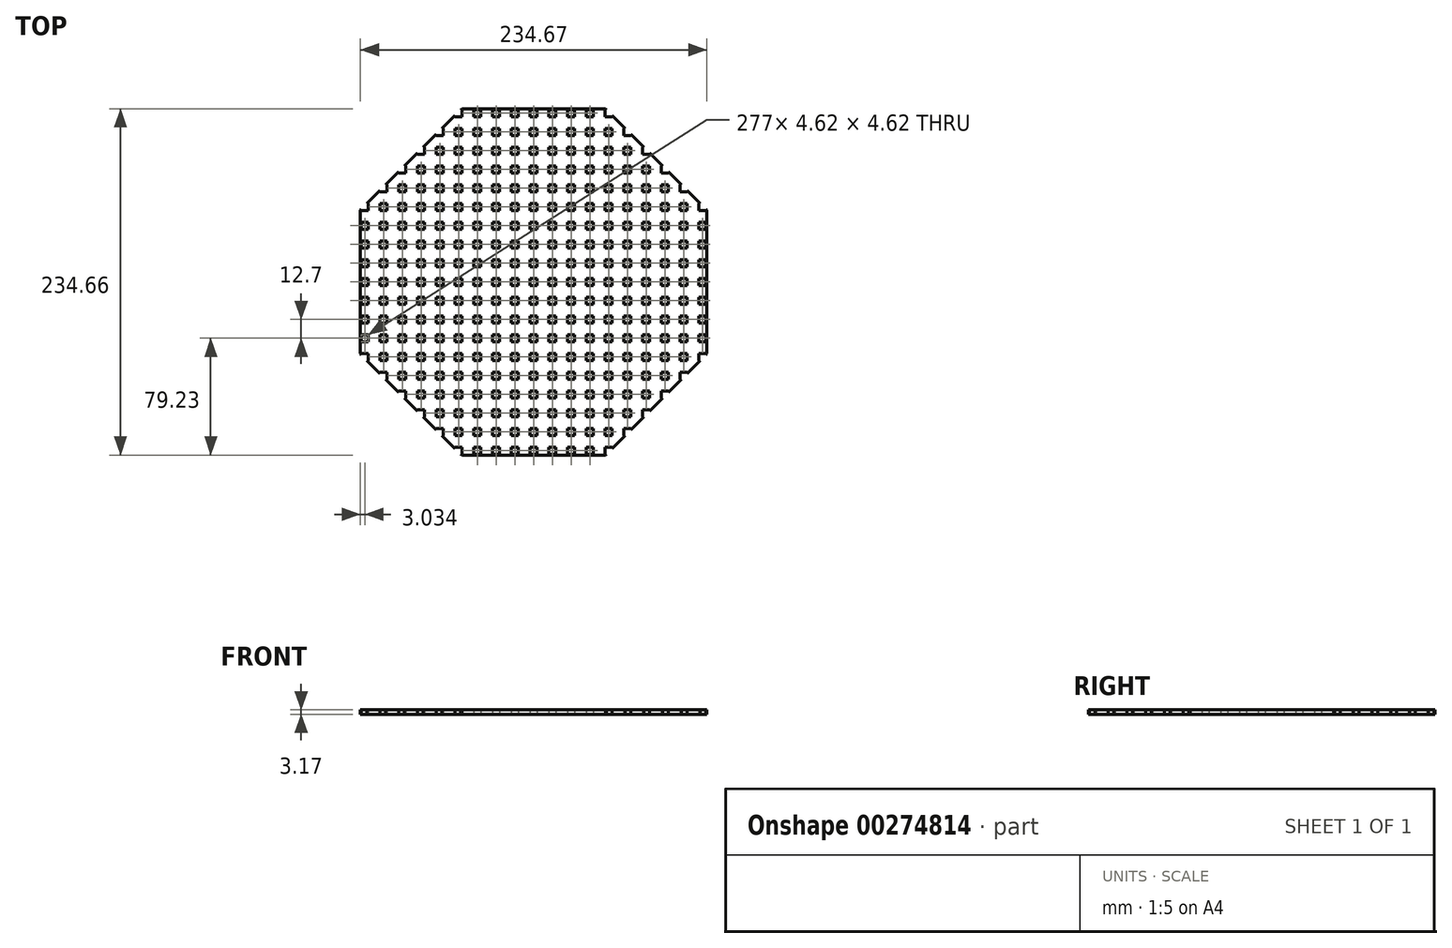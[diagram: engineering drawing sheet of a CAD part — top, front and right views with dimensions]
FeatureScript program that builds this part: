
annotation { "Feature Type Name" : "Feature", "Feature Type Description" : "" }
export const myFeature = defineFeature(function(context is Context, id is Id, definition is map)
    precondition{}
    {
        {
            var Q0;
            Q0=qCreatedBy(makeId("Top.planeOp"),FACE);
            var sketch = newSketch(context, id + "F0", { "sketchPlane" : qUnion([Q0])});
            skCircle(sketch, "E0.cCircle", {"center": v(2.93, 2.21) * mm, "radius": 127 * mm, "construction": true});
            skLineSegment(sketch, "E0.0", {"start": v(-114.4, 50.81) * mm, "end": v(-45.67, 119.54) * mm});
            skLineSegment(sketch, "E0.1", {"start": v(-45.67, 119.54) * mm, "end": v(51.53, 119.54) * mm});
            skLineSegment(sketch, "E0.2", {"start": v(51.53, 119.54) * mm, "end": v(120.27, 50.81) * mm});
            skLineSegment(sketch, "E0.3", {"start": v(120.27, 50.81) * mm, "end": v(120.27, -46.4) * mm});
            skLineSegment(sketch, "E0.4", {"start": v(120.27, -46.4) * mm, "end": v(51.53, -115.12) * mm});
            skLineSegment(sketch, "E0.5", {"start": v(51.53, -115.12) * mm, "end": v(-45.67, -115.12) * mm});
            skLineSegment(sketch, "E0.6", {"start": v(-45.67, -115.12) * mm, "end": v(-114.4, -46.4) * mm});
            skLineSegment(sketch, "E0.7", {"start": v(-114.4, -46.4) * mm, "end": v(-114.4, 50.81) * mm});
            skLineSegment(sketch, "E1.bottom", {"start": v(5.25, 4.52) * mm, "end": v(0.62, 4.52) * mm});
            skLineSegment(sketch, "E1.top", {"start": v(5.25, -0.1) * mm, "end": v(0.62, -0.1) * mm});
            skLineSegment(sketch, "E1.left", {"start": v(5.25, 4.52) * mm, "end": v(5.25, -0.1) * mm});
            skLineSegment(sketch, "E1.right", {"start": v(0.62, 4.52) * mm, "end": v(0.62, -0.1) * mm});
            skLineSegment(sketch, "E2", {"start": v(2.93, 2.21) * mm, "end": v(2.93, 119.54) * mm});
            skLineSegment(sketch, "E3", {"start": v(2.93, 2.21) * mm, "end": v(2.93, -115.12) * mm});
            skLineSegment(sketch, "E4", {"start": v(2.93, 2.21) * mm, "end": v(120.27, 2.21) * mm});
            skLineSegment(sketch, "E5", {"start": v(2.93, 2.21) * mm, "end": v(-114.4, 2.21) * mm});
            skLineSegment(sketch, "E6.0.1.0", {"start": v(5.25, 17.22) * mm, "end": v(0.62, 17.22) * mm});
            skLineSegment(sketch, "E6.0.1.1", {"start": v(0.62, 17.22) * mm, "end": v(0.62, 12.6) * mm});
            skLineSegment(sketch, "E6.0.1.2", {"start": v(5.25, 12.6) * mm, "end": v(0.62, 12.6) * mm});
            skLineSegment(sketch, "E6.0.1.3", {"start": v(5.25, 17.22) * mm, "end": v(5.25, 12.6) * mm});
            skLineSegment(sketch, "E6.0.2.0", {"start": v(5.25, 29.92) * mm, "end": v(0.62, 29.92) * mm});
            skLineSegment(sketch, "E6.0.2.1", {"start": v(0.62, 29.92) * mm, "end": v(0.62, 25.3) * mm});
            skLineSegment(sketch, "E6.0.2.2", {"start": v(5.25, 25.3) * mm, "end": v(0.62, 25.3) * mm});
            skLineSegment(sketch, "E6.0.2.3", {"start": v(5.25, 29.92) * mm, "end": v(5.25, 25.3) * mm});
            skLineSegment(sketch, "E6.0.3.0", {"start": v(5.25, 42.62) * mm, "end": v(0.62, 42.62) * mm});
            skLineSegment(sketch, "E6.0.3.1", {"start": v(0.62, 42.62) * mm, "end": v(0.62, 38) * mm});
            skLineSegment(sketch, "E6.0.3.2", {"start": v(5.25, 38) * mm, "end": v(0.62, 38) * mm});
            skLineSegment(sketch, "E6.0.3.3", {"start": v(5.25, 42.62) * mm, "end": v(5.25, 38) * mm});
            skLineSegment(sketch, "E6.0.4.0", {"start": v(5.25, 55.32) * mm, "end": v(0.62, 55.32) * mm});
            skLineSegment(sketch, "E6.0.4.1", {"start": v(0.62, 55.32) * mm, "end": v(0.62, 50.7) * mm});
            skLineSegment(sketch, "E6.0.4.2", {"start": v(5.25, 50.7) * mm, "end": v(0.62, 50.7) * mm});
            skLineSegment(sketch, "E6.0.4.3", {"start": v(5.25, 55.32) * mm, "end": v(5.25, 50.7) * mm});
            skLineSegment(sketch, "E6.0.5.0", {"start": v(5.25, 68.02) * mm, "end": v(0.62, 68.02) * mm});
            skLineSegment(sketch, "E6.0.5.1", {"start": v(0.62, 68.02) * mm, "end": v(0.62, 63.4) * mm});
            skLineSegment(sketch, "E6.0.5.2", {"start": v(5.25, 63.4) * mm, "end": v(0.62, 63.4) * mm});
            skLineSegment(sketch, "E6.0.5.3", {"start": v(5.25, 68.02) * mm, "end": v(5.25, 63.4) * mm});
            skLineSegment(sketch, "E6.0.6.0", {"start": v(5.25, 80.72) * mm, "end": v(0.62, 80.72) * mm});
            skLineSegment(sketch, "E6.0.6.1", {"start": v(0.62, 80.72) * mm, "end": v(0.62, 76.1) * mm});
            skLineSegment(sketch, "E6.0.6.2", {"start": v(5.25, 76.1) * mm, "end": v(0.62, 76.1) * mm});
            skLineSegment(sketch, "E6.0.6.3", {"start": v(5.25, 80.72) * mm, "end": v(5.25, 76.1) * mm});
            skLineSegment(sketch, "E6.0.7.0", {"start": v(5.25, 93.42) * mm, "end": v(0.62, 93.42) * mm});
            skLineSegment(sketch, "E6.0.7.1", {"start": v(0.62, 93.42) * mm, "end": v(0.62, 88.8) * mm});
            skLineSegment(sketch, "E6.0.7.2", {"start": v(5.25, 88.8) * mm, "end": v(0.62, 88.8) * mm});
            skLineSegment(sketch, "E6.0.7.3", {"start": v(5.25, 93.42) * mm, "end": v(5.25, 88.8) * mm});
            skLineSegment(sketch, "E6.0.8.0", {"start": v(5.25, 106.12) * mm, "end": v(0.62, 106.12) * mm});
            skLineSegment(sketch, "E6.0.8.1", {"start": v(0.62, 106.12) * mm, "end": v(0.62, 101.5) * mm});
            skLineSegment(sketch, "E6.0.8.2", {"start": v(5.25, 101.5) * mm, "end": v(0.62, 101.5) * mm});
            skLineSegment(sketch, "E6.0.8.3", {"start": v(5.25, 106.12) * mm, "end": v(5.25, 101.5) * mm});
            skLineSegment(sketch, "E6.0.9.0", {"start": v(5.25, 118.82) * mm, "end": v(0.62, 118.82) * mm});
            skLineSegment(sketch, "E6.0.9.1", {"start": v(0.62, 118.82) * mm, "end": v(0.62, 114.2) * mm});
            skLineSegment(sketch, "E6.0.9.2", {"start": v(5.25, 114.2) * mm, "end": v(0.62, 114.2) * mm});
            skLineSegment(sketch, "E6.0.9.3", {"start": v(5.25, 118.82) * mm, "end": v(5.25, 114.2) * mm});
            skLineSegment(sketch, "E6.1.0.0", {"start": v(17.95, 4.52) * mm, "end": v(13.32, 4.52) * mm});
            skLineSegment(sketch, "E6.1.0.1", {"start": v(13.32, 4.52) * mm, "end": v(13.32, -0.1) * mm});
            skLineSegment(sketch, "E6.1.0.2", {"start": v(17.95, -0.1) * mm, "end": v(13.32, -0.1) * mm});
            skLineSegment(sketch, "E6.1.0.3", {"start": v(17.95, 4.52) * mm, "end": v(17.95, -0.1) * mm});
            skLineSegment(sketch, "E6.1.1.0", {"start": v(17.95, 17.22) * mm, "end": v(13.32, 17.22) * mm});
            skLineSegment(sketch, "E6.1.1.1", {"start": v(13.32, 17.22) * mm, "end": v(13.32, 12.6) * mm});
            skLineSegment(sketch, "E6.1.1.2", {"start": v(17.95, 12.6) * mm, "end": v(13.32, 12.6) * mm});
            skLineSegment(sketch, "E6.1.1.3", {"start": v(17.95, 17.22) * mm, "end": v(17.95, 12.6) * mm});
            skLineSegment(sketch, "E6.1.2.0", {"start": v(17.95, 29.92) * mm, "end": v(13.32, 29.92) * mm});
            skLineSegment(sketch, "E6.1.2.1", {"start": v(13.32, 29.92) * mm, "end": v(13.32, 25.3) * mm});
            skLineSegment(sketch, "E6.1.2.2", {"start": v(17.95, 25.3) * mm, "end": v(13.32, 25.3) * mm});
            skLineSegment(sketch, "E6.1.2.3", {"start": v(17.95, 29.92) * mm, "end": v(17.95, 25.3) * mm});
            skLineSegment(sketch, "E6.1.3.0", {"start": v(17.95, 42.62) * mm, "end": v(13.32, 42.62) * mm});
            skLineSegment(sketch, "E6.1.3.1", {"start": v(13.32, 42.62) * mm, "end": v(13.32, 38) * mm});
            skLineSegment(sketch, "E6.1.3.2", {"start": v(17.95, 38) * mm, "end": v(13.32, 38) * mm});
            skLineSegment(sketch, "E6.1.3.3", {"start": v(17.95, 42.62) * mm, "end": v(17.95, 38) * mm});
            skLineSegment(sketch, "E6.1.4.0", {"start": v(17.95, 55.32) * mm, "end": v(13.32, 55.32) * mm});
            skLineSegment(sketch, "E6.1.4.1", {"start": v(13.32, 55.32) * mm, "end": v(13.32, 50.7) * mm});
            skLineSegment(sketch, "E6.1.4.2", {"start": v(17.95, 50.7) * mm, "end": v(13.32, 50.7) * mm});
            skLineSegment(sketch, "E6.1.4.3", {"start": v(17.95, 55.32) * mm, "end": v(17.95, 50.7) * mm});
            skLineSegment(sketch, "E6.1.5.0", {"start": v(17.95, 68.02) * mm, "end": v(13.32, 68.02) * mm});
            skLineSegment(sketch, "E6.1.5.1", {"start": v(13.32, 68.02) * mm, "end": v(13.32, 63.4) * mm});
            skLineSegment(sketch, "E6.1.5.2", {"start": v(17.95, 63.4) * mm, "end": v(13.32, 63.4) * mm});
            skLineSegment(sketch, "E6.1.5.3", {"start": v(17.95, 68.02) * mm, "end": v(17.95, 63.4) * mm});
            skLineSegment(sketch, "E6.1.6.0", {"start": v(17.95, 80.72) * mm, "end": v(13.32, 80.72) * mm});
            skLineSegment(sketch, "E6.1.6.1", {"start": v(13.32, 80.72) * mm, "end": v(13.32, 76.1) * mm});
            skLineSegment(sketch, "E6.1.6.2", {"start": v(17.95, 76.1) * mm, "end": v(13.32, 76.1) * mm});
            skLineSegment(sketch, "E6.1.6.3", {"start": v(17.95, 80.72) * mm, "end": v(17.95, 76.1) * mm});
            skLineSegment(sketch, "E6.1.7.0", {"start": v(17.95, 93.42) * mm, "end": v(13.32, 93.42) * mm});
            skLineSegment(sketch, "E6.1.7.1", {"start": v(13.32, 93.42) * mm, "end": v(13.32, 88.8) * mm});
            skLineSegment(sketch, "E6.1.7.2", {"start": v(17.95, 88.8) * mm, "end": v(13.32, 88.8) * mm});
            skLineSegment(sketch, "E6.1.7.3", {"start": v(17.95, 93.42) * mm, "end": v(17.95, 88.8) * mm});
            skLineSegment(sketch, "E6.1.8.0", {"start": v(17.95, 106.12) * mm, "end": v(13.32, 106.12) * mm});
            skLineSegment(sketch, "E6.1.8.1", {"start": v(13.32, 106.12) * mm, "end": v(13.32, 101.5) * mm});
            skLineSegment(sketch, "E6.1.8.2", {"start": v(17.95, 101.5) * mm, "end": v(13.32, 101.5) * mm});
            skLineSegment(sketch, "E6.1.8.3", {"start": v(17.95, 106.12) * mm, "end": v(17.95, 101.5) * mm});
            skLineSegment(sketch, "E6.1.9.0", {"start": v(17.95, 118.82) * mm, "end": v(13.32, 118.82) * mm});
            skLineSegment(sketch, "E6.1.9.1", {"start": v(13.32, 118.82) * mm, "end": v(13.32, 114.2) * mm});
            skLineSegment(sketch, "E6.1.9.2", {"start": v(17.95, 114.2) * mm, "end": v(13.32, 114.2) * mm});
            skLineSegment(sketch, "E6.1.9.3", {"start": v(17.95, 118.82) * mm, "end": v(17.95, 114.2) * mm});
            skLineSegment(sketch, "E6.2.0.0", {"start": v(30.65, 4.52) * mm, "end": v(26.02, 4.52) * mm});
            skLineSegment(sketch, "E6.2.0.1", {"start": v(26.02, 4.52) * mm, "end": v(26.02, -0.1) * mm});
            skLineSegment(sketch, "E6.2.0.2", {"start": v(30.65, -0.1) * mm, "end": v(26.02, -0.1) * mm});
            skLineSegment(sketch, "E6.2.0.3", {"start": v(30.65, 4.52) * mm, "end": v(30.65, -0.1) * mm});
            skLineSegment(sketch, "E6.2.1.0", {"start": v(30.65, 17.22) * mm, "end": v(26.02, 17.22) * mm});
            skLineSegment(sketch, "E6.2.1.1", {"start": v(26.02, 17.22) * mm, "end": v(26.02, 12.6) * mm});
            skLineSegment(sketch, "E6.2.1.2", {"start": v(30.65, 12.6) * mm, "end": v(26.02, 12.6) * mm});
            skLineSegment(sketch, "E6.2.1.3", {"start": v(30.65, 17.22) * mm, "end": v(30.65, 12.6) * mm});
            skLineSegment(sketch, "E6.2.2.0", {"start": v(30.65, 29.92) * mm, "end": v(26.02, 29.92) * mm});
            skLineSegment(sketch, "E6.2.2.1", {"start": v(26.02, 29.92) * mm, "end": v(26.02, 25.3) * mm});
            skLineSegment(sketch, "E6.2.2.2", {"start": v(30.65, 25.3) * mm, "end": v(26.02, 25.3) * mm});
            skLineSegment(sketch, "E6.2.2.3", {"start": v(30.65, 29.92) * mm, "end": v(30.65, 25.3) * mm});
            skLineSegment(sketch, "E6.2.3.0", {"start": v(30.65, 42.62) * mm, "end": v(26.02, 42.62) * mm});
            skLineSegment(sketch, "E6.2.3.1", {"start": v(26.02, 42.62) * mm, "end": v(26.02, 38) * mm});
            skLineSegment(sketch, "E6.2.3.2", {"start": v(30.65, 38) * mm, "end": v(26.02, 38) * mm});
            skLineSegment(sketch, "E6.2.3.3", {"start": v(30.65, 42.62) * mm, "end": v(30.65, 38) * mm});
            skLineSegment(sketch, "E6.2.4.0", {"start": v(30.65, 55.32) * mm, "end": v(26.02, 55.32) * mm});
            skLineSegment(sketch, "E6.2.4.1", {"start": v(26.02, 55.32) * mm, "end": v(26.02, 50.7) * mm});
            skLineSegment(sketch, "E6.2.4.2", {"start": v(30.65, 50.7) * mm, "end": v(26.02, 50.7) * mm});
            skLineSegment(sketch, "E6.2.4.3", {"start": v(30.65, 55.32) * mm, "end": v(30.65, 50.7) * mm});
            skLineSegment(sketch, "E6.2.5.0", {"start": v(30.65, 68.02) * mm, "end": v(26.02, 68.02) * mm});
            skLineSegment(sketch, "E6.2.5.1", {"start": v(26.02, 68.02) * mm, "end": v(26.02, 63.4) * mm});
            skLineSegment(sketch, "E6.2.5.2", {"start": v(30.65, 63.4) * mm, "end": v(26.02, 63.4) * mm});
            skLineSegment(sketch, "E6.2.5.3", {"start": v(30.65, 68.02) * mm, "end": v(30.65, 63.4) * mm});
            skLineSegment(sketch, "E6.2.6.0", {"start": v(30.65, 80.72) * mm, "end": v(26.02, 80.72) * mm});
            skLineSegment(sketch, "E6.2.6.1", {"start": v(26.02, 80.72) * mm, "end": v(26.02, 76.1) * mm});
            skLineSegment(sketch, "E6.2.6.2", {"start": v(30.65, 76.1) * mm, "end": v(26.02, 76.1) * mm});
            skLineSegment(sketch, "E6.2.6.3", {"start": v(30.65, 80.72) * mm, "end": v(30.65, 76.1) * mm});
            skLineSegment(sketch, "E6.2.7.0", {"start": v(30.65, 93.42) * mm, "end": v(26.02, 93.42) * mm});
            skLineSegment(sketch, "E6.2.7.1", {"start": v(26.02, 93.42) * mm, "end": v(26.02, 88.8) * mm});
            skLineSegment(sketch, "E6.2.7.2", {"start": v(30.65, 88.8) * mm, "end": v(26.02, 88.8) * mm});
            skLineSegment(sketch, "E6.2.7.3", {"start": v(30.65, 93.42) * mm, "end": v(30.65, 88.8) * mm});
            skLineSegment(sketch, "E6.2.8.0", {"start": v(30.65, 106.12) * mm, "end": v(26.02, 106.12) * mm});
            skLineSegment(sketch, "E6.2.8.1", {"start": v(26.02, 106.12) * mm, "end": v(26.02, 101.5) * mm});
            skLineSegment(sketch, "E6.2.8.2", {"start": v(30.65, 101.5) * mm, "end": v(26.02, 101.5) * mm});
            skLineSegment(sketch, "E6.2.8.3", {"start": v(30.65, 106.12) * mm, "end": v(30.65, 101.5) * mm});
            skLineSegment(sketch, "E6.2.9.0", {"start": v(30.65, 118.82) * mm, "end": v(26.02, 118.82) * mm});
            skLineSegment(sketch, "E6.2.9.1", {"start": v(26.02, 118.82) * mm, "end": v(26.02, 114.2) * mm});
            skLineSegment(sketch, "E6.2.9.2", {"start": v(30.65, 114.2) * mm, "end": v(26.02, 114.2) * mm});
            skLineSegment(sketch, "E6.2.9.3", {"start": v(30.65, 118.82) * mm, "end": v(30.65, 114.2) * mm});
            skLineSegment(sketch, "E6.3.0.0", {"start": v(43.35, 4.52) * mm, "end": v(38.72, 4.52) * mm});
            skLineSegment(sketch, "E6.3.0.1", {"start": v(38.72, 4.52) * mm, "end": v(38.72, -0.1) * mm});
            skLineSegment(sketch, "E6.3.0.2", {"start": v(43.35, -0.1) * mm, "end": v(38.72, -0.1) * mm});
            skLineSegment(sketch, "E6.3.0.3", {"start": v(43.35, 4.52) * mm, "end": v(43.35, -0.1) * mm});
            skLineSegment(sketch, "E6.3.1.0", {"start": v(43.35, 17.22) * mm, "end": v(38.72, 17.22) * mm});
            skLineSegment(sketch, "E6.3.1.1", {"start": v(38.72, 17.22) * mm, "end": v(38.72, 12.6) * mm});
            skLineSegment(sketch, "E6.3.1.2", {"start": v(43.35, 12.6) * mm, "end": v(38.72, 12.6) * mm});
            skLineSegment(sketch, "E6.3.1.3", {"start": v(43.35, 17.22) * mm, "end": v(43.35, 12.6) * mm});
            skLineSegment(sketch, "E6.3.2.0", {"start": v(43.35, 29.92) * mm, "end": v(38.72, 29.92) * mm});
            skLineSegment(sketch, "E6.3.2.1", {"start": v(38.72, 29.92) * mm, "end": v(38.72, 25.3) * mm});
            skLineSegment(sketch, "E6.3.2.2", {"start": v(43.35, 25.3) * mm, "end": v(38.72, 25.3) * mm});
            skLineSegment(sketch, "E6.3.2.3", {"start": v(43.35, 29.92) * mm, "end": v(43.35, 25.3) * mm});
            skLineSegment(sketch, "E6.3.3.0", {"start": v(43.35, 42.62) * mm, "end": v(38.72, 42.62) * mm});
            skLineSegment(sketch, "E6.3.3.1", {"start": v(38.72, 42.62) * mm, "end": v(38.72, 38) * mm});
            skLineSegment(sketch, "E6.3.3.2", {"start": v(43.35, 38) * mm, "end": v(38.72, 38) * mm});
            skLineSegment(sketch, "E6.3.3.3", {"start": v(43.35, 42.62) * mm, "end": v(43.35, 38) * mm});
            skLineSegment(sketch, "E6.3.4.0", {"start": v(43.35, 55.32) * mm, "end": v(38.72, 55.32) * mm});
            skLineSegment(sketch, "E6.3.4.1", {"start": v(38.72, 55.32) * mm, "end": v(38.72, 50.7) * mm});
            skLineSegment(sketch, "E6.3.4.2", {"start": v(43.35, 50.7) * mm, "end": v(38.72, 50.7) * mm});
            skLineSegment(sketch, "E6.3.4.3", {"start": v(43.35, 55.32) * mm, "end": v(43.35, 50.7) * mm});
            skLineSegment(sketch, "E6.3.5.0", {"start": v(43.35, 68.02) * mm, "end": v(38.72, 68.02) * mm});
            skLineSegment(sketch, "E6.3.5.1", {"start": v(38.72, 68.02) * mm, "end": v(38.72, 63.4) * mm});
            skLineSegment(sketch, "E6.3.5.2", {"start": v(43.35, 63.4) * mm, "end": v(38.72, 63.4) * mm});
            skLineSegment(sketch, "E6.3.5.3", {"start": v(43.35, 68.02) * mm, "end": v(43.35, 63.4) * mm});
            skLineSegment(sketch, "E6.3.6.0", {"start": v(43.35, 80.72) * mm, "end": v(38.72, 80.72) * mm});
            skLineSegment(sketch, "E6.3.6.1", {"start": v(38.72, 80.72) * mm, "end": v(38.72, 76.1) * mm});
            skLineSegment(sketch, "E6.3.6.2", {"start": v(43.35, 76.1) * mm, "end": v(38.72, 76.1) * mm});
            skLineSegment(sketch, "E6.3.6.3", {"start": v(43.35, 80.72) * mm, "end": v(43.35, 76.1) * mm});
            skLineSegment(sketch, "E6.3.7.0", {"start": v(43.35, 93.42) * mm, "end": v(38.72, 93.42) * mm});
            skLineSegment(sketch, "E6.3.7.1", {"start": v(38.72, 93.42) * mm, "end": v(38.72, 88.8) * mm});
            skLineSegment(sketch, "E6.3.7.2", {"start": v(43.35, 88.8) * mm, "end": v(38.72, 88.8) * mm});
            skLineSegment(sketch, "E6.3.7.3", {"start": v(43.35, 93.42) * mm, "end": v(43.35, 88.8) * mm});
            skLineSegment(sketch, "E6.3.8.0", {"start": v(43.35, 106.12) * mm, "end": v(38.72, 106.12) * mm});
            skLineSegment(sketch, "E6.3.8.1", {"start": v(38.72, 106.12) * mm, "end": v(38.72, 101.5) * mm});
            skLineSegment(sketch, "E6.3.8.2", {"start": v(43.35, 101.5) * mm, "end": v(38.72, 101.5) * mm});
            skLineSegment(sketch, "E6.3.8.3", {"start": v(43.35, 106.12) * mm, "end": v(43.35, 101.5) * mm});
            skLineSegment(sketch, "E6.3.9.0", {"start": v(43.35, 118.82) * mm, "end": v(38.72, 118.82) * mm});
            skLineSegment(sketch, "E6.3.9.1", {"start": v(38.72, 118.82) * mm, "end": v(38.72, 114.2) * mm});
            skLineSegment(sketch, "E6.3.9.2", {"start": v(43.35, 114.2) * mm, "end": v(38.72, 114.2) * mm});
            skLineSegment(sketch, "E6.3.9.3", {"start": v(43.35, 118.82) * mm, "end": v(43.35, 114.2) * mm});
            skLineSegment(sketch, "E6.4.0.0", {"start": v(56.05, 4.52) * mm, "end": v(51.42, 4.52) * mm});
            skLineSegment(sketch, "E6.4.0.1", {"start": v(51.42, 4.52) * mm, "end": v(51.42, -0.1) * mm});
            skLineSegment(sketch, "E6.4.0.2", {"start": v(56.05, -0.1) * mm, "end": v(51.42, -0.1) * mm});
            skLineSegment(sketch, "E6.4.0.3", {"start": v(56.05, 4.52) * mm, "end": v(56.05, -0.1) * mm});
            skLineSegment(sketch, "E6.4.1.0", {"start": v(56.05, 17.22) * mm, "end": v(51.42, 17.22) * mm});
            skLineSegment(sketch, "E6.4.1.1", {"start": v(51.42, 17.22) * mm, "end": v(51.42, 12.6) * mm});
            skLineSegment(sketch, "E6.4.1.2", {"start": v(56.05, 12.6) * mm, "end": v(51.42, 12.6) * mm});
            skLineSegment(sketch, "E6.4.1.3", {"start": v(56.05, 17.22) * mm, "end": v(56.05, 12.6) * mm});
            skLineSegment(sketch, "E6.4.2.0", {"start": v(56.05, 29.92) * mm, "end": v(51.42, 29.92) * mm});
            skLineSegment(sketch, "E6.4.2.1", {"start": v(51.42, 29.92) * mm, "end": v(51.42, 25.3) * mm});
            skLineSegment(sketch, "E6.4.2.2", {"start": v(56.05, 25.3) * mm, "end": v(51.42, 25.3) * mm});
            skLineSegment(sketch, "E6.4.2.3", {"start": v(56.05, 29.92) * mm, "end": v(56.05, 25.3) * mm});
            skLineSegment(sketch, "E6.4.3.0", {"start": v(56.05, 42.62) * mm, "end": v(51.42, 42.62) * mm});
            skLineSegment(sketch, "E6.4.3.1", {"start": v(51.42, 42.62) * mm, "end": v(51.42, 38) * mm});
            skLineSegment(sketch, "E6.4.3.2", {"start": v(56.05, 38) * mm, "end": v(51.42, 38) * mm});
            skLineSegment(sketch, "E6.4.3.3", {"start": v(56.05, 42.62) * mm, "end": v(56.05, 38) * mm});
            skLineSegment(sketch, "E6.4.4.0", {"start": v(56.05, 55.32) * mm, "end": v(51.42, 55.32) * mm});
            skLineSegment(sketch, "E6.4.4.1", {"start": v(51.42, 55.32) * mm, "end": v(51.42, 50.7) * mm});
            skLineSegment(sketch, "E6.4.4.2", {"start": v(56.05, 50.7) * mm, "end": v(51.42, 50.7) * mm});
            skLineSegment(sketch, "E6.4.4.3", {"start": v(56.05, 55.32) * mm, "end": v(56.05, 50.7) * mm});
            skLineSegment(sketch, "E6.4.5.0", {"start": v(56.05, 68.02) * mm, "end": v(51.42, 68.02) * mm});
            skLineSegment(sketch, "E6.4.5.1", {"start": v(51.42, 68.02) * mm, "end": v(51.42, 63.4) * mm});
            skLineSegment(sketch, "E6.4.5.2", {"start": v(56.05, 63.4) * mm, "end": v(51.42, 63.4) * mm});
            skLineSegment(sketch, "E6.4.5.3", {"start": v(56.05, 68.02) * mm, "end": v(56.05, 63.4) * mm});
            skLineSegment(sketch, "E6.4.6.0", {"start": v(56.05, 80.72) * mm, "end": v(51.42, 80.72) * mm});
            skLineSegment(sketch, "E6.4.6.1", {"start": v(51.42, 80.72) * mm, "end": v(51.42, 76.1) * mm});
            skLineSegment(sketch, "E6.4.6.2", {"start": v(56.05, 76.1) * mm, "end": v(51.42, 76.1) * mm});
            skLineSegment(sketch, "E6.4.6.3", {"start": v(56.05, 80.72) * mm, "end": v(56.05, 76.1) * mm});
            skLineSegment(sketch, "E6.4.7.0", {"start": v(56.05, 93.42) * mm, "end": v(51.42, 93.42) * mm});
            skLineSegment(sketch, "E6.4.7.1", {"start": v(51.42, 93.42) * mm, "end": v(51.42, 88.8) * mm});
            skLineSegment(sketch, "E6.4.7.2", {"start": v(56.05, 88.8) * mm, "end": v(51.42, 88.8) * mm});
            skLineSegment(sketch, "E6.4.7.3", {"start": v(56.05, 93.42) * mm, "end": v(56.05, 88.8) * mm});
            skLineSegment(sketch, "E6.4.8.0", {"start": v(56.05, 106.12) * mm, "end": v(51.42, 106.12) * mm});
            skLineSegment(sketch, "E6.4.8.1", {"start": v(51.42, 106.12) * mm, "end": v(51.42, 101.5) * mm});
            skLineSegment(sketch, "E6.4.8.2", {"start": v(56.05, 101.5) * mm, "end": v(51.42, 101.5) * mm});
            skLineSegment(sketch, "E6.4.8.3", {"start": v(56.05, 106.12) * mm, "end": v(56.05, 101.5) * mm});
            skLineSegment(sketch, "E6.4.9.0", {"start": v(56.05, 118.82) * mm, "end": v(51.42, 118.82) * mm});
            skLineSegment(sketch, "E6.4.9.1", {"start": v(51.42, 118.82) * mm, "end": v(51.42, 114.2) * mm});
            skLineSegment(sketch, "E6.4.9.2", {"start": v(56.05, 114.2) * mm, "end": v(51.42, 114.2) * mm});
            skLineSegment(sketch, "E6.4.9.3", {"start": v(56.05, 118.82) * mm, "end": v(56.05, 114.2) * mm});
            skLineSegment(sketch, "E6.5.0.0", {"start": v(68.75, 4.52) * mm, "end": v(64.12, 4.52) * mm});
            skLineSegment(sketch, "E6.5.0.1", {"start": v(64.12, 4.52) * mm, "end": v(64.12, -0.1) * mm});
            skLineSegment(sketch, "E6.5.0.2", {"start": v(68.75, -0.1) * mm, "end": v(64.12, -0.1) * mm});
            skLineSegment(sketch, "E6.5.0.3", {"start": v(68.75, 4.52) * mm, "end": v(68.75, -0.1) * mm});
            skLineSegment(sketch, "E6.5.1.0", {"start": v(68.75, 17.22) * mm, "end": v(64.12, 17.22) * mm});
            skLineSegment(sketch, "E6.5.1.1", {"start": v(64.12, 17.22) * mm, "end": v(64.12, 12.6) * mm});
            skLineSegment(sketch, "E6.5.1.2", {"start": v(68.75, 12.6) * mm, "end": v(64.12, 12.6) * mm});
            skLineSegment(sketch, "E6.5.1.3", {"start": v(68.75, 17.22) * mm, "end": v(68.75, 12.6) * mm});
            skLineSegment(sketch, "E6.5.2.0", {"start": v(68.75, 29.92) * mm, "end": v(64.12, 29.92) * mm});
            skLineSegment(sketch, "E6.5.2.1", {"start": v(64.12, 29.92) * mm, "end": v(64.12, 25.3) * mm});
            skLineSegment(sketch, "E6.5.2.2", {"start": v(68.75, 25.3) * mm, "end": v(64.12, 25.3) * mm});
            skLineSegment(sketch, "E6.5.2.3", {"start": v(68.75, 29.92) * mm, "end": v(68.75, 25.3) * mm});
            skLineSegment(sketch, "E6.5.3.0", {"start": v(68.75, 42.62) * mm, "end": v(64.12, 42.62) * mm});
            skLineSegment(sketch, "E6.5.3.1", {"start": v(64.12, 42.62) * mm, "end": v(64.12, 38) * mm});
            skLineSegment(sketch, "E6.5.3.2", {"start": v(68.75, 38) * mm, "end": v(64.12, 38) * mm});
            skLineSegment(sketch, "E6.5.3.3", {"start": v(68.75, 42.62) * mm, "end": v(68.75, 38) * mm});
            skLineSegment(sketch, "E6.5.4.0", {"start": v(68.75, 55.32) * mm, "end": v(64.12, 55.32) * mm});
            skLineSegment(sketch, "E6.5.4.1", {"start": v(64.12, 55.32) * mm, "end": v(64.12, 50.7) * mm});
            skLineSegment(sketch, "E6.5.4.2", {"start": v(68.75, 50.7) * mm, "end": v(64.12, 50.7) * mm});
            skLineSegment(sketch, "E6.5.4.3", {"start": v(68.75, 55.32) * mm, "end": v(68.75, 50.7) * mm});
            skLineSegment(sketch, "E6.5.5.0", {"start": v(68.75, 68.02) * mm, "end": v(64.12, 68.02) * mm});
            skLineSegment(sketch, "E6.5.5.1", {"start": v(64.12, 68.02) * mm, "end": v(64.12, 63.4) * mm});
            skLineSegment(sketch, "E6.5.5.2", {"start": v(68.75, 63.4) * mm, "end": v(64.12, 63.4) * mm});
            skLineSegment(sketch, "E6.5.5.3", {"start": v(68.75, 68.02) * mm, "end": v(68.75, 63.4) * mm});
            skLineSegment(sketch, "E6.5.6.0", {"start": v(68.75, 80.72) * mm, "end": v(64.12, 80.72) * mm});
            skLineSegment(sketch, "E6.5.6.1", {"start": v(64.12, 80.72) * mm, "end": v(64.12, 76.1) * mm});
            skLineSegment(sketch, "E6.5.6.2", {"start": v(68.75, 76.1) * mm, "end": v(64.12, 76.1) * mm});
            skLineSegment(sketch, "E6.5.6.3", {"start": v(68.75, 80.72) * mm, "end": v(68.75, 76.1) * mm});
            skLineSegment(sketch, "E6.5.7.0", {"start": v(68.75, 93.42) * mm, "end": v(64.12, 93.42) * mm});
            skLineSegment(sketch, "E6.5.7.1", {"start": v(64.12, 93.42) * mm, "end": v(64.12, 88.8) * mm});
            skLineSegment(sketch, "E6.5.7.2", {"start": v(68.75, 88.8) * mm, "end": v(64.12, 88.8) * mm});
            skLineSegment(sketch, "E6.5.7.3", {"start": v(68.75, 93.42) * mm, "end": v(68.75, 88.8) * mm});
            skLineSegment(sketch, "E6.5.8.0", {"start": v(68.75, 106.12) * mm, "end": v(64.12, 106.12) * mm});
            skLineSegment(sketch, "E6.5.8.1", {"start": v(64.12, 106.12) * mm, "end": v(64.12, 101.5) * mm});
            skLineSegment(sketch, "E6.5.8.2", {"start": v(68.75, 101.5) * mm, "end": v(64.12, 101.5) * mm});
            skLineSegment(sketch, "E6.5.8.3", {"start": v(68.75, 106.12) * mm, "end": v(68.75, 101.5) * mm});
            skLineSegment(sketch, "E6.5.9.0", {"start": v(68.75, 118.82) * mm, "end": v(64.12, 118.82) * mm});
            skLineSegment(sketch, "E6.5.9.1", {"start": v(64.12, 118.82) * mm, "end": v(64.12, 114.2) * mm});
            skLineSegment(sketch, "E6.5.9.2", {"start": v(68.75, 114.2) * mm, "end": v(64.12, 114.2) * mm});
            skLineSegment(sketch, "E6.5.9.3", {"start": v(68.75, 118.82) * mm, "end": v(68.75, 114.2) * mm});
            skLineSegment(sketch, "E6.6.0.0", {"start": v(81.45, 4.52) * mm, "end": v(76.82, 4.52) * mm});
            skLineSegment(sketch, "E6.6.0.1", {"start": v(76.82, 4.52) * mm, "end": v(76.82, -0.1) * mm});
            skLineSegment(sketch, "E6.6.0.2", {"start": v(81.45, -0.1) * mm, "end": v(76.82, -0.1) * mm});
            skLineSegment(sketch, "E6.6.0.3", {"start": v(81.45, 4.52) * mm, "end": v(81.45, -0.1) * mm});
            skLineSegment(sketch, "E6.6.1.0", {"start": v(81.45, 17.22) * mm, "end": v(76.82, 17.22) * mm});
            skLineSegment(sketch, "E6.6.1.1", {"start": v(76.82, 17.22) * mm, "end": v(76.82, 12.6) * mm});
            skLineSegment(sketch, "E6.6.1.2", {"start": v(81.45, 12.6) * mm, "end": v(76.82, 12.6) * mm});
            skLineSegment(sketch, "E6.6.1.3", {"start": v(81.45, 17.22) * mm, "end": v(81.45, 12.6) * mm});
            skLineSegment(sketch, "E6.6.2.0", {"start": v(81.45, 29.92) * mm, "end": v(76.82, 29.92) * mm});
            skLineSegment(sketch, "E6.6.2.1", {"start": v(76.82, 29.92) * mm, "end": v(76.82, 25.3) * mm});
            skLineSegment(sketch, "E6.6.2.2", {"start": v(81.45, 25.3) * mm, "end": v(76.82, 25.3) * mm});
            skLineSegment(sketch, "E6.6.2.3", {"start": v(81.45, 29.92) * mm, "end": v(81.45, 25.3) * mm});
            skLineSegment(sketch, "E6.6.3.0", {"start": v(81.45, 42.62) * mm, "end": v(76.82, 42.62) * mm});
            skLineSegment(sketch, "E6.6.3.1", {"start": v(76.82, 42.62) * mm, "end": v(76.82, 38) * mm});
            skLineSegment(sketch, "E6.6.3.2", {"start": v(81.45, 38) * mm, "end": v(76.82, 38) * mm});
            skLineSegment(sketch, "E6.6.3.3", {"start": v(81.45, 42.62) * mm, "end": v(81.45, 38) * mm});
            skLineSegment(sketch, "E6.6.4.0", {"start": v(81.45, 55.32) * mm, "end": v(76.82, 55.32) * mm});
            skLineSegment(sketch, "E6.6.4.1", {"start": v(76.82, 55.32) * mm, "end": v(76.82, 50.7) * mm});
            skLineSegment(sketch, "E6.6.4.2", {"start": v(81.45, 50.7) * mm, "end": v(76.82, 50.7) * mm});
            skLineSegment(sketch, "E6.6.4.3", {"start": v(81.45, 55.32) * mm, "end": v(81.45, 50.7) * mm});
            skLineSegment(sketch, "E6.6.5.0", {"start": v(81.45, 68.02) * mm, "end": v(76.82, 68.02) * mm});
            skLineSegment(sketch, "E6.6.5.1", {"start": v(76.82, 68.02) * mm, "end": v(76.82, 63.4) * mm});
            skLineSegment(sketch, "E6.6.5.2", {"start": v(81.45, 63.4) * mm, "end": v(76.82, 63.4) * mm});
            skLineSegment(sketch, "E6.6.5.3", {"start": v(81.45, 68.02) * mm, "end": v(81.45, 63.4) * mm});
            skLineSegment(sketch, "E6.6.6.0", {"start": v(81.45, 80.72) * mm, "end": v(76.82, 80.72) * mm});
            skLineSegment(sketch, "E6.6.6.1", {"start": v(76.82, 80.72) * mm, "end": v(76.82, 76.1) * mm});
            skLineSegment(sketch, "E6.6.6.2", {"start": v(81.45, 76.1) * mm, "end": v(76.82, 76.1) * mm});
            skLineSegment(sketch, "E6.6.6.3", {"start": v(81.45, 80.72) * mm, "end": v(81.45, 76.1) * mm});
            skLineSegment(sketch, "E6.6.7.0", {"start": v(81.45, 93.42) * mm, "end": v(76.82, 93.42) * mm});
            skLineSegment(sketch, "E6.6.7.1", {"start": v(76.82, 93.42) * mm, "end": v(76.82, 88.8) * mm});
            skLineSegment(sketch, "E6.6.7.2", {"start": v(81.45, 88.8) * mm, "end": v(76.82, 88.8) * mm});
            skLineSegment(sketch, "E6.6.7.3", {"start": v(81.45, 93.42) * mm, "end": v(81.45, 88.8) * mm});
            skLineSegment(sketch, "E6.6.8.0", {"start": v(81.45, 106.12) * mm, "end": v(76.82, 106.12) * mm});
            skLineSegment(sketch, "E6.6.8.1", {"start": v(76.82, 106.12) * mm, "end": v(76.82, 101.5) * mm});
            skLineSegment(sketch, "E6.6.8.2", {"start": v(81.45, 101.5) * mm, "end": v(76.82, 101.5) * mm});
            skLineSegment(sketch, "E6.6.8.3", {"start": v(81.45, 106.12) * mm, "end": v(81.45, 101.5) * mm});
            skLineSegment(sketch, "E6.6.9.0", {"start": v(81.45, 118.82) * mm, "end": v(76.82, 118.82) * mm});
            skLineSegment(sketch, "E6.6.9.1", {"start": v(76.82, 118.82) * mm, "end": v(76.82, 114.2) * mm});
            skLineSegment(sketch, "E6.6.9.2", {"start": v(81.45, 114.2) * mm, "end": v(76.82, 114.2) * mm});
            skLineSegment(sketch, "E6.6.9.3", {"start": v(81.45, 118.82) * mm, "end": v(81.45, 114.2) * mm});
            skLineSegment(sketch, "E6.7.0.0", {"start": v(94.15, 4.52) * mm, "end": v(89.52, 4.52) * mm});
            skLineSegment(sketch, "E6.7.0.1", {"start": v(89.52, 4.52) * mm, "end": v(89.52, -0.1) * mm});
            skLineSegment(sketch, "E6.7.0.2", {"start": v(94.15, -0.1) * mm, "end": v(89.52, -0.1) * mm});
            skLineSegment(sketch, "E6.7.0.3", {"start": v(94.15, 4.52) * mm, "end": v(94.15, -0.1) * mm});
            skLineSegment(sketch, "E6.7.1.0", {"start": v(94.15, 17.22) * mm, "end": v(89.52, 17.22) * mm});
            skLineSegment(sketch, "E6.7.1.1", {"start": v(89.52, 17.22) * mm, "end": v(89.52, 12.6) * mm});
            skLineSegment(sketch, "E6.7.1.2", {"start": v(94.15, 12.6) * mm, "end": v(89.52, 12.6) * mm});
            skLineSegment(sketch, "E6.7.1.3", {"start": v(94.15, 17.22) * mm, "end": v(94.15, 12.6) * mm});
            skLineSegment(sketch, "E6.7.2.0", {"start": v(94.15, 29.92) * mm, "end": v(89.52, 29.92) * mm});
            skLineSegment(sketch, "E6.7.2.1", {"start": v(89.52, 29.92) * mm, "end": v(89.52, 25.3) * mm});
            skLineSegment(sketch, "E6.7.2.2", {"start": v(94.15, 25.3) * mm, "end": v(89.52, 25.3) * mm});
            skLineSegment(sketch, "E6.7.2.3", {"start": v(94.15, 29.92) * mm, "end": v(94.15, 25.3) * mm});
            skLineSegment(sketch, "E6.7.3.0", {"start": v(94.15, 42.62) * mm, "end": v(89.52, 42.62) * mm});
            skLineSegment(sketch, "E6.7.3.1", {"start": v(89.52, 42.62) * mm, "end": v(89.52, 38) * mm});
            skLineSegment(sketch, "E6.7.3.2", {"start": v(94.15, 38) * mm, "end": v(89.52, 38) * mm});
            skLineSegment(sketch, "E6.7.3.3", {"start": v(94.15, 42.62) * mm, "end": v(94.15, 38) * mm});
            skLineSegment(sketch, "E6.7.4.0", {"start": v(94.15, 55.32) * mm, "end": v(89.52, 55.32) * mm});
            skLineSegment(sketch, "E6.7.4.1", {"start": v(89.52, 55.32) * mm, "end": v(89.52, 50.7) * mm});
            skLineSegment(sketch, "E6.7.4.2", {"start": v(94.15, 50.7) * mm, "end": v(89.52, 50.7) * mm});
            skLineSegment(sketch, "E6.7.4.3", {"start": v(94.15, 55.32) * mm, "end": v(94.15, 50.7) * mm});
            skLineSegment(sketch, "E6.7.5.0", {"start": v(94.15, 68.02) * mm, "end": v(89.52, 68.02) * mm});
            skLineSegment(sketch, "E6.7.5.1", {"start": v(89.52, 68.02) * mm, "end": v(89.52, 63.4) * mm});
            skLineSegment(sketch, "E6.7.5.2", {"start": v(94.15, 63.4) * mm, "end": v(89.52, 63.4) * mm});
            skLineSegment(sketch, "E6.7.5.3", {"start": v(94.15, 68.02) * mm, "end": v(94.15, 63.4) * mm});
            skLineSegment(sketch, "E6.7.6.0", {"start": v(94.15, 80.72) * mm, "end": v(89.52, 80.72) * mm});
            skLineSegment(sketch, "E6.7.6.1", {"start": v(89.52, 80.72) * mm, "end": v(89.52, 76.1) * mm});
            skLineSegment(sketch, "E6.7.6.2", {"start": v(94.15, 76.1) * mm, "end": v(89.52, 76.1) * mm});
            skLineSegment(sketch, "E6.7.6.3", {"start": v(94.15, 80.72) * mm, "end": v(94.15, 76.1) * mm});
            skLineSegment(sketch, "E6.7.7.0", {"start": v(94.15, 93.42) * mm, "end": v(89.52, 93.42) * mm});
            skLineSegment(sketch, "E6.7.7.1", {"start": v(89.52, 93.42) * mm, "end": v(89.52, 88.8) * mm});
            skLineSegment(sketch, "E6.7.7.2", {"start": v(94.15, 88.8) * mm, "end": v(89.52, 88.8) * mm});
            skLineSegment(sketch, "E6.7.7.3", {"start": v(94.15, 93.42) * mm, "end": v(94.15, 88.8) * mm});
            skLineSegment(sketch, "E6.7.8.0", {"start": v(94.15, 106.12) * mm, "end": v(89.52, 106.12) * mm});
            skLineSegment(sketch, "E6.7.8.1", {"start": v(89.52, 106.12) * mm, "end": v(89.52, 101.5) * mm});
            skLineSegment(sketch, "E6.7.8.2", {"start": v(94.15, 101.5) * mm, "end": v(89.52, 101.5) * mm});
            skLineSegment(sketch, "E6.7.8.3", {"start": v(94.15, 106.12) * mm, "end": v(94.15, 101.5) * mm});
            skLineSegment(sketch, "E6.7.9.0", {"start": v(94.15, 118.82) * mm, "end": v(89.52, 118.82) * mm});
            skLineSegment(sketch, "E6.7.9.1", {"start": v(89.52, 118.82) * mm, "end": v(89.52, 114.2) * mm});
            skLineSegment(sketch, "E6.7.9.2", {"start": v(94.15, 114.2) * mm, "end": v(89.52, 114.2) * mm});
            skLineSegment(sketch, "E6.7.9.3", {"start": v(94.15, 118.82) * mm, "end": v(94.15, 114.2) * mm});
            skLineSegment(sketch, "E6.8.0.0", {"start": v(106.85, 4.52) * mm, "end": v(102.22, 4.52) * mm});
            skLineSegment(sketch, "E6.8.0.1", {"start": v(102.22, 4.52) * mm, "end": v(102.22, -0.1) * mm});
            skLineSegment(sketch, "E6.8.0.2", {"start": v(106.85, -0.1) * mm, "end": v(102.22, -0.1) * mm});
            skLineSegment(sketch, "E6.8.0.3", {"start": v(106.85, 4.52) * mm, "end": v(106.85, -0.1) * mm});
            skLineSegment(sketch, "E6.8.1.0", {"start": v(106.85, 17.22) * mm, "end": v(102.22, 17.22) * mm});
            skLineSegment(sketch, "E6.8.1.1", {"start": v(102.22, 17.22) * mm, "end": v(102.22, 12.6) * mm});
            skLineSegment(sketch, "E6.8.1.2", {"start": v(106.85, 12.6) * mm, "end": v(102.22, 12.6) * mm});
            skLineSegment(sketch, "E6.8.1.3", {"start": v(106.85, 17.22) * mm, "end": v(106.85, 12.6) * mm});
            skLineSegment(sketch, "E6.8.2.0", {"start": v(106.85, 29.92) * mm, "end": v(102.22, 29.92) * mm});
            skLineSegment(sketch, "E6.8.2.1", {"start": v(102.22, 29.92) * mm, "end": v(102.22, 25.3) * mm});
            skLineSegment(sketch, "E6.8.2.2", {"start": v(106.85, 25.3) * mm, "end": v(102.22, 25.3) * mm});
            skLineSegment(sketch, "E6.8.2.3", {"start": v(106.85, 29.92) * mm, "end": v(106.85, 25.3) * mm});
            skLineSegment(sketch, "E6.8.3.0", {"start": v(106.85, 42.62) * mm, "end": v(102.22, 42.62) * mm});
            skLineSegment(sketch, "E6.8.3.1", {"start": v(102.22, 42.62) * mm, "end": v(102.22, 38) * mm});
            skLineSegment(sketch, "E6.8.3.2", {"start": v(106.85, 38) * mm, "end": v(102.22, 38) * mm});
            skLineSegment(sketch, "E6.8.3.3", {"start": v(106.85, 42.62) * mm, "end": v(106.85, 38) * mm});
            skLineSegment(sketch, "E6.8.4.0", {"start": v(106.85, 55.32) * mm, "end": v(102.22, 55.32) * mm});
            skLineSegment(sketch, "E6.8.4.1", {"start": v(102.22, 55.32) * mm, "end": v(102.22, 50.7) * mm});
            skLineSegment(sketch, "E6.8.4.2", {"start": v(106.85, 50.7) * mm, "end": v(102.22, 50.7) * mm});
            skLineSegment(sketch, "E6.8.4.3", {"start": v(106.85, 55.32) * mm, "end": v(106.85, 50.7) * mm});
            skLineSegment(sketch, "E6.8.5.0", {"start": v(106.85, 68.02) * mm, "end": v(102.22, 68.02) * mm});
            skLineSegment(sketch, "E6.8.5.1", {"start": v(102.22, 68.02) * mm, "end": v(102.22, 63.4) * mm});
            skLineSegment(sketch, "E6.8.5.2", {"start": v(106.85, 63.4) * mm, "end": v(102.22, 63.4) * mm});
            skLineSegment(sketch, "E6.8.5.3", {"start": v(106.85, 68.02) * mm, "end": v(106.85, 63.4) * mm});
            skLineSegment(sketch, "E6.8.6.0", {"start": v(106.85, 80.72) * mm, "end": v(102.22, 80.72) * mm});
            skLineSegment(sketch, "E6.8.6.1", {"start": v(102.22, 80.72) * mm, "end": v(102.22, 76.1) * mm});
            skLineSegment(sketch, "E6.8.6.2", {"start": v(106.85, 76.1) * mm, "end": v(102.22, 76.1) * mm});
            skLineSegment(sketch, "E6.8.6.3", {"start": v(106.85, 80.72) * mm, "end": v(106.85, 76.1) * mm});
            skLineSegment(sketch, "E6.8.7.0", {"start": v(106.85, 93.42) * mm, "end": v(102.22, 93.42) * mm});
            skLineSegment(sketch, "E6.8.7.1", {"start": v(102.22, 93.42) * mm, "end": v(102.22, 88.8) * mm});
            skLineSegment(sketch, "E6.8.7.2", {"start": v(106.85, 88.8) * mm, "end": v(102.22, 88.8) * mm});
            skLineSegment(sketch, "E6.8.7.3", {"start": v(106.85, 93.42) * mm, "end": v(106.85, 88.8) * mm});
            skLineSegment(sketch, "E6.9.0.0", {"start": v(119.55, 4.52) * mm, "end": v(114.92, 4.52) * mm});
            skLineSegment(sketch, "E6.9.0.1", {"start": v(114.92, 4.52) * mm, "end": v(114.92, -0.1) * mm});
            skLineSegment(sketch, "E6.9.0.2", {"start": v(119.55, -0.1) * mm, "end": v(114.92, -0.1) * mm});
            skLineSegment(sketch, "E6.9.0.3", {"start": v(119.55, 4.52) * mm, "end": v(119.55, -0.1) * mm});
            skLineSegment(sketch, "E6.9.1.0", {"start": v(119.55, 17.22) * mm, "end": v(114.92, 17.22) * mm});
            skLineSegment(sketch, "E6.9.1.1", {"start": v(114.92, 17.22) * mm, "end": v(114.92, 12.6) * mm});
            skLineSegment(sketch, "E6.9.1.2", {"start": v(119.55, 12.6) * mm, "end": v(114.92, 12.6) * mm});
            skLineSegment(sketch, "E6.9.1.3", {"start": v(119.55, 17.22) * mm, "end": v(119.55, 12.6) * mm});
            skLineSegment(sketch, "E6.9.2.0", {"start": v(119.55, 29.92) * mm, "end": v(114.92, 29.92) * mm});
            skLineSegment(sketch, "E6.9.2.1", {"start": v(114.92, 29.92) * mm, "end": v(114.92, 25.3) * mm});
            skLineSegment(sketch, "E6.9.2.2", {"start": v(119.55, 25.3) * mm, "end": v(114.92, 25.3) * mm});
            skLineSegment(sketch, "E6.9.2.3", {"start": v(119.55, 29.92) * mm, "end": v(119.55, 25.3) * mm});
            skLineSegment(sketch, "E6.9.3.0", {"start": v(119.55, 42.62) * mm, "end": v(114.92, 42.62) * mm});
            skLineSegment(sketch, "E6.9.3.1", {"start": v(114.92, 42.62) * mm, "end": v(114.92, 38) * mm});
            skLineSegment(sketch, "E6.9.3.2", {"start": v(119.55, 38) * mm, "end": v(114.92, 38) * mm});
            skLineSegment(sketch, "E6.9.3.3", {"start": v(119.55, 42.62) * mm, "end": v(119.55, 38) * mm});
            skLineSegment(sketch, "E6.9.4.0", {"start": v(119.55, 55.32) * mm, "end": v(114.92, 55.32) * mm});
            skLineSegment(sketch, "E6.9.4.1", {"start": v(114.92, 55.32) * mm, "end": v(114.92, 50.7) * mm});
            skLineSegment(sketch, "E6.9.4.2", {"start": v(119.55, 50.7) * mm, "end": v(114.92, 50.7) * mm});
            skLineSegment(sketch, "E6.9.4.3", {"start": v(119.55, 55.32) * mm, "end": v(119.55, 50.7) * mm});
            skLineSegment(sketch, "E6.9.5.0", {"start": v(119.55, 68.02) * mm, "end": v(114.92, 68.02) * mm});
            skLineSegment(sketch, "E6.9.5.1", {"start": v(114.92, 68.02) * mm, "end": v(114.92, 63.4) * mm});
            skLineSegment(sketch, "E6.9.5.2", {"start": v(119.55, 63.4) * mm, "end": v(114.92, 63.4) * mm});
            skLineSegment(sketch, "E6.9.5.3", {"start": v(119.55, 68.02) * mm, "end": v(119.55, 63.4) * mm});
            skLineSegment(sketch, "E6.9.6.0", {"start": v(119.55, 80.72) * mm, "end": v(114.92, 80.72) * mm});
            skLineSegment(sketch, "E6.9.6.1", {"start": v(114.92, 80.72) * mm, "end": v(114.92, 76.1) * mm});
            skLineSegment(sketch, "E6.9.6.2", {"start": v(119.55, 76.1) * mm, "end": v(114.92, 76.1) * mm});
            skLineSegment(sketch, "E6.9.6.3", {"start": v(119.55, 80.72) * mm, "end": v(119.55, 76.1) * mm});
            skLineSegment(sketch, "E6.9.7.0", {"start": v(119.55, 93.42) * mm, "end": v(114.92, 93.42) * mm});
            skLineSegment(sketch, "E6.9.7.1", {"start": v(114.92, 93.42) * mm, "end": v(114.92, 88.8) * mm});
            skLineSegment(sketch, "E6.9.7.2", {"start": v(119.55, 88.8) * mm, "end": v(114.92, 88.8) * mm});
            skLineSegment(sketch, "E6.9.7.3", {"start": v(119.55, 93.42) * mm, "end": v(119.55, 88.8) * mm});
            skLineSegment(sketch, "E7.1.0.0", {"start": v(-7.45, 4.52) * mm, "end": v(-12.08, 4.52) * mm});
            skLineSegment(sketch, "E7.1.0.1", {"start": v(-12.08, 4.52) * mm, "end": v(-12.08, -0.1) * mm});
            skLineSegment(sketch, "E7.1.0.2", {"start": v(-7.45, -0.1) * mm, "end": v(-12.08, -0.1) * mm});
            skLineSegment(sketch, "E7.1.0.3", {"start": v(-7.45, 4.52) * mm, "end": v(-7.45, -0.1) * mm});
            skLineSegment(sketch, "E7.1.1.0", {"start": v(-7.45, 17.22) * mm, "end": v(-12.08, 17.22) * mm});
            skLineSegment(sketch, "E7.1.1.1", {"start": v(-12.08, 17.22) * mm, "end": v(-12.08, 12.6) * mm});
            skLineSegment(sketch, "E7.1.1.2", {"start": v(-7.45, 12.6) * mm, "end": v(-12.08, 12.6) * mm});
            skLineSegment(sketch, "E7.1.1.3", {"start": v(-7.45, 17.22) * mm, "end": v(-7.45, 12.6) * mm});
            skLineSegment(sketch, "E7.1.2.0", {"start": v(-7.45, 29.92) * mm, "end": v(-12.08, 29.92) * mm});
            skLineSegment(sketch, "E7.1.2.1", {"start": v(-12.08, 29.92) * mm, "end": v(-12.08, 25.3) * mm});
            skLineSegment(sketch, "E7.1.2.2", {"start": v(-7.45, 25.3) * mm, "end": v(-12.08, 25.3) * mm});
            skLineSegment(sketch, "E7.1.2.3", {"start": v(-7.45, 29.92) * mm, "end": v(-7.45, 25.3) * mm});
            skLineSegment(sketch, "E7.1.3.0", {"start": v(-7.45, 42.62) * mm, "end": v(-12.08, 42.62) * mm});
            skLineSegment(sketch, "E7.1.3.1", {"start": v(-12.08, 42.62) * mm, "end": v(-12.08, 38) * mm});
            skLineSegment(sketch, "E7.1.3.2", {"start": v(-7.45, 38) * mm, "end": v(-12.08, 38) * mm});
            skLineSegment(sketch, "E7.1.3.3", {"start": v(-7.45, 42.62) * mm, "end": v(-7.45, 38) * mm});
            skLineSegment(sketch, "E7.1.4.0", {"start": v(-7.45, 55.32) * mm, "end": v(-12.08, 55.32) * mm});
            skLineSegment(sketch, "E7.1.4.1", {"start": v(-12.08, 55.32) * mm, "end": v(-12.08, 50.7) * mm});
            skLineSegment(sketch, "E7.1.4.2", {"start": v(-7.45, 50.7) * mm, "end": v(-12.08, 50.7) * mm});
            skLineSegment(sketch, "E7.1.4.3", {"start": v(-7.45, 55.32) * mm, "end": v(-7.45, 50.7) * mm});
            skLineSegment(sketch, "E7.1.5.0", {"start": v(-7.45, 68.02) * mm, "end": v(-12.08, 68.02) * mm});
            skLineSegment(sketch, "E7.1.5.1", {"start": v(-12.08, 68.02) * mm, "end": v(-12.08, 63.4) * mm});
            skLineSegment(sketch, "E7.1.5.2", {"start": v(-7.45, 63.4) * mm, "end": v(-12.08, 63.4) * mm});
            skLineSegment(sketch, "E7.1.5.3", {"start": v(-7.45, 68.02) * mm, "end": v(-7.45, 63.4) * mm});
            skLineSegment(sketch, "E7.1.6.0", {"start": v(-7.45, 80.72) * mm, "end": v(-12.08, 80.72) * mm});
            skLineSegment(sketch, "E7.1.6.1", {"start": v(-12.08, 80.72) * mm, "end": v(-12.08, 76.1) * mm});
            skLineSegment(sketch, "E7.1.6.2", {"start": v(-7.45, 76.1) * mm, "end": v(-12.08, 76.1) * mm});
            skLineSegment(sketch, "E7.1.6.3", {"start": v(-7.45, 80.72) * mm, "end": v(-7.45, 76.1) * mm});
            skLineSegment(sketch, "E7.1.7.0", {"start": v(-7.45, 93.42) * mm, "end": v(-12.08, 93.42) * mm});
            skLineSegment(sketch, "E7.1.7.1", {"start": v(-12.08, 93.42) * mm, "end": v(-12.08, 88.8) * mm});
            skLineSegment(sketch, "E7.1.7.2", {"start": v(-7.45, 88.8) * mm, "end": v(-12.08, 88.8) * mm});
            skLineSegment(sketch, "E7.1.7.3", {"start": v(-7.45, 93.42) * mm, "end": v(-7.45, 88.8) * mm});
            skLineSegment(sketch, "E7.1.8.0", {"start": v(-7.45, 106.12) * mm, "end": v(-12.08, 106.12) * mm});
            skLineSegment(sketch, "E7.1.8.1", {"start": v(-12.08, 106.12) * mm, "end": v(-12.08, 101.5) * mm});
            skLineSegment(sketch, "E7.1.8.2", {"start": v(-7.45, 101.5) * mm, "end": v(-12.08, 101.5) * mm});
            skLineSegment(sketch, "E7.1.8.3", {"start": v(-7.45, 106.12) * mm, "end": v(-7.45, 101.5) * mm});
            skLineSegment(sketch, "E7.1.9.0", {"start": v(-7.45, 118.82) * mm, "end": v(-12.08, 118.82) * mm});
            skLineSegment(sketch, "E7.1.9.1", {"start": v(-12.08, 118.82) * mm, "end": v(-12.08, 114.2) * mm});
            skLineSegment(sketch, "E7.1.9.2", {"start": v(-7.45, 114.2) * mm, "end": v(-12.08, 114.2) * mm});
            skLineSegment(sketch, "E7.1.9.3", {"start": v(-7.45, 118.82) * mm, "end": v(-7.45, 114.2) * mm});
            skLineSegment(sketch, "E7.2.0.0", {"start": v(-20.15, 4.52) * mm, "end": v(-24.78, 4.52) * mm});
            skLineSegment(sketch, "E7.2.0.1", {"start": v(-24.78, 4.52) * mm, "end": v(-24.78, -0.1) * mm});
            skLineSegment(sketch, "E7.2.0.2", {"start": v(-20.15, -0.1) * mm, "end": v(-24.78, -0.1) * mm});
            skLineSegment(sketch, "E7.2.0.3", {"start": v(-20.15, 4.52) * mm, "end": v(-20.15, -0.1) * mm});
            skLineSegment(sketch, "E7.2.1.0", {"start": v(-20.15, 17.22) * mm, "end": v(-24.78, 17.22) * mm});
            skLineSegment(sketch, "E7.2.1.1", {"start": v(-24.78, 17.22) * mm, "end": v(-24.78, 12.6) * mm});
            skLineSegment(sketch, "E7.2.1.2", {"start": v(-20.15, 12.6) * mm, "end": v(-24.78, 12.6) * mm});
            skLineSegment(sketch, "E7.2.1.3", {"start": v(-20.15, 17.22) * mm, "end": v(-20.15, 12.6) * mm});
            skLineSegment(sketch, "E7.2.2.0", {"start": v(-20.15, 29.92) * mm, "end": v(-24.78, 29.92) * mm});
            skLineSegment(sketch, "E7.2.2.1", {"start": v(-24.78, 29.92) * mm, "end": v(-24.78, 25.3) * mm});
            skLineSegment(sketch, "E7.2.2.2", {"start": v(-20.15, 25.3) * mm, "end": v(-24.78, 25.3) * mm});
            skLineSegment(sketch, "E7.2.2.3", {"start": v(-20.15, 29.92) * mm, "end": v(-20.15, 25.3) * mm});
            skLineSegment(sketch, "E7.2.3.0", {"start": v(-20.15, 42.62) * mm, "end": v(-24.78, 42.62) * mm});
            skLineSegment(sketch, "E7.2.3.1", {"start": v(-24.78, 42.62) * mm, "end": v(-24.78, 38) * mm});
            skLineSegment(sketch, "E7.2.3.2", {"start": v(-20.15, 38) * mm, "end": v(-24.78, 38) * mm});
            skLineSegment(sketch, "E7.2.3.3", {"start": v(-20.15, 42.62) * mm, "end": v(-20.15, 38) * mm});
            skLineSegment(sketch, "E7.2.4.0", {"start": v(-20.15, 55.32) * mm, "end": v(-24.78, 55.32) * mm});
            skLineSegment(sketch, "E7.2.4.1", {"start": v(-24.78, 55.32) * mm, "end": v(-24.78, 50.7) * mm});
            skLineSegment(sketch, "E7.2.4.2", {"start": v(-20.15, 50.7) * mm, "end": v(-24.78, 50.7) * mm});
            skLineSegment(sketch, "E7.2.4.3", {"start": v(-20.15, 55.32) * mm, "end": v(-20.15, 50.7) * mm});
            skLineSegment(sketch, "E7.2.5.0", {"start": v(-20.15, 68.02) * mm, "end": v(-24.78, 68.02) * mm});
            skLineSegment(sketch, "E7.2.5.1", {"start": v(-24.78, 68.02) * mm, "end": v(-24.78, 63.4) * mm});
            skLineSegment(sketch, "E7.2.5.2", {"start": v(-20.15, 63.4) * mm, "end": v(-24.78, 63.4) * mm});
            skLineSegment(sketch, "E7.2.5.3", {"start": v(-20.15, 68.02) * mm, "end": v(-20.15, 63.4) * mm});
            skLineSegment(sketch, "E7.2.6.0", {"start": v(-20.15, 80.72) * mm, "end": v(-24.78, 80.72) * mm});
            skLineSegment(sketch, "E7.2.6.1", {"start": v(-24.78, 80.72) * mm, "end": v(-24.78, 76.1) * mm});
            skLineSegment(sketch, "E7.2.6.2", {"start": v(-20.15, 76.1) * mm, "end": v(-24.78, 76.1) * mm});
            skLineSegment(sketch, "E7.2.6.3", {"start": v(-20.15, 80.72) * mm, "end": v(-20.15, 76.1) * mm});
            skLineSegment(sketch, "E7.2.7.0", {"start": v(-20.15, 93.42) * mm, "end": v(-24.78, 93.42) * mm});
            skLineSegment(sketch, "E7.2.7.1", {"start": v(-24.78, 93.42) * mm, "end": v(-24.78, 88.8) * mm});
            skLineSegment(sketch, "E7.2.7.2", {"start": v(-20.15, 88.8) * mm, "end": v(-24.78, 88.8) * mm});
            skLineSegment(sketch, "E7.2.7.3", {"start": v(-20.15, 93.42) * mm, "end": v(-20.15, 88.8) * mm});
            skLineSegment(sketch, "E7.2.8.0", {"start": v(-20.15, 106.12) * mm, "end": v(-24.78, 106.12) * mm});
            skLineSegment(sketch, "E7.2.8.1", {"start": v(-24.78, 106.12) * mm, "end": v(-24.78, 101.5) * mm});
            skLineSegment(sketch, "E7.2.8.2", {"start": v(-20.15, 101.5) * mm, "end": v(-24.78, 101.5) * mm});
            skLineSegment(sketch, "E7.2.8.3", {"start": v(-20.15, 106.12) * mm, "end": v(-20.15, 101.5) * mm});
            skLineSegment(sketch, "E7.2.9.0", {"start": v(-20.15, 118.82) * mm, "end": v(-24.78, 118.82) * mm});
            skLineSegment(sketch, "E7.2.9.1", {"start": v(-24.78, 118.82) * mm, "end": v(-24.78, 114.2) * mm});
            skLineSegment(sketch, "E7.2.9.2", {"start": v(-20.15, 114.2) * mm, "end": v(-24.78, 114.2) * mm});
            skLineSegment(sketch, "E7.2.9.3", {"start": v(-20.15, 118.82) * mm, "end": v(-20.15, 114.2) * mm});
            skLineSegment(sketch, "E7.3.0.0", {"start": v(-32.85, 4.52) * mm, "end": v(-37.48, 4.52) * mm});
            skLineSegment(sketch, "E7.3.0.1", {"start": v(-37.48, 4.52) * mm, "end": v(-37.48, -0.1) * mm});
            skLineSegment(sketch, "E7.3.0.2", {"start": v(-32.85, -0.1) * mm, "end": v(-37.48, -0.1) * mm});
            skLineSegment(sketch, "E7.3.0.3", {"start": v(-32.85, 4.52) * mm, "end": v(-32.85, -0.1) * mm});
            skLineSegment(sketch, "E7.3.1.0", {"start": v(-32.85, 17.22) * mm, "end": v(-37.48, 17.22) * mm});
            skLineSegment(sketch, "E7.3.1.1", {"start": v(-37.48, 17.22) * mm, "end": v(-37.48, 12.6) * mm});
            skLineSegment(sketch, "E7.3.1.2", {"start": v(-32.85, 12.6) * mm, "end": v(-37.48, 12.6) * mm});
            skLineSegment(sketch, "E7.3.1.3", {"start": v(-32.85, 17.22) * mm, "end": v(-32.85, 12.6) * mm});
            skLineSegment(sketch, "E7.3.2.0", {"start": v(-32.85, 29.92) * mm, "end": v(-37.48, 29.92) * mm});
            skLineSegment(sketch, "E7.3.2.1", {"start": v(-37.48, 29.92) * mm, "end": v(-37.48, 25.3) * mm});
            skLineSegment(sketch, "E7.3.2.2", {"start": v(-32.85, 25.3) * mm, "end": v(-37.48, 25.3) * mm});
            skLineSegment(sketch, "E7.3.2.3", {"start": v(-32.85, 29.92) * mm, "end": v(-32.85, 25.3) * mm});
            skLineSegment(sketch, "E7.3.3.0", {"start": v(-32.85, 42.62) * mm, "end": v(-37.48, 42.62) * mm});
            skLineSegment(sketch, "E7.3.3.1", {"start": v(-37.48, 42.62) * mm, "end": v(-37.48, 38) * mm});
            skLineSegment(sketch, "E7.3.3.2", {"start": v(-32.85, 38) * mm, "end": v(-37.48, 38) * mm});
            skLineSegment(sketch, "E7.3.3.3", {"start": v(-32.85, 42.62) * mm, "end": v(-32.85, 38) * mm});
            skLineSegment(sketch, "E7.3.4.0", {"start": v(-32.85, 55.32) * mm, "end": v(-37.48, 55.32) * mm});
            skLineSegment(sketch, "E7.3.4.1", {"start": v(-37.48, 55.32) * mm, "end": v(-37.48, 50.7) * mm});
            skLineSegment(sketch, "E7.3.4.2", {"start": v(-32.85, 50.7) * mm, "end": v(-37.48, 50.7) * mm});
            skLineSegment(sketch, "E7.3.4.3", {"start": v(-32.85, 55.32) * mm, "end": v(-32.85, 50.7) * mm});
            skLineSegment(sketch, "E7.3.5.0", {"start": v(-32.85, 68.02) * mm, "end": v(-37.48, 68.02) * mm});
            skLineSegment(sketch, "E7.3.5.1", {"start": v(-37.48, 68.02) * mm, "end": v(-37.48, 63.4) * mm});
            skLineSegment(sketch, "E7.3.5.2", {"start": v(-32.85, 63.4) * mm, "end": v(-37.48, 63.4) * mm});
            skLineSegment(sketch, "E7.3.5.3", {"start": v(-32.85, 68.02) * mm, "end": v(-32.85, 63.4) * mm});
            skLineSegment(sketch, "E7.3.6.0", {"start": v(-32.85, 80.72) * mm, "end": v(-37.48, 80.72) * mm});
            skLineSegment(sketch, "E7.3.6.1", {"start": v(-37.48, 80.72) * mm, "end": v(-37.48, 76.1) * mm});
            skLineSegment(sketch, "E7.3.6.2", {"start": v(-32.85, 76.1) * mm, "end": v(-37.48, 76.1) * mm});
            skLineSegment(sketch, "E7.3.6.3", {"start": v(-32.85, 80.72) * mm, "end": v(-32.85, 76.1) * mm});
            skLineSegment(sketch, "E7.3.7.0", {"start": v(-32.85, 93.42) * mm, "end": v(-37.48, 93.42) * mm});
            skLineSegment(sketch, "E7.3.7.1", {"start": v(-37.48, 93.42) * mm, "end": v(-37.48, 88.8) * mm});
            skLineSegment(sketch, "E7.3.7.2", {"start": v(-32.85, 88.8) * mm, "end": v(-37.48, 88.8) * mm});
            skLineSegment(sketch, "E7.3.7.3", {"start": v(-32.85, 93.42) * mm, "end": v(-32.85, 88.8) * mm});
            skLineSegment(sketch, "E7.3.8.0", {"start": v(-32.85, 106.12) * mm, "end": v(-37.48, 106.12) * mm});
            skLineSegment(sketch, "E7.3.8.1", {"start": v(-37.48, 106.12) * mm, "end": v(-37.48, 101.5) * mm});
            skLineSegment(sketch, "E7.3.8.2", {"start": v(-32.85, 101.5) * mm, "end": v(-37.48, 101.5) * mm});
            skLineSegment(sketch, "E7.3.8.3", {"start": v(-32.85, 106.12) * mm, "end": v(-32.85, 101.5) * mm});
            skLineSegment(sketch, "E7.3.9.0", {"start": v(-32.85, 118.82) * mm, "end": v(-37.48, 118.82) * mm});
            skLineSegment(sketch, "E7.3.9.1", {"start": v(-37.48, 118.82) * mm, "end": v(-37.48, 114.2) * mm});
            skLineSegment(sketch, "E7.3.9.2", {"start": v(-32.85, 114.2) * mm, "end": v(-37.48, 114.2) * mm});
            skLineSegment(sketch, "E7.3.9.3", {"start": v(-32.85, 118.82) * mm, "end": v(-32.85, 114.2) * mm});
            skLineSegment(sketch, "E7.4.0.0", {"start": v(-45.55, 4.52) * mm, "end": v(-50.18, 4.52) * mm});
            skLineSegment(sketch, "E7.4.0.1", {"start": v(-50.18, 4.52) * mm, "end": v(-50.18, -0.1) * mm});
            skLineSegment(sketch, "E7.4.0.2", {"start": v(-45.55, -0.1) * mm, "end": v(-50.18, -0.1) * mm});
            skLineSegment(sketch, "E7.4.0.3", {"start": v(-45.55, 4.52) * mm, "end": v(-45.55, -0.1) * mm});
            skLineSegment(sketch, "E7.4.1.0", {"start": v(-45.55, 17.22) * mm, "end": v(-50.18, 17.22) * mm});
            skLineSegment(sketch, "E7.4.1.1", {"start": v(-50.18, 17.22) * mm, "end": v(-50.18, 12.6) * mm});
            skLineSegment(sketch, "E7.4.1.2", {"start": v(-45.55, 12.6) * mm, "end": v(-50.18, 12.6) * mm});
            skLineSegment(sketch, "E7.4.1.3", {"start": v(-45.55, 17.22) * mm, "end": v(-45.55, 12.6) * mm});
            skLineSegment(sketch, "E7.4.2.0", {"start": v(-45.55, 29.92) * mm, "end": v(-50.18, 29.92) * mm});
            skLineSegment(sketch, "E7.4.2.1", {"start": v(-50.18, 29.92) * mm, "end": v(-50.18, 25.3) * mm});
            skLineSegment(sketch, "E7.4.2.2", {"start": v(-45.55, 25.3) * mm, "end": v(-50.18, 25.3) * mm});
            skLineSegment(sketch, "E7.4.2.3", {"start": v(-45.55, 29.92) * mm, "end": v(-45.55, 25.3) * mm});
            skLineSegment(sketch, "E7.4.3.0", {"start": v(-45.55, 42.62) * mm, "end": v(-50.18, 42.62) * mm});
            skLineSegment(sketch, "E7.4.3.1", {"start": v(-50.18, 42.62) * mm, "end": v(-50.18, 38) * mm});
            skLineSegment(sketch, "E7.4.3.2", {"start": v(-45.55, 38) * mm, "end": v(-50.18, 38) * mm});
            skLineSegment(sketch, "E7.4.3.3", {"start": v(-45.55, 42.62) * mm, "end": v(-45.55, 38) * mm});
            skLineSegment(sketch, "E7.4.4.0", {"start": v(-45.55, 55.32) * mm, "end": v(-50.18, 55.32) * mm});
            skLineSegment(sketch, "E7.4.4.1", {"start": v(-50.18, 55.32) * mm, "end": v(-50.18, 50.7) * mm});
            skLineSegment(sketch, "E7.4.4.2", {"start": v(-45.55, 50.7) * mm, "end": v(-50.18, 50.7) * mm});
            skLineSegment(sketch, "E7.4.4.3", {"start": v(-45.55, 55.32) * mm, "end": v(-45.55, 50.7) * mm});
            skLineSegment(sketch, "E7.4.5.0", {"start": v(-45.55, 68.02) * mm, "end": v(-50.18, 68.02) * mm});
            skLineSegment(sketch, "E7.4.5.1", {"start": v(-50.18, 68.02) * mm, "end": v(-50.18, 63.4) * mm});
            skLineSegment(sketch, "E7.4.5.2", {"start": v(-45.55, 63.4) * mm, "end": v(-50.18, 63.4) * mm});
            skLineSegment(sketch, "E7.4.5.3", {"start": v(-45.55, 68.02) * mm, "end": v(-45.55, 63.4) * mm});
            skLineSegment(sketch, "E7.4.6.0", {"start": v(-45.55, 80.72) * mm, "end": v(-50.18, 80.72) * mm});
            skLineSegment(sketch, "E7.4.6.1", {"start": v(-50.18, 80.72) * mm, "end": v(-50.18, 76.1) * mm});
            skLineSegment(sketch, "E7.4.6.2", {"start": v(-45.55, 76.1) * mm, "end": v(-50.18, 76.1) * mm});
            skLineSegment(sketch, "E7.4.6.3", {"start": v(-45.55, 80.72) * mm, "end": v(-45.55, 76.1) * mm});
            skLineSegment(sketch, "E7.4.7.0", {"start": v(-45.55, 93.42) * mm, "end": v(-50.18, 93.42) * mm});
            skLineSegment(sketch, "E7.4.7.1", {"start": v(-50.18, 93.42) * mm, "end": v(-50.18, 88.8) * mm});
            skLineSegment(sketch, "E7.4.7.2", {"start": v(-45.55, 88.8) * mm, "end": v(-50.18, 88.8) * mm});
            skLineSegment(sketch, "E7.4.7.3", {"start": v(-45.55, 93.42) * mm, "end": v(-45.55, 88.8) * mm});
            skLineSegment(sketch, "E7.4.8.0", {"start": v(-45.55, 106.12) * mm, "end": v(-50.18, 106.12) * mm});
            skLineSegment(sketch, "E7.4.8.1", {"start": v(-50.18, 106.12) * mm, "end": v(-50.18, 101.5) * mm});
            skLineSegment(sketch, "E7.4.8.2", {"start": v(-45.55, 101.5) * mm, "end": v(-50.18, 101.5) * mm});
            skLineSegment(sketch, "E7.4.8.3", {"start": v(-45.55, 106.12) * mm, "end": v(-45.55, 101.5) * mm});
            skLineSegment(sketch, "E7.4.9.0", {"start": v(-45.55, 118.82) * mm, "end": v(-50.18, 118.82) * mm});
            skLineSegment(sketch, "E7.4.9.1", {"start": v(-50.18, 118.82) * mm, "end": v(-50.18, 114.2) * mm});
            skLineSegment(sketch, "E7.4.9.2", {"start": v(-45.55, 114.2) * mm, "end": v(-50.18, 114.2) * mm});
            skLineSegment(sketch, "E7.4.9.3", {"start": v(-45.55, 118.82) * mm, "end": v(-45.55, 114.2) * mm});
            skLineSegment(sketch, "E7.5.0.0", {"start": v(-58.25, 4.52) * mm, "end": v(-62.88, 4.52) * mm});
            skLineSegment(sketch, "E7.5.0.1", {"start": v(-62.88, 4.52) * mm, "end": v(-62.88, -0.1) * mm});
            skLineSegment(sketch, "E7.5.0.2", {"start": v(-58.25, -0.1) * mm, "end": v(-62.88, -0.1) * mm});
            skLineSegment(sketch, "E7.5.0.3", {"start": v(-58.25, 4.52) * mm, "end": v(-58.25, -0.1) * mm});
            skLineSegment(sketch, "E7.5.1.0", {"start": v(-58.25, 17.22) * mm, "end": v(-62.88, 17.22) * mm});
            skLineSegment(sketch, "E7.5.1.1", {"start": v(-62.88, 17.22) * mm, "end": v(-62.88, 12.6) * mm});
            skLineSegment(sketch, "E7.5.1.2", {"start": v(-58.25, 12.6) * mm, "end": v(-62.88, 12.6) * mm});
            skLineSegment(sketch, "E7.5.1.3", {"start": v(-58.25, 17.22) * mm, "end": v(-58.25, 12.6) * mm});
            skLineSegment(sketch, "E7.5.2.0", {"start": v(-58.25, 29.92) * mm, "end": v(-62.88, 29.92) * mm});
            skLineSegment(sketch, "E7.5.2.1", {"start": v(-62.88, 29.92) * mm, "end": v(-62.88, 25.3) * mm});
            skLineSegment(sketch, "E7.5.2.2", {"start": v(-58.25, 25.3) * mm, "end": v(-62.88, 25.3) * mm});
            skLineSegment(sketch, "E7.5.2.3", {"start": v(-58.25, 29.92) * mm, "end": v(-58.25, 25.3) * mm});
            skLineSegment(sketch, "E7.5.3.0", {"start": v(-58.25, 42.62) * mm, "end": v(-62.88, 42.62) * mm});
            skLineSegment(sketch, "E7.5.3.1", {"start": v(-62.88, 42.62) * mm, "end": v(-62.88, 38) * mm});
            skLineSegment(sketch, "E7.5.3.2", {"start": v(-58.25, 38) * mm, "end": v(-62.88, 38) * mm});
            skLineSegment(sketch, "E7.5.3.3", {"start": v(-58.25, 42.62) * mm, "end": v(-58.25, 38) * mm});
            skLineSegment(sketch, "E7.5.4.0", {"start": v(-58.25, 55.32) * mm, "end": v(-62.88, 55.32) * mm});
            skLineSegment(sketch, "E7.5.4.1", {"start": v(-62.88, 55.32) * mm, "end": v(-62.88, 50.7) * mm});
            skLineSegment(sketch, "E7.5.4.2", {"start": v(-58.25, 50.7) * mm, "end": v(-62.88, 50.7) * mm});
            skLineSegment(sketch, "E7.5.4.3", {"start": v(-58.25, 55.32) * mm, "end": v(-58.25, 50.7) * mm});
            skLineSegment(sketch, "E7.5.5.0", {"start": v(-58.25, 68.02) * mm, "end": v(-62.88, 68.02) * mm});
            skLineSegment(sketch, "E7.5.5.1", {"start": v(-62.88, 68.02) * mm, "end": v(-62.88, 63.4) * mm});
            skLineSegment(sketch, "E7.5.5.2", {"start": v(-58.25, 63.4) * mm, "end": v(-62.88, 63.4) * mm});
            skLineSegment(sketch, "E7.5.5.3", {"start": v(-58.25, 68.02) * mm, "end": v(-58.25, 63.4) * mm});
            skLineSegment(sketch, "E7.5.6.0", {"start": v(-58.25, 80.72) * mm, "end": v(-62.88, 80.72) * mm});
            skLineSegment(sketch, "E7.5.6.1", {"start": v(-62.88, 80.72) * mm, "end": v(-62.88, 76.1) * mm});
            skLineSegment(sketch, "E7.5.6.2", {"start": v(-58.25, 76.1) * mm, "end": v(-62.88, 76.1) * mm});
            skLineSegment(sketch, "E7.5.6.3", {"start": v(-58.25, 80.72) * mm, "end": v(-58.25, 76.1) * mm});
            skLineSegment(sketch, "E7.5.7.0", {"start": v(-58.25, 93.42) * mm, "end": v(-62.88, 93.42) * mm});
            skLineSegment(sketch, "E7.5.7.1", {"start": v(-62.88, 93.42) * mm, "end": v(-62.88, 88.8) * mm});
            skLineSegment(sketch, "E7.5.7.2", {"start": v(-58.25, 88.8) * mm, "end": v(-62.88, 88.8) * mm});
            skLineSegment(sketch, "E7.5.7.3", {"start": v(-58.25, 93.42) * mm, "end": v(-58.25, 88.8) * mm});
            skLineSegment(sketch, "E7.5.8.0", {"start": v(-58.25, 106.12) * mm, "end": v(-62.88, 106.12) * mm});
            skLineSegment(sketch, "E7.5.8.1", {"start": v(-62.88, 106.12) * mm, "end": v(-62.88, 101.5) * mm});
            skLineSegment(sketch, "E7.5.8.2", {"start": v(-58.25, 101.5) * mm, "end": v(-62.88, 101.5) * mm});
            skLineSegment(sketch, "E7.5.8.3", {"start": v(-58.25, 106.12) * mm, "end": v(-58.25, 101.5) * mm});
            skLineSegment(sketch, "E7.5.9.0", {"start": v(-58.25, 118.82) * mm, "end": v(-62.88, 118.82) * mm});
            skLineSegment(sketch, "E7.5.9.1", {"start": v(-62.88, 118.82) * mm, "end": v(-62.88, 114.2) * mm});
            skLineSegment(sketch, "E7.5.9.2", {"start": v(-58.25, 114.2) * mm, "end": v(-62.88, 114.2) * mm});
            skLineSegment(sketch, "E7.5.9.3", {"start": v(-58.25, 118.82) * mm, "end": v(-58.25, 114.2) * mm});
            skLineSegment(sketch, "E7.6.0.0", {"start": v(-70.95, 4.52) * mm, "end": v(-75.58, 4.52) * mm});
            skLineSegment(sketch, "E7.6.0.1", {"start": v(-75.58, 4.52) * mm, "end": v(-75.58, -0.1) * mm});
            skLineSegment(sketch, "E7.6.0.2", {"start": v(-70.95, -0.1) * mm, "end": v(-75.58, -0.1) * mm});
            skLineSegment(sketch, "E7.6.0.3", {"start": v(-70.95, 4.52) * mm, "end": v(-70.95, -0.1) * mm});
            skLineSegment(sketch, "E7.6.1.0", {"start": v(-70.95, 17.22) * mm, "end": v(-75.58, 17.22) * mm});
            skLineSegment(sketch, "E7.6.1.1", {"start": v(-75.58, 17.22) * mm, "end": v(-75.58, 12.6) * mm});
            skLineSegment(sketch, "E7.6.1.2", {"start": v(-70.95, 12.6) * mm, "end": v(-75.58, 12.6) * mm});
            skLineSegment(sketch, "E7.6.1.3", {"start": v(-70.95, 17.22) * mm, "end": v(-70.95, 12.6) * mm});
            skLineSegment(sketch, "E7.6.2.0", {"start": v(-70.95, 29.92) * mm, "end": v(-75.58, 29.92) * mm});
            skLineSegment(sketch, "E7.6.2.1", {"start": v(-75.58, 29.92) * mm, "end": v(-75.58, 25.3) * mm});
            skLineSegment(sketch, "E7.6.2.2", {"start": v(-70.95, 25.3) * mm, "end": v(-75.58, 25.3) * mm});
            skLineSegment(sketch, "E7.6.2.3", {"start": v(-70.95, 29.92) * mm, "end": v(-70.95, 25.3) * mm});
            skLineSegment(sketch, "E7.6.3.0", {"start": v(-70.95, 42.62) * mm, "end": v(-75.58, 42.62) * mm});
            skLineSegment(sketch, "E7.6.3.1", {"start": v(-75.58, 42.62) * mm, "end": v(-75.58, 38) * mm});
            skLineSegment(sketch, "E7.6.3.2", {"start": v(-70.95, 38) * mm, "end": v(-75.58, 38) * mm});
            skLineSegment(sketch, "E7.6.3.3", {"start": v(-70.95, 42.62) * mm, "end": v(-70.95, 38) * mm});
            skLineSegment(sketch, "E7.6.4.0", {"start": v(-70.95, 55.32) * mm, "end": v(-75.58, 55.32) * mm});
            skLineSegment(sketch, "E7.6.4.1", {"start": v(-75.58, 55.32) * mm, "end": v(-75.58, 50.7) * mm});
            skLineSegment(sketch, "E7.6.4.2", {"start": v(-70.95, 50.7) * mm, "end": v(-75.58, 50.7) * mm});
            skLineSegment(sketch, "E7.6.4.3", {"start": v(-70.95, 55.32) * mm, "end": v(-70.95, 50.7) * mm});
            skLineSegment(sketch, "E7.6.5.0", {"start": v(-70.95, 68.02) * mm, "end": v(-75.58, 68.02) * mm});
            skLineSegment(sketch, "E7.6.5.1", {"start": v(-75.58, 68.02) * mm, "end": v(-75.58, 63.4) * mm});
            skLineSegment(sketch, "E7.6.5.2", {"start": v(-70.95, 63.4) * mm, "end": v(-75.58, 63.4) * mm});
            skLineSegment(sketch, "E7.6.5.3", {"start": v(-70.95, 68.02) * mm, "end": v(-70.95, 63.4) * mm});
            skLineSegment(sketch, "E7.6.6.0", {"start": v(-70.95, 80.72) * mm, "end": v(-75.58, 80.72) * mm});
            skLineSegment(sketch, "E7.6.6.1", {"start": v(-75.58, 80.72) * mm, "end": v(-75.58, 76.1) * mm});
            skLineSegment(sketch, "E7.6.6.2", {"start": v(-70.95, 76.1) * mm, "end": v(-75.58, 76.1) * mm});
            skLineSegment(sketch, "E7.6.6.3", {"start": v(-70.95, 80.72) * mm, "end": v(-70.95, 76.1) * mm});
            skLineSegment(sketch, "E7.6.7.0", {"start": v(-70.95, 93.42) * mm, "end": v(-75.58, 93.42) * mm});
            skLineSegment(sketch, "E7.6.7.1", {"start": v(-75.58, 93.42) * mm, "end": v(-75.58, 88.8) * mm});
            skLineSegment(sketch, "E7.6.7.2", {"start": v(-70.95, 88.8) * mm, "end": v(-75.58, 88.8) * mm});
            skLineSegment(sketch, "E7.6.7.3", {"start": v(-70.95, 93.42) * mm, "end": v(-70.95, 88.8) * mm});
            skLineSegment(sketch, "E7.6.8.0", {"start": v(-70.95, 106.12) * mm, "end": v(-75.58, 106.12) * mm});
            skLineSegment(sketch, "E7.6.8.1", {"start": v(-75.58, 106.12) * mm, "end": v(-75.58, 101.5) * mm});
            skLineSegment(sketch, "E7.6.8.2", {"start": v(-70.95, 101.5) * mm, "end": v(-75.58, 101.5) * mm});
            skLineSegment(sketch, "E7.6.8.3", {"start": v(-70.95, 106.12) * mm, "end": v(-70.95, 101.5) * mm});
            skLineSegment(sketch, "E7.6.9.0", {"start": v(-70.95, 118.82) * mm, "end": v(-75.58, 118.82) * mm});
            skLineSegment(sketch, "E7.6.9.1", {"start": v(-75.58, 118.82) * mm, "end": v(-75.58, 114.2) * mm});
            skLineSegment(sketch, "E7.6.9.2", {"start": v(-70.95, 114.2) * mm, "end": v(-75.58, 114.2) * mm});
            skLineSegment(sketch, "E7.6.9.3", {"start": v(-70.95, 118.82) * mm, "end": v(-70.95, 114.2) * mm});
            skLineSegment(sketch, "E7.7.0.0", {"start": v(-83.65, 4.52) * mm, "end": v(-88.28, 4.52) * mm});
            skLineSegment(sketch, "E7.7.0.1", {"start": v(-88.28, 4.52) * mm, "end": v(-88.28, -0.1) * mm});
            skLineSegment(sketch, "E7.7.0.2", {"start": v(-83.65, -0.1) * mm, "end": v(-88.28, -0.1) * mm});
            skLineSegment(sketch, "E7.7.0.3", {"start": v(-83.65, 4.52) * mm, "end": v(-83.65, -0.1) * mm});
            skLineSegment(sketch, "E7.7.1.0", {"start": v(-83.65, 17.22) * mm, "end": v(-88.28, 17.22) * mm});
            skLineSegment(sketch, "E7.7.1.1", {"start": v(-88.28, 17.22) * mm, "end": v(-88.28, 12.6) * mm});
            skLineSegment(sketch, "E7.7.1.2", {"start": v(-83.65, 12.6) * mm, "end": v(-88.28, 12.6) * mm});
            skLineSegment(sketch, "E7.7.1.3", {"start": v(-83.65, 17.22) * mm, "end": v(-83.65, 12.6) * mm});
            skLineSegment(sketch, "E7.7.2.0", {"start": v(-83.65, 29.92) * mm, "end": v(-88.28, 29.92) * mm});
            skLineSegment(sketch, "E7.7.2.1", {"start": v(-88.28, 29.92) * mm, "end": v(-88.28, 25.3) * mm});
            skLineSegment(sketch, "E7.7.2.2", {"start": v(-83.65, 25.3) * mm, "end": v(-88.28, 25.3) * mm});
            skLineSegment(sketch, "E7.7.2.3", {"start": v(-83.65, 29.92) * mm, "end": v(-83.65, 25.3) * mm});
            skLineSegment(sketch, "E7.7.3.0", {"start": v(-83.65, 42.62) * mm, "end": v(-88.28, 42.62) * mm});
            skLineSegment(sketch, "E7.7.3.1", {"start": v(-88.28, 42.62) * mm, "end": v(-88.28, 38) * mm});
            skLineSegment(sketch, "E7.7.3.2", {"start": v(-83.65, 38) * mm, "end": v(-88.28, 38) * mm});
            skLineSegment(sketch, "E7.7.3.3", {"start": v(-83.65, 42.62) * mm, "end": v(-83.65, 38) * mm});
            skLineSegment(sketch, "E7.7.4.0", {"start": v(-83.65, 55.32) * mm, "end": v(-88.28, 55.32) * mm});
            skLineSegment(sketch, "E7.7.4.1", {"start": v(-88.28, 55.32) * mm, "end": v(-88.28, 50.7) * mm});
            skLineSegment(sketch, "E7.7.4.2", {"start": v(-83.65, 50.7) * mm, "end": v(-88.28, 50.7) * mm});
            skLineSegment(sketch, "E7.7.4.3", {"start": v(-83.65, 55.32) * mm, "end": v(-83.65, 50.7) * mm});
            skLineSegment(sketch, "E7.7.5.0", {"start": v(-83.65, 68.02) * mm, "end": v(-88.28, 68.02) * mm});
            skLineSegment(sketch, "E7.7.5.1", {"start": v(-88.28, 68.02) * mm, "end": v(-88.28, 63.4) * mm});
            skLineSegment(sketch, "E7.7.5.2", {"start": v(-83.65, 63.4) * mm, "end": v(-88.28, 63.4) * mm});
            skLineSegment(sketch, "E7.7.5.3", {"start": v(-83.65, 68.02) * mm, "end": v(-83.65, 63.4) * mm});
            skLineSegment(sketch, "E7.7.6.0", {"start": v(-83.65, 80.72) * mm, "end": v(-88.28, 80.72) * mm});
            skLineSegment(sketch, "E7.7.6.1", {"start": v(-88.28, 80.72) * mm, "end": v(-88.28, 76.1) * mm});
            skLineSegment(sketch, "E7.7.6.2", {"start": v(-83.65, 76.1) * mm, "end": v(-88.28, 76.1) * mm});
            skLineSegment(sketch, "E7.7.6.3", {"start": v(-83.65, 80.72) * mm, "end": v(-83.65, 76.1) * mm});
            skLineSegment(sketch, "E7.7.7.0", {"start": v(-83.65, 93.42) * mm, "end": v(-88.28, 93.42) * mm});
            skLineSegment(sketch, "E7.7.7.1", {"start": v(-88.28, 93.42) * mm, "end": v(-88.28, 88.8) * mm});
            skLineSegment(sketch, "E7.7.7.2", {"start": v(-83.65, 88.8) * mm, "end": v(-88.28, 88.8) * mm});
            skLineSegment(sketch, "E7.7.7.3", {"start": v(-83.65, 93.42) * mm, "end": v(-83.65, 88.8) * mm});
            skLineSegment(sketch, "E7.7.8.0", {"start": v(-83.65, 106.12) * mm, "end": v(-88.28, 106.12) * mm});
            skLineSegment(sketch, "E7.7.8.1", {"start": v(-88.28, 106.12) * mm, "end": v(-88.28, 101.5) * mm});
            skLineSegment(sketch, "E7.7.8.2", {"start": v(-83.65, 101.5) * mm, "end": v(-88.28, 101.5) * mm});
            skLineSegment(sketch, "E7.7.8.3", {"start": v(-83.65, 106.12) * mm, "end": v(-83.65, 101.5) * mm});
            skLineSegment(sketch, "E7.7.9.0", {"start": v(-83.65, 118.82) * mm, "end": v(-88.28, 118.82) * mm});
            skLineSegment(sketch, "E7.7.9.1", {"start": v(-88.28, 118.82) * mm, "end": v(-88.28, 114.2) * mm});
            skLineSegment(sketch, "E7.7.9.2", {"start": v(-83.65, 114.2) * mm, "end": v(-88.28, 114.2) * mm});
            skLineSegment(sketch, "E7.7.9.3", {"start": v(-83.65, 118.82) * mm, "end": v(-83.65, 114.2) * mm});
            skLineSegment(sketch, "E7.8.0.0", {"start": v(-96.35, 4.52) * mm, "end": v(-100.98, 4.52) * mm});
            skLineSegment(sketch, "E7.8.0.1", {"start": v(-100.98, 4.52) * mm, "end": v(-100.98, -0.1) * mm});
            skLineSegment(sketch, "E7.8.0.2", {"start": v(-96.35, -0.1) * mm, "end": v(-100.98, -0.1) * mm});
            skLineSegment(sketch, "E7.8.0.3", {"start": v(-96.35, 4.52) * mm, "end": v(-96.35, -0.1) * mm});
            skLineSegment(sketch, "E7.8.1.0", {"start": v(-96.35, 17.22) * mm, "end": v(-100.98, 17.22) * mm});
            skLineSegment(sketch, "E7.8.1.1", {"start": v(-100.98, 17.22) * mm, "end": v(-100.98, 12.6) * mm});
            skLineSegment(sketch, "E7.8.1.2", {"start": v(-96.35, 12.6) * mm, "end": v(-100.98, 12.6) * mm});
            skLineSegment(sketch, "E7.8.1.3", {"start": v(-96.35, 17.22) * mm, "end": v(-96.35, 12.6) * mm});
            skLineSegment(sketch, "E7.8.2.0", {"start": v(-96.35, 29.92) * mm, "end": v(-100.98, 29.92) * mm});
            skLineSegment(sketch, "E7.8.2.1", {"start": v(-100.98, 29.92) * mm, "end": v(-100.98, 25.3) * mm});
            skLineSegment(sketch, "E7.8.2.2", {"start": v(-96.35, 25.3) * mm, "end": v(-100.98, 25.3) * mm});
            skLineSegment(sketch, "E7.8.2.3", {"start": v(-96.35, 29.92) * mm, "end": v(-96.35, 25.3) * mm});
            skLineSegment(sketch, "E7.8.3.0", {"start": v(-96.35, 42.62) * mm, "end": v(-100.98, 42.62) * mm});
            skLineSegment(sketch, "E7.8.3.1", {"start": v(-100.98, 42.62) * mm, "end": v(-100.98, 38) * mm});
            skLineSegment(sketch, "E7.8.3.2", {"start": v(-96.35, 38) * mm, "end": v(-100.98, 38) * mm});
            skLineSegment(sketch, "E7.8.3.3", {"start": v(-96.35, 42.62) * mm, "end": v(-96.35, 38) * mm});
            skLineSegment(sketch, "E7.8.4.0", {"start": v(-96.35, 55.32) * mm, "end": v(-100.98, 55.32) * mm});
            skLineSegment(sketch, "E7.8.4.1", {"start": v(-100.98, 55.32) * mm, "end": v(-100.98, 50.7) * mm});
            skLineSegment(sketch, "E7.8.4.2", {"start": v(-96.35, 50.7) * mm, "end": v(-100.98, 50.7) * mm});
            skLineSegment(sketch, "E7.8.4.3", {"start": v(-96.35, 55.32) * mm, "end": v(-96.35, 50.7) * mm});
            skLineSegment(sketch, "E7.8.5.0", {"start": v(-96.35, 68.02) * mm, "end": v(-100.98, 68.02) * mm});
            skLineSegment(sketch, "E7.8.5.1", {"start": v(-100.98, 68.02) * mm, "end": v(-100.98, 63.4) * mm});
            skLineSegment(sketch, "E7.8.5.2", {"start": v(-96.35, 63.4) * mm, "end": v(-100.98, 63.4) * mm});
            skLineSegment(sketch, "E7.8.5.3", {"start": v(-96.35, 68.02) * mm, "end": v(-96.35, 63.4) * mm});
            skLineSegment(sketch, "E7.8.6.0", {"start": v(-96.35, 80.72) * mm, "end": v(-100.98, 80.72) * mm});
            skLineSegment(sketch, "E7.8.6.1", {"start": v(-100.98, 80.72) * mm, "end": v(-100.98, 76.1) * mm});
            skLineSegment(sketch, "E7.8.6.2", {"start": v(-96.35, 76.1) * mm, "end": v(-100.98, 76.1) * mm});
            skLineSegment(sketch, "E7.8.6.3", {"start": v(-96.35, 80.72) * mm, "end": v(-96.35, 76.1) * mm});
            skLineSegment(sketch, "E7.8.7.0", {"start": v(-96.35, 93.42) * mm, "end": v(-100.98, 93.42) * mm});
            skLineSegment(sketch, "E7.8.7.1", {"start": v(-100.98, 93.42) * mm, "end": v(-100.98, 88.8) * mm});
            skLineSegment(sketch, "E7.8.7.2", {"start": v(-96.35, 88.8) * mm, "end": v(-100.98, 88.8) * mm});
            skLineSegment(sketch, "E7.8.7.3", {"start": v(-96.35, 93.42) * mm, "end": v(-96.35, 88.8) * mm});
            skLineSegment(sketch, "E7.8.8.0", {"start": v(-96.35, 106.12) * mm, "end": v(-100.98, 106.12) * mm});
            skLineSegment(sketch, "E7.8.8.1", {"start": v(-100.98, 106.12) * mm, "end": v(-100.98, 101.5) * mm});
            skLineSegment(sketch, "E7.8.8.2", {"start": v(-96.35, 101.5) * mm, "end": v(-100.98, 101.5) * mm});
            skLineSegment(sketch, "E7.8.8.3", {"start": v(-96.35, 106.12) * mm, "end": v(-96.35, 101.5) * mm});
            skLineSegment(sketch, "E7.8.9.0", {"start": v(-96.35, 118.82) * mm, "end": v(-100.98, 118.82) * mm});
            skLineSegment(sketch, "E7.8.9.1", {"start": v(-100.98, 118.82) * mm, "end": v(-100.98, 114.2) * mm});
            skLineSegment(sketch, "E7.8.9.2", {"start": v(-96.35, 114.2) * mm, "end": v(-100.98, 114.2) * mm});
            skLineSegment(sketch, "E7.8.9.3", {"start": v(-96.35, 118.82) * mm, "end": v(-96.35, 114.2) * mm});
            skLineSegment(sketch, "E7.9.0.0", {"start": v(-109.05, 4.52) * mm, "end": v(-113.68, 4.52) * mm});
            skLineSegment(sketch, "E7.9.0.1", {"start": v(-113.68, 4.52) * mm, "end": v(-113.68, -0.1) * mm});
            skLineSegment(sketch, "E7.9.0.2", {"start": v(-109.05, -0.1) * mm, "end": v(-113.68, -0.1) * mm});
            skLineSegment(sketch, "E7.9.0.3", {"start": v(-109.05, 4.52) * mm, "end": v(-109.05, -0.1) * mm});
            skLineSegment(sketch, "E7.9.1.0", {"start": v(-109.05, 17.22) * mm, "end": v(-113.68, 17.22) * mm});
            skLineSegment(sketch, "E7.9.1.1", {"start": v(-113.68, 17.22) * mm, "end": v(-113.68, 12.6) * mm});
            skLineSegment(sketch, "E7.9.1.2", {"start": v(-109.05, 12.6) * mm, "end": v(-113.68, 12.6) * mm});
            skLineSegment(sketch, "E7.9.1.3", {"start": v(-109.05, 17.22) * mm, "end": v(-109.05, 12.6) * mm});
            skLineSegment(sketch, "E7.9.2.0", {"start": v(-109.05, 29.92) * mm, "end": v(-113.68, 29.92) * mm});
            skLineSegment(sketch, "E7.9.2.1", {"start": v(-113.68, 29.92) * mm, "end": v(-113.68, 25.3) * mm});
            skLineSegment(sketch, "E7.9.2.2", {"start": v(-109.05, 25.3) * mm, "end": v(-113.68, 25.3) * mm});
            skLineSegment(sketch, "E7.9.2.3", {"start": v(-109.05, 29.92) * mm, "end": v(-109.05, 25.3) * mm});
            skLineSegment(sketch, "E7.9.3.0", {"start": v(-109.05, 42.62) * mm, "end": v(-113.68, 42.62) * mm});
            skLineSegment(sketch, "E7.9.3.1", {"start": v(-113.68, 42.62) * mm, "end": v(-113.68, 38) * mm});
            skLineSegment(sketch, "E7.9.3.2", {"start": v(-109.05, 38) * mm, "end": v(-113.68, 38) * mm});
            skLineSegment(sketch, "E7.9.3.3", {"start": v(-109.05, 42.62) * mm, "end": v(-109.05, 38) * mm});
            skLineSegment(sketch, "E7.9.4.0", {"start": v(-109.05, 55.32) * mm, "end": v(-113.68, 55.32) * mm});
            skLineSegment(sketch, "E7.9.4.1", {"start": v(-113.68, 55.32) * mm, "end": v(-113.68, 50.7) * mm});
            skLineSegment(sketch, "E7.9.4.2", {"start": v(-109.05, 50.7) * mm, "end": v(-113.68, 50.7) * mm});
            skLineSegment(sketch, "E7.9.4.3", {"start": v(-109.05, 55.32) * mm, "end": v(-109.05, 50.7) * mm});
            skLineSegment(sketch, "E7.9.5.0", {"start": v(-109.05, 68.02) * mm, "end": v(-113.68, 68.02) * mm});
            skLineSegment(sketch, "E7.9.5.1", {"start": v(-113.68, 68.02) * mm, "end": v(-113.68, 63.4) * mm});
            skLineSegment(sketch, "E7.9.5.2", {"start": v(-109.05, 63.4) * mm, "end": v(-113.68, 63.4) * mm});
            skLineSegment(sketch, "E7.9.5.3", {"start": v(-109.05, 68.02) * mm, "end": v(-109.05, 63.4) * mm});
            skLineSegment(sketch, "E7.9.6.0", {"start": v(-109.05, 80.72) * mm, "end": v(-113.68, 80.72) * mm});
            skLineSegment(sketch, "E7.9.6.1", {"start": v(-113.68, 80.72) * mm, "end": v(-113.68, 76.1) * mm});
            skLineSegment(sketch, "E7.9.6.2", {"start": v(-109.05, 76.1) * mm, "end": v(-113.68, 76.1) * mm});
            skLineSegment(sketch, "E7.9.6.3", {"start": v(-109.05, 80.72) * mm, "end": v(-109.05, 76.1) * mm});
            skLineSegment(sketch, "E7.9.7.0", {"start": v(-109.05, 93.42) * mm, "end": v(-113.68, 93.42) * mm});
            skLineSegment(sketch, "E7.9.7.1", {"start": v(-113.68, 93.42) * mm, "end": v(-113.68, 88.8) * mm});
            skLineSegment(sketch, "E7.9.7.2", {"start": v(-109.05, 88.8) * mm, "end": v(-113.68, 88.8) * mm});
            skLineSegment(sketch, "E7.9.7.3", {"start": v(-109.05, 93.42) * mm, "end": v(-109.05, 88.8) * mm});
            skLineSegment(sketch, "E7.9.8.0", {"start": v(-109.05, 106.12) * mm, "end": v(-113.68, 106.12) * mm});
            skLineSegment(sketch, "E7.9.8.1", {"start": v(-113.68, 106.12) * mm, "end": v(-113.68, 101.5) * mm});
            skLineSegment(sketch, "E7.9.8.2", {"start": v(-109.05, 101.5) * mm, "end": v(-113.68, 101.5) * mm});
            skLineSegment(sketch, "E7.9.8.3", {"start": v(-109.05, 106.12) * mm, "end": v(-109.05, 101.5) * mm});
            skLineSegment(sketch, "E7.9.9.0", {"start": v(-109.05, 118.82) * mm, "end": v(-113.68, 118.82) * mm});
            skLineSegment(sketch, "E7.9.9.1", {"start": v(-113.68, 118.82) * mm, "end": v(-113.68, 114.2) * mm});
            skLineSegment(sketch, "E7.9.9.2", {"start": v(-109.05, 114.2) * mm, "end": v(-113.68, 114.2) * mm});
            skLineSegment(sketch, "E7.9.9.3", {"start": v(-109.05, 118.82) * mm, "end": v(-109.05, 114.2) * mm});
            skLineSegment(sketch, "E7.direction1", {"start": v(0.62, -0.1) * mm, "end": v(-12.08, -0.1) * mm, "construction": true});
            skLineSegment(sketch, "E7.direction2", {"start": v(0.62, -0.1) * mm, "end": v(0.62, 12.6) * mm, "construction": true});
            skLineSegment(sketch, "E8.MirrorCS", {"start": v(0.62, -0.1) * mm, "end": v(0.62, 4.52) * mm});
            skLineSegment(sketch, "E9.MirrorCS", {"start": v(5.25, -0.1) * mm, "end": v(5.25, 4.52) * mm});
            skLineSegment(sketch, "E10.MirrorCS", {"start": v(5.25, -38.2) * mm, "end": v(5.25, -33.58) * mm});
            skLineSegment(sketch, "E11.MirrorCS", {"start": v(5.25, -89) * mm, "end": v(5.25, -84.38) * mm});
            skLineSegment(sketch, "E12.MirrorCS", {"start": v(5.25, -33.58) * mm, "end": v(0.62, -33.58) * mm});
            skLineSegment(sketch, "E13.MirrorCS", {"start": v(5.25, -84.38) * mm, "end": v(0.62, -84.38) * mm});
            skLineSegment(sketch, "E14.MirrorCS", {"start": v(5.25, -12.8) * mm, "end": v(0.62, -12.8) * mm});
            skLineSegment(sketch, "E15.MirrorCS", {"start": v(5.25, -63.6) * mm, "end": v(0.62, -63.6) * mm});
            skLineSegment(sketch, "E16.MirrorCS", {"start": v(5.25, -114.4) * mm, "end": v(0.62, -114.4) * mm});
            skLineSegment(sketch, "E17.MirrorCS", {"start": v(5.25, -101.7) * mm, "end": v(0.62, -101.7) * mm});
            skLineSegment(sketch, "E18.MirrorCS", {"start": v(5.25, -50.9) * mm, "end": v(0.62, -50.9) * mm});
            skLineSegment(sketch, "E19.MirrorCS", {"start": v(0.62, -12.8) * mm, "end": v(0.62, -8.18) * mm});
            skLineSegment(sketch, "E20.MirrorCS", {"start": v(0.62, -63.6) * mm, "end": v(0.62, -58.98) * mm});
            skLineSegment(sketch, "E21.MirrorCS", {"start": v(0.62, -114.4) * mm, "end": v(0.62, -109.78) * mm});
            skLineSegment(sketch, "E22.MirrorCS", {"start": v(0.62, -50.9) * mm, "end": v(0.62, -46.28) * mm});
            skLineSegment(sketch, "E23.MirrorCS", {"start": v(5.25, -58.98) * mm, "end": v(0.62, -58.98) * mm});
            skLineSegment(sketch, "E24.MirrorCS", {"start": v(5.25, -109.78) * mm, "end": v(0.62, -109.78) * mm});
            skLineSegment(sketch, "E25.MirrorCS", {"start": v(5.25, -46.28) * mm, "end": v(0.62, -46.28) * mm});
            skLineSegment(sketch, "E26.MirrorCS", {"start": v(5.25, -8.18) * mm, "end": v(0.62, -8.18) * mm});
            skLineSegment(sketch, "E27.MirrorCS", {"start": v(5.25, -63.6) * mm, "end": v(5.25, -58.98) * mm});
            skLineSegment(sketch, "E28.MirrorCS", {"start": v(5.25, -12.8) * mm, "end": v(5.25, -8.18) * mm});
            skLineSegment(sketch, "E29.MirrorCS", {"start": v(5.25, -114.4) * mm, "end": v(5.25, -109.78) * mm});
            skLineSegment(sketch, "E30.MirrorCS", {"start": v(5.25, -50.9) * mm, "end": v(5.25, -46.28) * mm});
            skLineSegment(sketch, "E31.MirrorCS", {"start": v(5.25, -76.3) * mm, "end": v(0.62, -76.3) * mm});
            skLineSegment(sketch, "E32.MirrorCS", {"start": v(5.25, -25.5) * mm, "end": v(0.62, -25.5) * mm});
            skLineSegment(sketch, "E33.MirrorCS", {"start": v(5.25, -89) * mm, "end": v(0.62, -89) * mm});
            skLineSegment(sketch, "E34.MirrorCS", {"start": v(5.25, -38.2) * mm, "end": v(0.62, -38.2) * mm});
            skLineSegment(sketch, "E35.MirrorCS", {"start": v(0.62, -89) * mm, "end": v(0.62, -84.38) * mm});
            skLineSegment(sketch, "E36.MirrorCS", {"start": v(0.62, -38.2) * mm, "end": v(0.62, -33.58) * mm});
            skLineSegment(sketch, "E37.MirrorCS", {"start": v(0.62, 4.52) * mm, "end": v(0.62, -8.18) * mm, "construction": true});
            skLineSegment(sketch, "E38.MirrorCS", {"start": v(0.62, -101.7) * mm, "end": v(0.62, -97.08) * mm});
            skLineSegment(sketch, "E39.MirrorCS", {"start": v(5.25, -97.08) * mm, "end": v(0.62, -97.08) * mm});
            skLineSegment(sketch, "E40.MirrorCS", {"start": v(5.25, -101.7) * mm, "end": v(5.25, -97.08) * mm});
            skLineSegment(sketch, "E41.MirrorCS", {"start": v(0.62, -76.3) * mm, "end": v(0.62, -71.68) * mm});
            skLineSegment(sketch, "E42.MirrorCS", {"start": v(0.62, -25.5) * mm, "end": v(0.62, -20.88) * mm});
            skLineSegment(sketch, "E43.MirrorCS", {"start": v(5.25, -20.88) * mm, "end": v(0.62, -20.88) * mm});
            skLineSegment(sketch, "E44.MirrorCS", {"start": v(5.25, -71.68) * mm, "end": v(0.62, -71.68) * mm});
            skLineSegment(sketch, "E45.MirrorCS", {"start": v(5.25, -76.3) * mm, "end": v(5.25, -71.68) * mm});
            skLineSegment(sketch, "E46.MirrorCS", {"start": v(5.25, -25.5) * mm, "end": v(5.25, -20.88) * mm});
            skLineSegment(sketch, "E47.MirrorCS", {"start": v(-109.05, -25.5) * mm, "end": v(-109.05, -20.88) * mm});
            skLineSegment(sketch, "E48.MirrorCS", {"start": v(-109.05, -76.3) * mm, "end": v(-109.05, -71.68) * mm});
            skLineSegment(sketch, "E49.MirrorCS", {"start": v(-45.55, -0.1) * mm, "end": v(-45.55, 4.52) * mm});
            skLineSegment(sketch, "E50.MirrorCS", {"start": v(-45.55, -50.9) * mm, "end": v(-45.55, -46.28) * mm});
            skLineSegment(sketch, "E51.MirrorCS", {"start": v(-45.55, -101.7) * mm, "end": v(-45.55, -97.08) * mm});
            skLineSegment(sketch, "E52.MirrorCS", {"start": v(-109.05, -20.88) * mm, "end": v(-113.68, -20.88) * mm});
            skLineSegment(sketch, "E53.MirrorCS", {"start": v(-109.05, -71.68) * mm, "end": v(-113.68, -71.68) * mm});
            skLineSegment(sketch, "E54.MirrorCS", {"start": v(-45.55, -46.28) * mm, "end": v(-50.18, -46.28) * mm});
            skLineSegment(sketch, "E55.MirrorCS", {"start": v(-45.55, -97.08) * mm, "end": v(-50.18, -97.08) * mm});
            skLineSegment(sketch, "E56.MirrorCS", {"start": v(-50.18, -0.1) * mm, "end": v(-50.18, 4.52) * mm});
            skLineSegment(sketch, "E57.MirrorCS", {"start": v(-50.18, -50.9) * mm, "end": v(-50.18, -46.28) * mm});
            skLineSegment(sketch, "E58.MirrorCS", {"start": v(-50.18, -101.7) * mm, "end": v(-50.18, -97.08) * mm});
            skLineSegment(sketch, "E59.MirrorCS", {"start": v(-113.68, -25.5) * mm, "end": v(-113.68, -20.88) * mm});
            skLineSegment(sketch, "E60.MirrorCS", {"start": v(-113.68, -76.3) * mm, "end": v(-113.68, -71.68) * mm});
            skLineSegment(sketch, "E61.MirrorCS", {"start": v(-45.55, -50.9) * mm, "end": v(-50.18, -50.9) * mm});
            skLineSegment(sketch, "E62.MirrorCS", {"start": v(-109.05, -25.5) * mm, "end": v(-113.68, -25.5) * mm});
            skLineSegment(sketch, "E63.MirrorCS", {"start": v(-109.05, -76.3) * mm, "end": v(-113.68, -76.3) * mm});
            skLineSegment(sketch, "E64.MirrorCS", {"start": v(119.55, -50.9) * mm, "end": v(119.55, -46.28) * mm});
            skLineSegment(sketch, "E65.MirrorCS", {"start": v(106.85, -25.5) * mm, "end": v(106.85, -20.88) * mm});
            skLineSegment(sketch, "E66.MirrorCS", {"start": v(106.85, -76.3) * mm, "end": v(106.85, -71.68) * mm});
            skLineSegment(sketch, "E67.MirrorCS", {"start": v(-109.05, -114.4) * mm, "end": v(-109.05, -109.78) * mm});
            skLineSegment(sketch, "E68.MirrorCS", {"start": v(-70.95, -89) * mm, "end": v(-70.95, -84.38) * mm});
            skLineSegment(sketch, "E69.MirrorCS", {"start": v(-70.95, -38.2) * mm, "end": v(-70.95, -33.58) * mm});
            skLineSegment(sketch, "E70.MirrorCS", {"start": v(30.65, -25.5) * mm, "end": v(30.65, -20.88) * mm});
            skLineSegment(sketch, "E71.MirrorCS", {"start": v(30.65, -76.3) * mm, "end": v(30.65, -71.68) * mm});
            skLineSegment(sketch, "E72.MirrorCS", {"start": v(119.55, -46.28) * mm, "end": v(114.92, -46.28) * mm});
            skLineSegment(sketch, "E73.MirrorCS", {"start": v(-109.05, -109.78) * mm, "end": v(-113.68, -109.78) * mm});
            skLineSegment(sketch, "E74.MirrorCS", {"start": v(-83.65, -109.78) * mm, "end": v(-88.28, -109.78) * mm});
            skLineSegment(sketch, "E75.MirrorCS", {"start": v(106.85, -101.7) * mm, "end": v(102.22, -101.7) * mm});
            skLineSegment(sketch, "E76.MirrorCS", {"start": v(106.85, -50.9) * mm, "end": v(102.22, -50.9) * mm});
            skLineSegment(sketch, "E77.MirrorCS", {"start": v(-70.95, -114.4) * mm, "end": v(-75.58, -114.4) * mm});
            skLineSegment(sketch, "E78.MirrorCS", {"start": v(-70.95, -63.6) * mm, "end": v(-75.58, -63.6) * mm});
            skLineSegment(sketch, "E79.MirrorCS", {"start": v(-70.95, -12.8) * mm, "end": v(-75.58, -12.8) * mm});
            skLineSegment(sketch, "E80.MirrorCS", {"start": v(30.65, -101.7) * mm, "end": v(26.02, -101.7) * mm});
            skLineSegment(sketch, "E81.MirrorCS", {"start": v(30.65, -50.9) * mm, "end": v(26.02, -50.9) * mm});
            skLineSegment(sketch, "E82.MirrorCS", {"start": v(-96.35, -114.4) * mm, "end": v(-100.98, -114.4) * mm});
            skLineSegment(sketch, "E83.MirrorCS", {"start": v(-75.58, -114.4) * mm, "end": v(-75.58, -109.78) * mm});
            skLineSegment(sketch, "E84.MirrorCS", {"start": v(-75.58, -63.6) * mm, "end": v(-75.58, -58.98) * mm});
            skLineSegment(sketch, "E85.MirrorCS", {"start": v(-75.58, -12.8) * mm, "end": v(-75.58, -8.18) * mm});
            skLineSegment(sketch, "E86.MirrorCS", {"start": v(-100.98, -114.4) * mm, "end": v(-100.98, -109.78) * mm});
            skLineSegment(sketch, "E87.MirrorCS", {"start": v(26.02, -101.7) * mm, "end": v(26.02, -97.08) * mm});
            skLineSegment(sketch, "E88.MirrorCS", {"start": v(26.02, -50.9) * mm, "end": v(26.02, -46.28) * mm});
            skLineSegment(sketch, "E89.MirrorCS", {"start": v(26.02, -0.1) * mm, "end": v(26.02, 4.52) * mm});
            skLineSegment(sketch, "E90.MirrorCS", {"start": v(102.22, -0.1) * mm, "end": v(102.22, 4.52) * mm});
            skLineSegment(sketch, "E91.MirrorCS", {"start": v(102.22, -101.7) * mm, "end": v(102.22, -97.08) * mm});
            skLineSegment(sketch, "E92.MirrorCS", {"start": v(102.22, -50.9) * mm, "end": v(102.22, -46.28) * mm});
            skLineSegment(sketch, "E93.MirrorCS", {"start": v(-70.95, -109.78) * mm, "end": v(-75.58, -109.78) * mm});
            skLineSegment(sketch, "E94.MirrorCS", {"start": v(-70.95, -58.98) * mm, "end": v(-75.58, -58.98) * mm});
            skLineSegment(sketch, "E95.MirrorCS", {"start": v(-70.95, -8.18) * mm, "end": v(-75.58, -8.18) * mm});
            skLineSegment(sketch, "E96.MirrorCS", {"start": v(-96.35, -109.78) * mm, "end": v(-100.98, -109.78) * mm});
            skLineSegment(sketch, "E97.MirrorCS", {"start": v(30.65, -46.28) * mm, "end": v(26.02, -46.28) * mm});
            skLineSegment(sketch, "E98.MirrorCS", {"start": v(106.85, -46.28) * mm, "end": v(102.22, -46.28) * mm});
            skLineSegment(sketch, "E99.MirrorCS", {"start": v(30.65, -50.9) * mm, "end": v(30.65, -46.28) * mm});
            skLineSegment(sketch, "E100.MirrorCS", {"start": v(30.65, -101.7) * mm, "end": v(30.65, -97.08) * mm});
            skLineSegment(sketch, "E101.MirrorCS", {"start": v(30.65, -0.1) * mm, "end": v(30.65, 4.52) * mm});
            skLineSegment(sketch, "E102.MirrorCS", {"start": v(106.85, -0.1) * mm, "end": v(106.85, 4.52) * mm});
            skLineSegment(sketch, "E103.MirrorCS", {"start": v(106.85, -101.7) * mm, "end": v(106.85, -97.08) * mm});
            skLineSegment(sketch, "E104.MirrorCS", {"start": v(106.85, -50.9) * mm, "end": v(106.85, -46.28) * mm});
            skLineSegment(sketch, "E105.MirrorCS", {"start": v(-70.95, -114.4) * mm, "end": v(-70.95, -109.78) * mm});
            skLineSegment(sketch, "E106.MirrorCS", {"start": v(-70.95, -63.6) * mm, "end": v(-70.95, -58.98) * mm});
            skLineSegment(sketch, "E107.MirrorCS", {"start": v(-70.95, -12.8) * mm, "end": v(-70.95, -8.18) * mm});
            skLineSegment(sketch, "E108.MirrorCS", {"start": v(56.05, -114.4) * mm, "end": v(51.42, -114.4) * mm});
            skLineSegment(sketch, "E109.MirrorCS", {"start": v(81.45, -63.6) * mm, "end": v(76.82, -63.6) * mm});
            skLineSegment(sketch, "E110.MirrorCS", {"start": v(81.45, -12.8) * mm, "end": v(76.82, -12.8) * mm});
            skLineSegment(sketch, "E111.MirrorCS", {"start": v(106.85, -12.8) * mm, "end": v(102.22, -12.8) * mm});
            skLineSegment(sketch, "E112.MirrorCS", {"start": v(106.85, -63.6) * mm, "end": v(102.22, -63.6) * mm});
            skLineSegment(sketch, "E113.MirrorCS", {"start": v(30.65, -63.6) * mm, "end": v(26.02, -63.6) * mm});
            skLineSegment(sketch, "E114.MirrorCS", {"start": v(30.65, -12.8) * mm, "end": v(26.02, -12.8) * mm});
            skLineSegment(sketch, "E115.MirrorCS", {"start": v(-109.05, -101.7) * mm, "end": v(-113.68, -101.7) * mm});
            skLineSegment(sketch, "E116.MirrorCS", {"start": v(-109.05, -50.9) * mm, "end": v(-113.68, -50.9) * mm});
            skLineSegment(sketch, "E117.MirrorCS", {"start": v(76.82, -63.6) * mm, "end": v(76.82, -58.98) * mm});
            skLineSegment(sketch, "E118.MirrorCS", {"start": v(76.82, -12.8) * mm, "end": v(76.82, -8.18) * mm});
            skLineSegment(sketch, "E119.MirrorCS", {"start": v(102.22, -12.8) * mm, "end": v(102.22, -8.18) * mm});
            skLineSegment(sketch, "E120.MirrorCS", {"start": v(102.22, -63.6) * mm, "end": v(102.22, -58.98) * mm});
            skLineSegment(sketch, "E121.MirrorCS", {"start": v(-50.18, -76.3) * mm, "end": v(-50.18, -71.68) * mm});
            skLineSegment(sketch, "E122.MirrorCS", {"start": v(-50.18, -25.5) * mm, "end": v(-50.18, -20.88) * mm});
            skLineSegment(sketch, "E123.MirrorCS", {"start": v(26.02, -63.6) * mm, "end": v(26.02, -58.98) * mm});
            skLineSegment(sketch, "E124.MirrorCS", {"start": v(26.02, -12.8) * mm, "end": v(26.02, -8.18) * mm});
            skLineSegment(sketch, "E125.MirrorCS", {"start": v(51.42, -114.4) * mm, "end": v(51.42, -109.78) * mm});
            skLineSegment(sketch, "E126.MirrorCS", {"start": v(-113.68, -101.7) * mm, "end": v(-113.68, -97.08) * mm});
            skLineSegment(sketch, "E127.MirrorCS", {"start": v(-113.68, -0.1) * mm, "end": v(-113.68, 4.52) * mm});
            skLineSegment(sketch, "E128.MirrorCS", {"start": v(-113.68, -50.9) * mm, "end": v(-113.68, -46.28) * mm});
            skLineSegment(sketch, "E129.MirrorCS", {"start": v(106.85, -8.18) * mm, "end": v(102.22, -8.18) * mm});
            skLineSegment(sketch, "E130.MirrorCS", {"start": v(106.85, -58.98) * mm, "end": v(102.22, -58.98) * mm});
            skLineSegment(sketch, "E131.MirrorCS", {"start": v(-45.55, -71.68) * mm, "end": v(-50.18, -71.68) * mm});
            skLineSegment(sketch, "E132.MirrorCS", {"start": v(-45.55, -20.88) * mm, "end": v(-50.18, -20.88) * mm});
            skLineSegment(sketch, "E133.MirrorCS", {"start": v(30.65, -58.98) * mm, "end": v(26.02, -58.98) * mm});
            skLineSegment(sketch, "E134.MirrorCS", {"start": v(30.65, -8.18) * mm, "end": v(26.02, -8.18) * mm});
            skLineSegment(sketch, "E135.MirrorCS", {"start": v(56.05, -109.78) * mm, "end": v(51.42, -109.78) * mm});
            skLineSegment(sketch, "E136.MirrorCS", {"start": v(81.45, -58.98) * mm, "end": v(76.82, -58.98) * mm});
            skLineSegment(sketch, "E137.MirrorCS", {"start": v(81.45, -8.18) * mm, "end": v(76.82, -8.18) * mm});
            skLineSegment(sketch, "E138.MirrorCS", {"start": v(-109.05, -97.08) * mm, "end": v(-113.68, -97.08) * mm});
            skLineSegment(sketch, "E139.MirrorCS", {"start": v(-109.05, -46.28) * mm, "end": v(-113.68, -46.28) * mm});
            skLineSegment(sketch, "E140.MirrorCS", {"start": v(106.85, -63.6) * mm, "end": v(106.85, -58.98) * mm});
            skLineSegment(sketch, "E141.MirrorCS", {"start": v(-45.55, -76.3) * mm, "end": v(-45.55, -71.68) * mm});
            skLineSegment(sketch, "E142.MirrorCS", {"start": v(-45.55, -25.5) * mm, "end": v(-45.55, -20.88) * mm});
            skLineSegment(sketch, "E143.MirrorCS", {"start": v(30.65, -63.6) * mm, "end": v(30.65, -58.98) * mm});
            skLineSegment(sketch, "E144.MirrorCS", {"start": v(30.65, -12.8) * mm, "end": v(30.65, -8.18) * mm});
            skLineSegment(sketch, "E145.MirrorCS", {"start": v(81.45, -63.6) * mm, "end": v(81.45, -58.98) * mm});
            skLineSegment(sketch, "E146.MirrorCS", {"start": v(81.45, -12.8) * mm, "end": v(81.45, -8.18) * mm});
            skLineSegment(sketch, "E147.MirrorCS", {"start": v(106.85, -12.8) * mm, "end": v(106.85, -8.18) * mm});
            skLineSegment(sketch, "E148.MirrorCS", {"start": v(-109.05, -101.7) * mm, "end": v(-109.05, -97.08) * mm});
            skLineSegment(sketch, "E149.MirrorCS", {"start": v(-109.05, -50.9) * mm, "end": v(-109.05, -46.28) * mm});
            skLineSegment(sketch, "E150.MirrorCS", {"start": v(-109.05, -0.1) * mm, "end": v(-109.05, 4.52) * mm});
            skLineSegment(sketch, "E151.MirrorCS", {"start": v(-70.95, -89) * mm, "end": v(-75.58, -89) * mm});
            skLineSegment(sketch, "E152.MirrorCS", {"start": v(-70.95, -38.2) * mm, "end": v(-75.58, -38.2) * mm});
            skLineSegment(sketch, "E153.MirrorCS", {"start": v(-83.65, -114.4) * mm, "end": v(-88.28, -114.4) * mm});
            skLineSegment(sketch, "E154.MirrorCS", {"start": v(-109.05, -114.4) * mm, "end": v(-113.68, -114.4) * mm});
            skLineSegment(sketch, "E155.MirrorCS", {"start": v(30.65, -76.3) * mm, "end": v(26.02, -76.3) * mm});
            skLineSegment(sketch, "E156.MirrorCS", {"start": v(30.65, -25.5) * mm, "end": v(26.02, -25.5) * mm});
            skLineSegment(sketch, "E157.MirrorCS", {"start": v(106.85, -25.5) * mm, "end": v(102.22, -25.5) * mm});
            skLineSegment(sketch, "E158.MirrorCS", {"start": v(119.55, -50.9) * mm, "end": v(114.92, -50.9) * mm});
            skLineSegment(sketch, "E159.MirrorCS", {"start": v(106.85, -76.3) * mm, "end": v(102.22, -76.3) * mm});
            skLineSegment(sketch, "E160.MirrorCS", {"start": v(-75.58, -89) * mm, "end": v(-75.58, -84.38) * mm});
            skLineSegment(sketch, "E161.MirrorCS", {"start": v(-75.58, -38.2) * mm, "end": v(-75.58, -33.58) * mm});
            skLineSegment(sketch, "E162.MirrorCS", {"start": v(-88.28, -114.4) * mm, "end": v(-88.28, -109.78) * mm});
            skLineSegment(sketch, "E163.MirrorCS", {"start": v(-113.68, -114.4) * mm, "end": v(-113.68, -109.78) * mm});
            skLineSegment(sketch, "E164.MirrorCS", {"start": v(26.02, -76.3) * mm, "end": v(26.02, -71.68) * mm});
            skLineSegment(sketch, "E165.MirrorCS", {"start": v(26.02, -25.5) * mm, "end": v(26.02, -20.88) * mm});
            skLineSegment(sketch, "E166.MirrorCS", {"start": v(102.22, -25.5) * mm, "end": v(102.22, -20.88) * mm});
            skLineSegment(sketch, "E167.MirrorCS", {"start": v(102.22, -76.3) * mm, "end": v(102.22, -71.68) * mm});
            skLineSegment(sketch, "E168.MirrorCS", {"start": v(-70.95, -50.9) * mm, "end": v(-70.95, -46.28) * mm});
            skLineSegment(sketch, "E169.MirrorCS", {"start": v(-20.15, -0.1) * mm, "end": v(-20.15, 4.52) * mm});
            skLineSegment(sketch, "E170.MirrorCS", {"start": v(119.55, -63.6) * mm, "end": v(119.55, -58.98) * mm});
            skLineSegment(sketch, "E171.MirrorCS", {"start": v(106.85, -38.2) * mm, "end": v(106.85, -33.58) * mm});
            skLineSegment(sketch, "E172.MirrorCS", {"start": v(106.85, -89) * mm, "end": v(106.85, -84.38) * mm});
            skLineSegment(sketch, "E173.MirrorCS", {"start": v(119.55, -12.8) * mm, "end": v(119.55, -8.18) * mm});
            skLineSegment(sketch, "E174.MirrorCS", {"start": v(81.45, -38.2) * mm, "end": v(81.45, -33.58) * mm});
            skLineSegment(sketch, "E175.MirrorCS", {"start": v(81.45, -89) * mm, "end": v(81.45, -84.38) * mm});
            skLineSegment(sketch, "E176.MirrorCS", {"start": v(94.15, -12.8) * mm, "end": v(94.15, -8.18) * mm});
            skLineSegment(sketch, "E177.MirrorCS", {"start": v(94.15, -63.6) * mm, "end": v(94.15, -58.98) * mm});
            skLineSegment(sketch, "E178.MirrorCS", {"start": v(68.75, -12.8) * mm, "end": v(68.75, -8.18) * mm});
            skLineSegment(sketch, "E179.MirrorCS", {"start": v(68.75, -63.6) * mm, "end": v(68.75, -58.98) * mm});
            skLineSegment(sketch, "E180.MirrorCS", {"start": v(43.35, -12.8) * mm, "end": v(43.35, -8.18) * mm});
            skLineSegment(sketch, "E181.MirrorCS", {"start": v(43.35, -63.6) * mm, "end": v(43.35, -58.98) * mm});
            skLineSegment(sketch, "E182.MirrorCS", {"start": v(17.95, -63.6) * mm, "end": v(17.95, -58.98) * mm});
            skLineSegment(sketch, "E183.MirrorCS", {"start": v(30.65, -38.2) * mm, "end": v(30.65, -33.58) * mm});
            skLineSegment(sketch, "E184.MirrorCS", {"start": v(30.65, -89) * mm, "end": v(30.65, -84.38) * mm});
            skLineSegment(sketch, "E185.MirrorCS", {"start": v(17.95, -12.8) * mm, "end": v(17.95, -8.18) * mm});
            skLineSegment(sketch, "E186.MirrorCS", {"start": v(-70.95, -46.28) * mm, "end": v(-75.58, -46.28) * mm});
            skLineSegment(sketch, "E187.MirrorCS", {"start": v(-7.45, -20.88) * mm, "end": v(-12.08, -20.88) * mm});
            skLineSegment(sketch, "E188.MirrorCS", {"start": v(119.55, -58.98) * mm, "end": v(114.92, -58.98) * mm});
            skLineSegment(sketch, "E189.MirrorCS", {"start": v(119.55, -8.18) * mm, "end": v(114.92, -8.18) * mm});
            skLineSegment(sketch, "E190.MirrorCS", {"start": v(81.45, -33.58) * mm, "end": v(76.82, -33.58) * mm});
            skLineSegment(sketch, "E191.MirrorCS", {"start": v(81.45, -84.38) * mm, "end": v(76.82, -84.38) * mm});
            skLineSegment(sketch, "E192.MirrorCS", {"start": v(94.15, -8.18) * mm, "end": v(89.52, -8.18) * mm});
            skLineSegment(sketch, "E193.MirrorCS", {"start": v(94.15, -58.98) * mm, "end": v(89.52, -58.98) * mm});
            skLineSegment(sketch, "E194.MirrorCS", {"start": v(68.75, -8.18) * mm, "end": v(64.12, -8.18) * mm});
            skLineSegment(sketch, "E195.MirrorCS", {"start": v(68.75, -58.98) * mm, "end": v(64.12, -58.98) * mm});
            skLineSegment(sketch, "E196.MirrorCS", {"start": v(43.35, -8.18) * mm, "end": v(38.72, -8.18) * mm});
            skLineSegment(sketch, "E197.MirrorCS", {"start": v(43.35, -58.98) * mm, "end": v(38.72, -58.98) * mm});
            skLineSegment(sketch, "E198.MirrorCS", {"start": v(17.95, -58.98) * mm, "end": v(13.32, -58.98) * mm});
            skLineSegment(sketch, "E199.MirrorCS", {"start": v(17.95, -8.18) * mm, "end": v(13.32, -8.18) * mm});
            skLineSegment(sketch, "E200.MirrorCS", {"start": v(-75.58, -50.9) * mm, "end": v(-75.58, -46.28) * mm});
            skLineSegment(sketch, "E201.MirrorCS", {"start": v(-24.78, -0.1) * mm, "end": v(-24.78, 4.52) * mm});
            skLineSegment(sketch, "E202.MirrorCS", {"start": v(-12.08, -25.5) * mm, "end": v(-12.08, -20.88) * mm});
            skLineSegment(sketch, "E203.MirrorCS", {"start": v(114.92, -63.6) * mm, "end": v(114.92, -58.98) * mm});
            skLineSegment(sketch, "E204.MirrorCS", {"start": v(102.22, -38.2) * mm, "end": v(102.22, -33.58) * mm});
            skLineSegment(sketch, "E205.MirrorCS", {"start": v(102.22, -89) * mm, "end": v(102.22, -84.38) * mm});
            skLineSegment(sketch, "E206.MirrorCS", {"start": v(114.92, -12.8) * mm, "end": v(114.92, -8.18) * mm});
            skLineSegment(sketch, "E207.MirrorCS", {"start": v(76.82, -38.2) * mm, "end": v(76.82, -33.58) * mm});
            skLineSegment(sketch, "E208.MirrorCS", {"start": v(76.82, -89) * mm, "end": v(76.82, -84.38) * mm});
            skLineSegment(sketch, "E209.MirrorCS", {"start": v(89.52, -12.8) * mm, "end": v(89.52, -8.18) * mm});
            skLineSegment(sketch, "E210.MirrorCS", {"start": v(89.52, -63.6) * mm, "end": v(89.52, -58.98) * mm});
            skLineSegment(sketch, "E211.MirrorCS", {"start": v(64.12, -12.8) * mm, "end": v(64.12, -8.18) * mm});
            skLineSegment(sketch, "E212.MirrorCS", {"start": v(64.12, -63.6) * mm, "end": v(64.12, -58.98) * mm});
            skLineSegment(sketch, "E213.MirrorCS", {"start": v(38.72, -12.8) * mm, "end": v(38.72, -8.18) * mm});
            skLineSegment(sketch, "E214.MirrorCS", {"start": v(38.72, -63.6) * mm, "end": v(38.72, -58.98) * mm});
            skLineSegment(sketch, "E215.MirrorCS", {"start": v(13.32, -63.6) * mm, "end": v(13.32, -58.98) * mm});
            skLineSegment(sketch, "E216.MirrorCS", {"start": v(26.02, -38.2) * mm, "end": v(26.02, -33.58) * mm});
            skLineSegment(sketch, "E217.MirrorCS", {"start": v(26.02, -89) * mm, "end": v(26.02, -84.38) * mm});
            skLineSegment(sketch, "E218.MirrorCS", {"start": v(13.32, -12.8) * mm, "end": v(13.32, -8.18) * mm});
            skLineSegment(sketch, "E219.MirrorCS", {"start": v(-70.95, -50.9) * mm, "end": v(-75.58, -50.9) * mm});
            skLineSegment(sketch, "E220.MirrorCS", {"start": v(-45.55, -101.7) * mm, "end": v(-50.18, -101.7) * mm});
            skLineSegment(sketch, "E221.MirrorCS", {"start": v(-7.45, -25.5) * mm, "end": v(-12.08, -25.5) * mm});
            skLineSegment(sketch, "E222.MirrorCS", {"start": v(119.55, -63.6) * mm, "end": v(114.92, -63.6) * mm});
            skLineSegment(sketch, "E223.MirrorCS", {"start": v(106.85, -38.2) * mm, "end": v(102.22, -38.2) * mm});
            skLineSegment(sketch, "E224.MirrorCS", {"start": v(106.85, -89) * mm, "end": v(102.22, -89) * mm});
            skLineSegment(sketch, "E225.MirrorCS", {"start": v(119.55, -12.8) * mm, "end": v(114.92, -12.8) * mm});
            skLineSegment(sketch, "E226.MirrorCS", {"start": v(81.45, -38.2) * mm, "end": v(76.82, -38.2) * mm});
            skLineSegment(sketch, "E227.MirrorCS", {"start": v(81.45, -89) * mm, "end": v(76.82, -89) * mm});
            skLineSegment(sketch, "E228.MirrorCS", {"start": v(94.15, -12.8) * mm, "end": v(89.52, -12.8) * mm});
            skLineSegment(sketch, "E229.MirrorCS", {"start": v(94.15, -63.6) * mm, "end": v(89.52, -63.6) * mm});
            skLineSegment(sketch, "E230.MirrorCS", {"start": v(68.75, -12.8) * mm, "end": v(64.12, -12.8) * mm});
            skLineSegment(sketch, "E231.MirrorCS", {"start": v(68.75, -63.6) * mm, "end": v(64.12, -63.6) * mm});
            skLineSegment(sketch, "E232.MirrorCS", {"start": v(43.35, -12.8) * mm, "end": v(38.72, -12.8) * mm});
            skLineSegment(sketch, "E233.MirrorCS", {"start": v(43.35, -63.6) * mm, "end": v(38.72, -63.6) * mm});
            skLineSegment(sketch, "E234.MirrorCS", {"start": v(17.95, -63.6) * mm, "end": v(13.32, -63.6) * mm});
            skLineSegment(sketch, "E235.MirrorCS", {"start": v(17.95, -114.4) * mm, "end": v(13.32, -114.4) * mm});
            skLineSegment(sketch, "E236.MirrorCS", {"start": v(30.65, -38.2) * mm, "end": v(26.02, -38.2) * mm});
            skLineSegment(sketch, "E237.MirrorCS", {"start": v(30.65, -89) * mm, "end": v(26.02, -89) * mm});
            skLineSegment(sketch, "E238.MirrorCS", {"start": v(17.95, -12.8) * mm, "end": v(13.32, -12.8) * mm});
            skLineSegment(sketch, "E239.MirrorCS", {"start": v(-32.85, -114.4) * mm, "end": v(-32.85, -109.78) * mm});
            skLineSegment(sketch, "E240.MirrorCS", {"start": v(-7.45, -12.8) * mm, "end": v(-7.45, -8.18) * mm});
            skLineSegment(sketch, "E241.MirrorCS", {"start": v(-7.45, -63.6) * mm, "end": v(-7.45, -58.98) * mm});
            skLineSegment(sketch, "E242.MirrorCS", {"start": v(119.55, -0.1) * mm, "end": v(119.55, 4.52) * mm});
            skLineSegment(sketch, "E243.MirrorCS", {"start": v(81.45, -25.5) * mm, "end": v(81.45, -20.88) * mm});
            skLineSegment(sketch, "E244.MirrorCS", {"start": v(81.45, -76.3) * mm, "end": v(81.45, -71.68) * mm});
            skLineSegment(sketch, "E245.MirrorCS", {"start": v(94.15, -50.9) * mm, "end": v(94.15, -46.28) * mm});
            skLineSegment(sketch, "E246.MirrorCS", {"start": v(-58.25, -114.4) * mm, "end": v(-58.25, -109.78) * mm});
            skLineSegment(sketch, "E247.MirrorCS", {"start": v(17.95, -50.9) * mm, "end": v(17.95, -46.28) * mm});
            skLineSegment(sketch, "E248.MirrorCS", {"start": v(-7.45, -109.78) * mm, "end": v(-12.08, -109.78) * mm});
            skLineSegment(sketch, "E249.MirrorCS", {"start": v(-7.45, -8.18) * mm, "end": v(-12.08, -8.18) * mm});
            skLineSegment(sketch, "E250.MirrorCS", {"start": v(-7.45, -58.98) * mm, "end": v(-12.08, -58.98) * mm});
            skLineSegment(sketch, "E251.MirrorCS", {"start": v(81.45, -20.88) * mm, "end": v(76.82, -20.88) * mm});
            skLineSegment(sketch, "E252.MirrorCS", {"start": v(81.45, -71.68) * mm, "end": v(76.82, -71.68) * mm});
            skLineSegment(sketch, "E253.MirrorCS", {"start": v(94.15, -46.28) * mm, "end": v(89.52, -46.28) * mm});
            skLineSegment(sketch, "E254.MirrorCS", {"start": v(68.75, -46.28) * mm, "end": v(64.12, -46.28) * mm});
            skLineSegment(sketch, "E255.MirrorCS", {"start": v(43.35, -46.28) * mm, "end": v(38.72, -46.28) * mm});
            skLineSegment(sketch, "E256.MirrorCS", {"start": v(-70.95, -84.38) * mm, "end": v(-75.58, -84.38) * mm});
            skLineSegment(sketch, "E257.MirrorCS", {"start": v(-58.25, -109.78) * mm, "end": v(-62.88, -109.78) * mm});
            skLineSegment(sketch, "E258.MirrorCS", {"start": v(-70.95, -33.58) * mm, "end": v(-75.58, -33.58) * mm});
            skLineSegment(sketch, "E259.MirrorCS", {"start": v(-32.85, -109.78) * mm, "end": v(-37.48, -109.78) * mm});
            skLineSegment(sketch, "E260.MirrorCS", {"start": v(-20.15, -12.8) * mm, "end": v(-24.78, -12.8) * mm});
            skLineSegment(sketch, "E261.MirrorCS", {"start": v(-20.15, -63.6) * mm, "end": v(-24.78, -63.6) * mm});
            skLineSegment(sketch, "E262.MirrorCS", {"start": v(-20.15, -114.4) * mm, "end": v(-24.78, -114.4) * mm});
            skLineSegment(sketch, "E263.MirrorCS", {"start": v(-45.55, -114.4) * mm, "end": v(-50.18, -114.4) * mm});
            skLineSegment(sketch, "E264.MirrorCS", {"start": v(-96.35, -63.6) * mm, "end": v(-100.98, -63.6) * mm});
            skLineSegment(sketch, "E265.MirrorCS", {"start": v(56.05, -50.9) * mm, "end": v(51.42, -50.9) * mm});
            skLineSegment(sketch, "E266.MirrorCS", {"start": v(81.45, -50.9) * mm, "end": v(76.82, -50.9) * mm});
            skLineSegment(sketch, "E267.MirrorCS", {"start": v(-109.05, -89) * mm, "end": v(-113.68, -89) * mm});
            skLineSegment(sketch, "E268.MirrorCS", {"start": v(-24.78, -114.4) * mm, "end": v(-24.78, -109.78) * mm});
            skLineSegment(sketch, "E269.MirrorCS", {"start": v(-24.78, -63.6) * mm, "end": v(-24.78, -58.98) * mm});
            skLineSegment(sketch, "E270.MirrorCS", {"start": v(-50.18, -114.4) * mm, "end": v(-50.18, -109.78) * mm});
            skLineSegment(sketch, "E271.MirrorCS", {"start": v(-113.68, -89) * mm, "end": v(-113.68, -84.38) * mm});
            skLineSegment(sketch, "E272.MirrorCS", {"start": v(51.42, -50.9) * mm, "end": v(51.42, -46.28) * mm});
            skLineSegment(sketch, "E273.MirrorCS", {"start": v(76.82, -50.9) * mm, "end": v(76.82, -46.28) * mm});
            skLineSegment(sketch, "E274.MirrorCS", {"start": v(76.82, -0.1) * mm, "end": v(76.82, 4.52) * mm});
            skLineSegment(sketch, "E275.MirrorCS", {"start": v(76.82, -101.7) * mm, "end": v(76.82, -97.08) * mm});
            skLineSegment(sketch, "E276.MirrorCS", {"start": v(-20.15, -8.18) * mm, "end": v(-24.78, -8.18) * mm});
            skLineSegment(sketch, "E277.MirrorCS", {"start": v(-20.15, -109.78) * mm, "end": v(-24.78, -109.78) * mm});
            skLineSegment(sketch, "E278.MirrorCS", {"start": v(-20.15, -58.98) * mm, "end": v(-24.78, -58.98) * mm});
            skLineSegment(sketch, "E279.MirrorCS", {"start": v(-45.55, -109.78) * mm, "end": v(-50.18, -109.78) * mm});
            skLineSegment(sketch, "E280.MirrorCS", {"start": v(56.05, -46.28) * mm, "end": v(51.42, -46.28) * mm});
            skLineSegment(sketch, "E281.MirrorCS", {"start": v(81.45, -46.28) * mm, "end": v(76.82, -46.28) * mm});
            skLineSegment(sketch, "E282.MirrorCS", {"start": v(81.45, -97.08) * mm, "end": v(76.82, -97.08) * mm});
            skLineSegment(sketch, "E283.MirrorCS", {"start": v(81.45, -50.9) * mm, "end": v(81.45, -46.28) * mm});
            skLineSegment(sketch, "E284.MirrorCS", {"start": v(81.45, -0.1) * mm, "end": v(81.45, 4.52) * mm});
            skLineSegment(sketch, "E285.MirrorCS", {"start": v(81.45, -101.7) * mm, "end": v(81.45, -97.08) * mm});
            skLineSegment(sketch, "E286.MirrorCS", {"start": v(-20.15, -12.8) * mm, "end": v(-20.15, -8.18) * mm});
            skLineSegment(sketch, "E287.MirrorCS", {"start": v(-20.15, -114.4) * mm, "end": v(-20.15, -109.78) * mm});
            skLineSegment(sketch, "E288.MirrorCS", {"start": v(-20.15, -63.6) * mm, "end": v(-20.15, -58.98) * mm});
            skLineSegment(sketch, "E289.MirrorCS", {"start": v(-45.55, -114.4) * mm, "end": v(-45.55, -109.78) * mm});
            skLineSegment(sketch, "E290.MirrorCS", {"start": v(-109.05, -89) * mm, "end": v(-109.05, -84.38) * mm});
            skLineSegment(sketch, "E291.MirrorCS", {"start": v(56.05, -63.6) * mm, "end": v(51.42, -63.6) * mm});
            skLineSegment(sketch, "E292.MirrorCS", {"start": v(56.05, -12.8) * mm, "end": v(51.42, -12.8) * mm});
            skLineSegment(sketch, "E293.MirrorCS", {"start": v(81.45, -114.4) * mm, "end": v(76.82, -114.4) * mm});
            skLineSegment(sketch, "E294.MirrorCS", {"start": v(106.85, -114.4) * mm, "end": v(102.22, -114.4) * mm});
            skLineSegment(sketch, "E295.MirrorCS", {"start": v(-20.15, -25.5) * mm, "end": v(-24.78, -25.5) * mm});
            skLineSegment(sketch, "E296.MirrorCS", {"start": v(-32.85, -50.9) * mm, "end": v(-37.48, -50.9) * mm});
            skLineSegment(sketch, "E297.MirrorCS", {"start": v(30.65, -114.4) * mm, "end": v(26.02, -114.4) * mm});
            skLineSegment(sketch, "E298.MirrorCS", {"start": v(-58.25, -50.9) * mm, "end": v(-62.88, -50.9) * mm});
            skLineSegment(sketch, "E299.MirrorCS", {"start": v(-45.55, -76.3) * mm, "end": v(-50.18, -76.3) * mm});
            skLineSegment(sketch, "E300.MirrorCS", {"start": v(-45.55, -25.5) * mm, "end": v(-50.18, -25.5) * mm});
            skLineSegment(sketch, "E301.MirrorCS", {"start": v(-83.65, -50.9) * mm, "end": v(-88.28, -50.9) * mm});
            skLineSegment(sketch, "E302.MirrorCS", {"start": v(76.82, -114.4) * mm, "end": v(76.82, -109.78) * mm});
            skLineSegment(sketch, "E303.MirrorCS", {"start": v(102.22, -114.4) * mm, "end": v(102.22, -109.78) * mm});
            skLineSegment(sketch, "E304.MirrorCS", {"start": v(-24.78, -25.5) * mm, "end": v(-24.78, -20.88) * mm});
            skLineSegment(sketch, "E305.MirrorCS", {"start": v(-12.08, -0.1) * mm, "end": v(-12.08, 4.52) * mm});
            skLineSegment(sketch, "E306.MirrorCS", {"start": v(-62.88, -50.9) * mm, "end": v(-62.88, -46.28) * mm});
            skLineSegment(sketch, "E307.MirrorCS", {"start": v(26.02, -114.4) * mm, "end": v(26.02, -109.78) * mm});
            skLineSegment(sketch, "E308.MirrorCS", {"start": v(51.42, -63.6) * mm, "end": v(51.42, -58.98) * mm});
            skLineSegment(sketch, "E309.MirrorCS", {"start": v(51.42, -12.8) * mm, "end": v(51.42, -8.18) * mm});
            skLineSegment(sketch, "E310.MirrorCS", {"start": v(81.45, -109.78) * mm, "end": v(76.82, -109.78) * mm});
            skLineSegment(sketch, "E311.MirrorCS", {"start": v(106.85, -109.78) * mm, "end": v(102.22, -109.78) * mm});
            skLineSegment(sketch, "E312.MirrorCS", {"start": v(-32.85, -46.28) * mm, "end": v(-37.48, -46.28) * mm});
            skLineSegment(sketch, "E313.MirrorCS", {"start": v(-58.25, -46.28) * mm, "end": v(-62.88, -46.28) * mm});
            skLineSegment(sketch, "E314.MirrorCS", {"start": v(30.65, -109.78) * mm, "end": v(26.02, -109.78) * mm});
            skLineSegment(sketch, "E315.MirrorCS", {"start": v(56.05, -58.98) * mm, "end": v(51.42, -58.98) * mm});
            skLineSegment(sketch, "E316.MirrorCS", {"start": v(56.05, -8.18) * mm, "end": v(51.42, -8.18) * mm});
            skLineSegment(sketch, "E317.MirrorCS", {"start": v(-83.65, -46.28) * mm, "end": v(-88.28, -46.28) * mm});
            skLineSegment(sketch, "E318.MirrorCS", {"start": v(106.85, -114.4) * mm, "end": v(106.85, -109.78) * mm});
            skLineSegment(sketch, "E319.MirrorCS", {"start": v(-20.15, -25.5) * mm, "end": v(-20.15, -20.88) * mm});
            skLineSegment(sketch, "E320.MirrorCS", {"start": v(-32.85, -50.9) * mm, "end": v(-32.85, -46.28) * mm});
            skLineSegment(sketch, "E321.MirrorCS", {"start": v(-58.25, -50.9) * mm, "end": v(-58.25, -46.28) * mm});
            skLineSegment(sketch, "E322.MirrorCS", {"start": v(-83.65, -50.9) * mm, "end": v(-83.65, -46.28) * mm});
            skLineSegment(sketch, "E323.MirrorCS", {"start": v(30.65, -114.4) * mm, "end": v(30.65, -109.78) * mm});
            skLineSegment(sketch, "E324.MirrorCS", {"start": v(56.05, -63.6) * mm, "end": v(56.05, -58.98) * mm});
            skLineSegment(sketch, "E325.MirrorCS", {"start": v(56.05, -12.8) * mm, "end": v(56.05, -8.18) * mm});
            skLineSegment(sketch, "E326.MirrorCS", {"start": v(81.45, -114.4) * mm, "end": v(81.45, -109.78) * mm});
            skLineSegment(sketch, "E327.MirrorCS", {"start": v(-7.45, -114.4) * mm, "end": v(-12.08, -114.4) * mm});
            skLineSegment(sketch, "E328.MirrorCS", {"start": v(-7.45, -63.6) * mm, "end": v(-12.08, -63.6) * mm});
            skLineSegment(sketch, "E329.MirrorCS", {"start": v(-32.85, -114.4) * mm, "end": v(-37.48, -114.4) * mm});
            skLineSegment(sketch, "E330.MirrorCS", {"start": v(-7.45, -12.8) * mm, "end": v(-12.08, -12.8) * mm});
            skLineSegment(sketch, "E331.MirrorCS", {"start": v(-58.25, -114.4) * mm, "end": v(-62.88, -114.4) * mm});
            skLineSegment(sketch, "E332.MirrorCS", {"start": v(17.95, -50.9) * mm, "end": v(13.32, -50.9) * mm});
            skLineSegment(sketch, "E333.MirrorCS", {"start": v(43.35, -50.9) * mm, "end": v(38.72, -50.9) * mm});
            skLineSegment(sketch, "E334.MirrorCS", {"start": v(68.75, -50.9) * mm, "end": v(64.12, -50.9) * mm});
            skLineSegment(sketch, "E335.MirrorCS", {"start": v(94.15, -50.9) * mm, "end": v(89.52, -50.9) * mm});
            skLineSegment(sketch, "E336.MirrorCS", {"start": v(-12.08, -114.4) * mm, "end": v(-12.08, -109.78) * mm});
            skLineSegment(sketch, "E337.MirrorCS", {"start": v(-37.48, -114.4) * mm, "end": v(-37.48, -109.78) * mm});
            skLineSegment(sketch, "E338.MirrorCS", {"start": v(-62.88, -114.4) * mm, "end": v(-62.88, -109.78) * mm});
            skLineSegment(sketch, "E339.MirrorCS", {"start": v(13.32, -50.9) * mm, "end": v(13.32, -46.28) * mm});
            skLineSegment(sketch, "E340.MirrorCS", {"start": v(38.72, -50.9) * mm, "end": v(38.72, -46.28) * mm});
            skLineSegment(sketch, "E341.MirrorCS", {"start": v(76.82, -76.3) * mm, "end": v(76.82, -71.68) * mm});
            skLineSegment(sketch, "E342.MirrorCS", {"start": v(76.82, -25.5) * mm, "end": v(76.82, -20.88) * mm});
            skLineSegment(sketch, "E343.MirrorCS", {"start": v(64.12, -50.9) * mm, "end": v(64.12, -46.28) * mm});
            skLineSegment(sketch, "E344.MirrorCS", {"start": v(89.52, -50.9) * mm, "end": v(89.52, -46.28) * mm});
            skLineSegment(sketch, "E345.MirrorCS", {"start": v(114.92, -50.9) * mm, "end": v(114.92, -46.28) * mm});
            skLineSegment(sketch, "E346.MirrorCS", {"start": v(114.92, -0.1) * mm, "end": v(114.92, 4.52) * mm});
            skLineSegment(sketch, "E347.MirrorCS", {"start": v(17.95, -46.28) * mm, "end": v(13.32, -46.28) * mm});
            skLineSegment(sketch, "E348.MirrorCS", {"start": v(51.53, -115.12) * mm, "end": v(120.27, -46.4) * mm});
            skLineSegment(sketch, "E349.MirrorCS", {"start": v(-45.67, -115.12) * mm, "end": v(51.53, -115.12) * mm});
            skLineSegment(sketch, "E350.MirrorCS", {"start": v(-114.4, -46.4) * mm, "end": v(-45.67, -115.12) * mm});
            skLineSegment(sketch, "E351.MirrorCS", {"start": v(-96.35, -50.9) * mm, "end": v(-96.35, -46.28) * mm});
            skLineSegment(sketch, "E352.MirrorCS", {"start": v(-96.35, -101.7) * mm, "end": v(-96.35, -97.08) * mm});
            skLineSegment(sketch, "E353.MirrorCS", {"start": v(-70.95, -101.7) * mm, "end": v(-70.95, -97.08) * mm});
            skLineSegment(sketch, "E354.MirrorCS", {"start": v(-83.65, -25.5) * mm, "end": v(-83.65, -20.88) * mm});
            skLineSegment(sketch, "E355.MirrorCS", {"start": v(-83.65, -76.3) * mm, "end": v(-83.65, -71.68) * mm});
            skLineSegment(sketch, "E356.MirrorCS", {"start": v(-96.35, -0.1) * mm, "end": v(-96.35, 4.52) * mm});
            skLineSegment(sketch, "E357.MirrorCS", {"start": v(-58.25, -25.5) * mm, "end": v(-58.25, -20.88) * mm});
            skLineSegment(sketch, "E358.MirrorCS", {"start": v(-58.25, -76.3) * mm, "end": v(-58.25, -71.68) * mm});
            skLineSegment(sketch, "E359.MirrorCS", {"start": v(-70.95, -0.1) * mm, "end": v(-70.95, 4.52) * mm});
            skLineSegment(sketch, "E360.MirrorCS", {"start": v(-32.85, -76.3) * mm, "end": v(-32.85, -71.68) * mm});
            skLineSegment(sketch, "E361.MirrorCS", {"start": v(-20.15, -50.9) * mm, "end": v(-20.15, -46.28) * mm});
            skLineSegment(sketch, "E362.MirrorCS", {"start": v(-20.15, -101.7) * mm, "end": v(-20.15, -97.08) * mm});
            skLineSegment(sketch, "E363.MirrorCS", {"start": v(-32.85, -25.5) * mm, "end": v(-32.85, -20.88) * mm});
            skLineSegment(sketch, "E364.MirrorCS", {"start": v(-7.45, -25.5) * mm, "end": v(-7.45, -20.88) * mm});
            skLineSegment(sketch, "E365.MirrorCS", {"start": v(-7.45, -76.3) * mm, "end": v(-7.45, -71.68) * mm});
            skLineSegment(sketch, "E366.MirrorCS", {"start": v(119.55, -114.4) * mm, "end": v(119.55, -109.78) * mm});
            skLineSegment(sketch, "E367.MirrorCS", {"start": v(94.15, -114.4) * mm, "end": v(94.15, -109.78) * mm});
            skLineSegment(sketch, "E368.MirrorCS", {"start": v(56.05, -89) * mm, "end": v(56.05, -84.38) * mm});
            skLineSegment(sketch, "E369.MirrorCS", {"start": v(68.75, -114.4) * mm, "end": v(68.75, -109.78) * mm});
            skLineSegment(sketch, "E370.MirrorCS", {"start": v(43.35, -114.4) * mm, "end": v(43.35, -109.78) * mm});
            skLineSegment(sketch, "E371.MirrorCS", {"start": v(56.05, -38.2) * mm, "end": v(56.05, -33.58) * mm});
            skLineSegment(sketch, "E372.MirrorCS", {"start": v(17.95, -114.4) * mm, "end": v(17.95, -109.78) * mm});
            skLineSegment(sketch, "E373.MirrorCS", {"start": v(-96.35, -46.28) * mm, "end": v(-100.98, -46.28) * mm});
            skLineSegment(sketch, "E374.MirrorCS", {"start": v(-96.35, -97.08) * mm, "end": v(-100.98, -97.08) * mm});
            skLineSegment(sketch, "E375.MirrorCS", {"start": v(-70.95, -97.08) * mm, "end": v(-75.58, -97.08) * mm});
            skLineSegment(sketch, "E376.MirrorCS", {"start": v(-83.65, -20.88) * mm, "end": v(-88.28, -20.88) * mm});
            skLineSegment(sketch, "E377.MirrorCS", {"start": v(-83.65, -71.68) * mm, "end": v(-88.28, -71.68) * mm});
            skLineSegment(sketch, "E378.MirrorCS", {"start": v(-58.25, -20.88) * mm, "end": v(-62.88, -20.88) * mm});
            skLineSegment(sketch, "E379.MirrorCS", {"start": v(-58.25, -71.68) * mm, "end": v(-62.88, -71.68) * mm});
            skLineSegment(sketch, "E380.MirrorCS", {"start": v(-32.85, -71.68) * mm, "end": v(-37.48, -71.68) * mm});
            skLineSegment(sketch, "E381.MirrorCS", {"start": v(-20.15, -46.28) * mm, "end": v(-24.78, -46.28) * mm});
            skLineSegment(sketch, "E382.MirrorCS", {"start": v(-20.15, -97.08) * mm, "end": v(-24.78, -97.08) * mm});
            skLineSegment(sketch, "E383.MirrorCS", {"start": v(-32.85, -20.88) * mm, "end": v(-37.48, -20.88) * mm});
            skLineSegment(sketch, "E384.MirrorCS", {"start": v(-7.45, -71.68) * mm, "end": v(-12.08, -71.68) * mm});
            skLineSegment(sketch, "E385.MirrorCS", {"start": v(119.55, -109.78) * mm, "end": v(114.92, -109.78) * mm});
            skLineSegment(sketch, "E386.MirrorCS", {"start": v(94.15, -109.78) * mm, "end": v(89.52, -109.78) * mm});
            skLineSegment(sketch, "E387.MirrorCS", {"start": v(106.85, -33.58) * mm, "end": v(102.22, -33.58) * mm});
            skLineSegment(sketch, "E388.MirrorCS", {"start": v(106.85, -84.38) * mm, "end": v(102.22, -84.38) * mm});
            skLineSegment(sketch, "E389.MirrorCS", {"start": v(56.05, -84.38) * mm, "end": v(51.42, -84.38) * mm});
            skLineSegment(sketch, "E390.MirrorCS", {"start": v(68.75, -109.78) * mm, "end": v(64.12, -109.78) * mm});
            skLineSegment(sketch, "E391.MirrorCS", {"start": v(43.35, -109.78) * mm, "end": v(38.72, -109.78) * mm});
            skLineSegment(sketch, "E392.MirrorCS", {"start": v(56.05, -33.58) * mm, "end": v(51.42, -33.58) * mm});
            skLineSegment(sketch, "E393.MirrorCS", {"start": v(17.95, -109.78) * mm, "end": v(13.32, -109.78) * mm});
            skLineSegment(sketch, "E394.MirrorCS", {"start": v(30.65, -33.58) * mm, "end": v(26.02, -33.58) * mm});
            skLineSegment(sketch, "E395.MirrorCS", {"start": v(30.65, -84.38) * mm, "end": v(26.02, -84.38) * mm});
            skLineSegment(sketch, "E396.MirrorCS", {"start": v(-75.58, -101.7) * mm, "end": v(-75.58, -97.08) * mm});
            skLineSegment(sketch, "E397.MirrorCS", {"start": v(-88.28, -25.5) * mm, "end": v(-88.28, -20.88) * mm});
            skLineSegment(sketch, "E398.MirrorCS", {"start": v(-88.28, -76.3) * mm, "end": v(-88.28, -71.68) * mm});
            skLineSegment(sketch, "E399.MirrorCS", {"start": v(-100.98, -0.1) * mm, "end": v(-100.98, 4.52) * mm});
            skLineSegment(sketch, "E400.MirrorCS", {"start": v(-62.88, -25.5) * mm, "end": v(-62.88, -20.88) * mm});
            skLineSegment(sketch, "E401.MirrorCS", {"start": v(-62.88, -76.3) * mm, "end": v(-62.88, -71.68) * mm});
            skLineSegment(sketch, "E402.MirrorCS", {"start": v(-75.58, -0.1) * mm, "end": v(-75.58, 4.52) * mm});
            skLineSegment(sketch, "E403.MirrorCS", {"start": v(-37.48, -76.3) * mm, "end": v(-37.48, -71.68) * mm});
            skLineSegment(sketch, "E404.MirrorCS", {"start": v(-24.78, -50.9) * mm, "end": v(-24.78, -46.28) * mm});
            skLineSegment(sketch, "E405.MirrorCS", {"start": v(-24.78, -101.7) * mm, "end": v(-24.78, -97.08) * mm});
            skLineSegment(sketch, "E406.MirrorCS", {"start": v(-37.48, -25.5) * mm, "end": v(-37.48, -20.88) * mm});
            skLineSegment(sketch, "E407.MirrorCS", {"start": v(-12.08, -76.3) * mm, "end": v(-12.08, -71.68) * mm});
            skLineSegment(sketch, "E408.MirrorCS", {"start": v(114.92, -114.4) * mm, "end": v(114.92, -109.78) * mm});
            skLineSegment(sketch, "E409.MirrorCS", {"start": v(89.52, -114.4) * mm, "end": v(89.52, -109.78) * mm});
            skLineSegment(sketch, "E410.MirrorCS", {"start": v(-100.98, -50.9) * mm, "end": v(-100.98, -46.28) * mm});
            skLineSegment(sketch, "E411.MirrorCS", {"start": v(-100.98, -101.7) * mm, "end": v(-100.98, -97.08) * mm});
            skLineSegment(sketch, "E412.MirrorCS", {"start": v(51.42, -89) * mm, "end": v(51.42, -84.38) * mm});
            skLineSegment(sketch, "E413.MirrorCS", {"start": v(64.12, -114.4) * mm, "end": v(64.12, -109.78) * mm});
            skLineSegment(sketch, "E414.MirrorCS", {"start": v(38.72, -114.4) * mm, "end": v(38.72, -109.78) * mm});
            skLineSegment(sketch, "E415.MirrorCS", {"start": v(51.42, -38.2) * mm, "end": v(51.42, -33.58) * mm});
            skLineSegment(sketch, "E416.MirrorCS", {"start": v(13.32, -114.4) * mm, "end": v(13.32, -109.78) * mm});
            skLineSegment(sketch, "E417.MirrorCS", {"start": v(-58.25, -25.5) * mm, "end": v(-62.88, -25.5) * mm});
            skLineSegment(sketch, "E418.MirrorCS", {"start": v(-58.25, -76.3) * mm, "end": v(-62.88, -76.3) * mm});
            skLineSegment(sketch, "E419.MirrorCS", {"start": v(-32.85, -76.3) * mm, "end": v(-37.48, -76.3) * mm});
            skLineSegment(sketch, "E420.MirrorCS", {"start": v(-20.15, -50.9) * mm, "end": v(-24.78, -50.9) * mm});
            skLineSegment(sketch, "E421.MirrorCS", {"start": v(-20.15, -101.7) * mm, "end": v(-24.78, -101.7) * mm});
            skLineSegment(sketch, "E422.MirrorCS", {"start": v(-32.85, -25.5) * mm, "end": v(-37.48, -25.5) * mm});
            skLineSegment(sketch, "E423.MirrorCS", {"start": v(-7.45, -76.3) * mm, "end": v(-12.08, -76.3) * mm});
            skLineSegment(sketch, "E424.MirrorCS", {"start": v(119.55, -114.4) * mm, "end": v(114.92, -114.4) * mm});
            skLineSegment(sketch, "E425.MirrorCS", {"start": v(94.15, -114.4) * mm, "end": v(89.52, -114.4) * mm});
            skLineSegment(sketch, "E426.MirrorCS", {"start": v(0.62, 4.52) * mm, "end": v(-12.08, 4.52) * mm, "construction": true});
            skLineSegment(sketch, "E427.MirrorCS", {"start": v(-96.35, -50.9) * mm, "end": v(-100.98, -50.9) * mm});
            skLineSegment(sketch, "E428.MirrorCS", {"start": v(-96.35, -101.7) * mm, "end": v(-100.98, -101.7) * mm});
            skLineSegment(sketch, "E429.MirrorCS", {"start": v(-70.95, -101.7) * mm, "end": v(-75.58, -101.7) * mm});
            skLineSegment(sketch, "E430.MirrorCS", {"start": v(-83.65, -25.5) * mm, "end": v(-88.28, -25.5) * mm});
            skLineSegment(sketch, "E431.MirrorCS", {"start": v(-83.65, -76.3) * mm, "end": v(-88.28, -76.3) * mm});
            skLineSegment(sketch, "E432.MirrorCS", {"start": v(56.05, -89) * mm, "end": v(51.42, -89) * mm});
            skLineSegment(sketch, "E433.MirrorCS", {"start": v(68.75, -114.4) * mm, "end": v(64.12, -114.4) * mm});
            skLineSegment(sketch, "E434.MirrorCS", {"start": v(43.35, -114.4) * mm, "end": v(38.72, -114.4) * mm});
            skLineSegment(sketch, "E435.MirrorCS", {"start": v(56.05, -38.2) * mm, "end": v(51.42, -38.2) * mm});
            skLineSegment(sketch, "E436.MirrorCS", {"start": v(-32.85, -63.6) * mm, "end": v(-32.85, -58.98) * mm});
            skLineSegment(sketch, "E437.MirrorCS", {"start": v(-45.55, -38.2) * mm, "end": v(-45.55, -33.58) * mm});
            skLineSegment(sketch, "E438.MirrorCS", {"start": v(-45.55, -89) * mm, "end": v(-45.55, -84.38) * mm});
            skLineSegment(sketch, "E439.MirrorCS", {"start": v(-7.45, -114.4) * mm, "end": v(-7.45, -109.78) * mm});
            skLineSegment(sketch, "E440.MirrorCS", {"start": v(-20.15, -38.2) * mm, "end": v(-20.15, -33.58) * mm});
            skLineSegment(sketch, "E441.MirrorCS", {"start": v(-20.15, -89) * mm, "end": v(-20.15, -84.38) * mm});
            skLineSegment(sketch, "E442.MirrorCS", {"start": v(-32.85, -12.8) * mm, "end": v(-32.85, -8.18) * mm});
            skLineSegment(sketch, "E443.MirrorCS", {"start": v(119.55, -101.7) * mm, "end": v(119.55, -97.08) * mm});
            skLineSegment(sketch, "E444.MirrorCS", {"start": v(94.15, -101.7) * mm, "end": v(94.15, -97.08) * mm});
            skLineSegment(sketch, "E445.MirrorCS", {"start": v(94.15, -0.1) * mm, "end": v(94.15, 4.52) * mm});
            skLineSegment(sketch, "E446.MirrorCS", {"start": v(56.05, -76.3) * mm, "end": v(56.05, -71.68) * mm});
            skLineSegment(sketch, "E447.MirrorCS", {"start": v(68.75, -0.1) * mm, "end": v(68.75, 4.52) * mm});
            skLineSegment(sketch, "E448.MirrorCS", {"start": v(68.75, -50.9) * mm, "end": v(68.75, -46.28) * mm});
            skLineSegment(sketch, "E449.MirrorCS", {"start": v(68.75, -101.7) * mm, "end": v(68.75, -97.08) * mm});
            skLineSegment(sketch, "E450.MirrorCS", {"start": v(-96.35, -38.2) * mm, "end": v(-96.35, -33.58) * mm});
            skLineSegment(sketch, "E451.MirrorCS", {"start": v(-96.35, -89) * mm, "end": v(-96.35, -84.38) * mm});
            skLineSegment(sketch, "E452.MirrorCS", {"start": v(-109.05, -12.8) * mm, "end": v(-109.05, -8.18) * mm});
            skLineSegment(sketch, "E453.MirrorCS", {"start": v(-109.05, -63.6) * mm, "end": v(-109.05, -58.98) * mm});
            skLineSegment(sketch, "E454.MirrorCS", {"start": v(-83.65, -12.8) * mm, "end": v(-83.65, -8.18) * mm});
            skLineSegment(sketch, "E455.MirrorCS", {"start": v(-83.65, -63.6) * mm, "end": v(-83.65, -58.98) * mm});
            skLineSegment(sketch, "E456.MirrorCS", {"start": v(-83.65, -114.4) * mm, "end": v(-83.65, -109.78) * mm});
            skLineSegment(sketch, "E457.MirrorCS", {"start": v(-58.25, -12.8) * mm, "end": v(-58.25, -8.18) * mm});
            skLineSegment(sketch, "E458.MirrorCS", {"start": v(-58.25, -63.6) * mm, "end": v(-58.25, -58.98) * mm});
            skLineSegment(sketch, "E459.MirrorCS", {"start": v(43.35, -0.1) * mm, "end": v(43.35, 4.52) * mm});
            skLineSegment(sketch, "E460.MirrorCS", {"start": v(43.35, -50.9) * mm, "end": v(43.35, -46.28) * mm});
            skLineSegment(sketch, "E461.MirrorCS", {"start": v(43.35, -101.7) * mm, "end": v(43.35, -97.08) * mm});
            skLineSegment(sketch, "E462.MirrorCS", {"start": v(56.05, -25.5) * mm, "end": v(56.05, -20.88) * mm});
            skLineSegment(sketch, "E463.MirrorCS", {"start": v(17.95, -101.7) * mm, "end": v(17.95, -97.08) * mm});
            skLineSegment(sketch, "E464.MirrorCS", {"start": v(17.95, -0.1) * mm, "end": v(17.95, 4.52) * mm});
            skLineSegment(sketch, "E465.MirrorCS", {"start": v(-20.15, -33.58) * mm, "end": v(-24.78, -33.58) * mm});
            skLineSegment(sketch, "E466.MirrorCS", {"start": v(-20.15, -84.38) * mm, "end": v(-24.78, -84.38) * mm});
            skLineSegment(sketch, "E467.MirrorCS", {"start": v(-32.85, -8.18) * mm, "end": v(-37.48, -8.18) * mm});
            skLineSegment(sketch, "E468.MirrorCS", {"start": v(119.55, -97.08) * mm, "end": v(114.92, -97.08) * mm});
            skLineSegment(sketch, "E469.MirrorCS", {"start": v(94.15, -97.08) * mm, "end": v(89.52, -97.08) * mm});
            skLineSegment(sketch, "E470.MirrorCS", {"start": v(106.85, -20.88) * mm, "end": v(102.22, -20.88) * mm});
            skLineSegment(sketch, "E471.MirrorCS", {"start": v(106.85, -71.68) * mm, "end": v(102.22, -71.68) * mm});
            skLineSegment(sketch, "E472.MirrorCS", {"start": v(56.05, -71.68) * mm, "end": v(51.42, -71.68) * mm});
            skLineSegment(sketch, "E473.MirrorCS", {"start": v(68.75, -97.08) * mm, "end": v(64.12, -97.08) * mm});
            skLineSegment(sketch, "E474.MirrorCS", {"start": v(43.35, -97.08) * mm, "end": v(38.72, -97.08) * mm});
            skLineSegment(sketch, "E475.MirrorCS", {"start": v(56.05, -20.88) * mm, "end": v(51.42, -20.88) * mm});
            skLineSegment(sketch, "E476.MirrorCS", {"start": v(-96.35, -33.58) * mm, "end": v(-100.98, -33.58) * mm});
            skLineSegment(sketch, "E477.MirrorCS", {"start": v(-96.35, -84.38) * mm, "end": v(-100.98, -84.38) * mm});
            skLineSegment(sketch, "E478.MirrorCS", {"start": v(-109.05, -8.18) * mm, "end": v(-113.68, -8.18) * mm});
            skLineSegment(sketch, "E479.MirrorCS", {"start": v(-109.05, -58.98) * mm, "end": v(-113.68, -58.98) * mm});
            skLineSegment(sketch, "E480.MirrorCS", {"start": v(-83.65, -8.18) * mm, "end": v(-88.28, -8.18) * mm});
            skLineSegment(sketch, "E481.MirrorCS", {"start": v(-83.65, -58.98) * mm, "end": v(-88.28, -58.98) * mm});
            skLineSegment(sketch, "E482.MirrorCS", {"start": v(-58.25, -8.18) * mm, "end": v(-62.88, -8.18) * mm});
            skLineSegment(sketch, "E483.MirrorCS", {"start": v(-58.25, -58.98) * mm, "end": v(-62.88, -58.98) * mm});
            skLineSegment(sketch, "E484.MirrorCS", {"start": v(-32.85, -58.98) * mm, "end": v(-37.48, -58.98) * mm});
            skLineSegment(sketch, "E485.MirrorCS", {"start": v(-45.55, -33.58) * mm, "end": v(-50.18, -33.58) * mm});
            skLineSegment(sketch, "E486.MirrorCS", {"start": v(-45.55, -84.38) * mm, "end": v(-50.18, -84.38) * mm});
            skLineSegment(sketch, "E487.MirrorCS", {"start": v(119.55, -76.3) * mm, "end": v(114.92, -76.3) * mm});
            skLineSegment(sketch, "E488.MirrorCS", {"start": v(119.55, -25.5) * mm, "end": v(114.92, -25.5) * mm});
            skLineSegment(sketch, "E489.MirrorCS", {"start": v(-7.45, -89) * mm, "end": v(-12.08, -89) * mm});
            skLineSegment(sketch, "E490.MirrorCS", {"start": v(-7.45, -38.2) * mm, "end": v(-12.08, -38.2) * mm});
            skLineSegment(sketch, "E491.MirrorCS", {"start": v(-32.85, -89) * mm, "end": v(-37.48, -89) * mm});
            skLineSegment(sketch, "E492.MirrorCS", {"start": v(-32.85, -38.2) * mm, "end": v(-37.48, -38.2) * mm});
            skLineSegment(sketch, "E493.MirrorCS", {"start": v(-58.25, -38.2) * mm, "end": v(-62.88, -38.2) * mm});
            skLineSegment(sketch, "E494.MirrorCS", {"start": v(-45.55, -63.6) * mm, "end": v(-50.18, -63.6) * mm});
            skLineSegment(sketch, "E495.MirrorCS", {"start": v(-45.55, -12.8) * mm, "end": v(-50.18, -12.8) * mm});
            skLineSegment(sketch, "E496.MirrorCS", {"start": v(-58.25, -89) * mm, "end": v(-62.88, -89) * mm});
            skLineSegment(sketch, "E497.MirrorCS", {"start": v(-96.35, -12.8) * mm, "end": v(-100.98, -12.8) * mm});
            skLineSegment(sketch, "E498.MirrorCS", {"start": v(-83.65, -89) * mm, "end": v(-88.28, -89) * mm});
            skLineSegment(sketch, "E499.MirrorCS", {"start": v(-83.65, -38.2) * mm, "end": v(-88.28, -38.2) * mm});
            skLineSegment(sketch, "E500.MirrorCS", {"start": v(17.95, -76.3) * mm, "end": v(13.32, -76.3) * mm});
            skLineSegment(sketch, "E501.MirrorCS", {"start": v(17.95, -25.5) * mm, "end": v(13.32, -25.5) * mm});
            skLineSegment(sketch, "E502.MirrorCS", {"start": v(43.35, -25.5) * mm, "end": v(38.72, -25.5) * mm});
            skLineSegment(sketch, "E503.MirrorCS", {"start": v(56.05, -101.7) * mm, "end": v(51.42, -101.7) * mm});
            skLineSegment(sketch, "E504.MirrorCS", {"start": v(43.35, -76.3) * mm, "end": v(38.72, -76.3) * mm});
            skLineSegment(sketch, "E505.MirrorCS", {"start": v(68.75, -76.3) * mm, "end": v(64.12, -76.3) * mm});
            skLineSegment(sketch, "E506.MirrorCS", {"start": v(68.75, -25.5) * mm, "end": v(64.12, -25.5) * mm});
            skLineSegment(sketch, "E507.MirrorCS", {"start": v(94.15, -76.3) * mm, "end": v(89.52, -76.3) * mm});
            skLineSegment(sketch, "E508.MirrorCS", {"start": v(94.15, -25.5) * mm, "end": v(89.52, -25.5) * mm});
            skLineSegment(sketch, "E509.MirrorCS", {"start": v(81.45, -101.7) * mm, "end": v(76.82, -101.7) * mm});
            skLineSegment(sketch, "E510.MirrorCS", {"start": v(-109.05, -38.2) * mm, "end": v(-113.68, -38.2) * mm});
            skLineSegment(sketch, "E511.MirrorCS", {"start": v(-24.78, -12.8) * mm, "end": v(-24.78, -8.18) * mm});
            skLineSegment(sketch, "E512.MirrorCS", {"start": v(-12.08, -89) * mm, "end": v(-12.08, -84.38) * mm});
            skLineSegment(sketch, "E513.MirrorCS", {"start": v(-12.08, -38.2) * mm, "end": v(-12.08, -33.58) * mm});
            skLineSegment(sketch, "E514.MirrorCS", {"start": v(-37.48, -89) * mm, "end": v(-37.48, -84.38) * mm});
            skLineSegment(sketch, "E515.MirrorCS", {"start": v(-37.48, -38.2) * mm, "end": v(-37.48, -33.58) * mm});
            skLineSegment(sketch, "E516.MirrorCS", {"start": v(-62.88, -38.2) * mm, "end": v(-62.88, -33.58) * mm});
            skLineSegment(sketch, "E517.MirrorCS", {"start": v(-50.18, -63.6) * mm, "end": v(-50.18, -58.98) * mm});
            skLineSegment(sketch, "E518.MirrorCS", {"start": v(-50.18, -12.8) * mm, "end": v(-50.18, -8.18) * mm});
            skLineSegment(sketch, "E519.MirrorCS", {"start": v(-62.88, -89) * mm, "end": v(-62.88, -84.38) * mm});
            skLineSegment(sketch, "E520.MirrorCS", {"start": v(-100.98, -63.6) * mm, "end": v(-100.98, -58.98) * mm});
            skLineSegment(sketch, "E521.MirrorCS", {"start": v(-100.98, -12.8) * mm, "end": v(-100.98, -8.18) * mm});
            skLineSegment(sketch, "E522.MirrorCS", {"start": v(-88.28, -89) * mm, "end": v(-88.28, -84.38) * mm});
            skLineSegment(sketch, "E523.MirrorCS", {"start": v(-88.28, -38.2) * mm, "end": v(-88.28, -33.58) * mm});
            skLineSegment(sketch, "E524.MirrorCS", {"start": v(-113.68, -38.2) * mm, "end": v(-113.68, -33.58) * mm});
            skLineSegment(sketch, "E525.MirrorCS", {"start": v(13.32, -76.3) * mm, "end": v(13.32, -71.68) * mm});
            skLineSegment(sketch, "E526.MirrorCS", {"start": v(13.32, -25.5) * mm, "end": v(13.32, -20.88) * mm});
            skLineSegment(sketch, "E527.MirrorCS", {"start": v(38.72, -25.5) * mm, "end": v(38.72, -20.88) * mm});
            skLineSegment(sketch, "E528.MirrorCS", {"start": v(51.42, -101.7) * mm, "end": v(51.42, -97.08) * mm});
            skLineSegment(sketch, "E529.MirrorCS", {"start": v(51.42, -0.1) * mm, "end": v(51.42, 4.52) * mm});
            skLineSegment(sketch, "E530.MirrorCS", {"start": v(38.72, -76.3) * mm, "end": v(38.72, -71.68) * mm});
            skLineSegment(sketch, "E531.MirrorCS", {"start": v(64.12, -76.3) * mm, "end": v(64.12, -71.68) * mm});
            skLineSegment(sketch, "E532.MirrorCS", {"start": v(64.12, -25.5) * mm, "end": v(64.12, -20.88) * mm});
            skLineSegment(sketch, "E533.MirrorCS", {"start": v(89.52, -76.3) * mm, "end": v(89.52, -71.68) * mm});
            skLineSegment(sketch, "E534.MirrorCS", {"start": v(89.52, -25.5) * mm, "end": v(89.52, -20.88) * mm});
            skLineSegment(sketch, "E535.MirrorCS", {"start": v(114.92, -76.3) * mm, "end": v(114.92, -71.68) * mm});
            skLineSegment(sketch, "E536.MirrorCS", {"start": v(114.92, -25.5) * mm, "end": v(114.92, -20.88) * mm});
            skLineSegment(sketch, "E537.MirrorCS", {"start": v(-7.45, -84.38) * mm, "end": v(-12.08, -84.38) * mm});
            skLineSegment(sketch, "E538.MirrorCS", {"start": v(-7.45, -33.58) * mm, "end": v(-12.08, -33.58) * mm});
            skLineSegment(sketch, "E539.MirrorCS", {"start": v(-32.85, -84.38) * mm, "end": v(-37.48, -84.38) * mm});
            skLineSegment(sketch, "E540.MirrorCS", {"start": v(-32.85, -33.58) * mm, "end": v(-37.48, -33.58) * mm});
            skLineSegment(sketch, "E541.MirrorCS", {"start": v(-58.25, -33.58) * mm, "end": v(-62.88, -33.58) * mm});
            skLineSegment(sketch, "E542.MirrorCS", {"start": v(-45.55, -58.98) * mm, "end": v(-50.18, -58.98) * mm});
            skLineSegment(sketch, "E543.MirrorCS", {"start": v(-45.55, -8.18) * mm, "end": v(-50.18, -8.18) * mm});
            skLineSegment(sketch, "E544.MirrorCS", {"start": v(-58.25, -84.38) * mm, "end": v(-62.88, -84.38) * mm});
            skLineSegment(sketch, "E545.MirrorCS", {"start": v(-96.35, -58.98) * mm, "end": v(-100.98, -58.98) * mm});
            skLineSegment(sketch, "E546.MirrorCS", {"start": v(-96.35, -8.18) * mm, "end": v(-100.98, -8.18) * mm});
            skLineSegment(sketch, "E547.MirrorCS", {"start": v(-83.65, -84.38) * mm, "end": v(-88.28, -84.38) * mm});
            skLineSegment(sketch, "E548.MirrorCS", {"start": v(-83.65, -33.58) * mm, "end": v(-88.28, -33.58) * mm});
            skLineSegment(sketch, "E549.MirrorCS", {"start": v(-109.05, -84.38) * mm, "end": v(-113.68, -84.38) * mm});
            skLineSegment(sketch, "E550.MirrorCS", {"start": v(-109.05, -33.58) * mm, "end": v(-113.68, -33.58) * mm});
            skLineSegment(sketch, "E551.MirrorCS", {"start": v(17.95, -71.68) * mm, "end": v(13.32, -71.68) * mm});
            skLineSegment(sketch, "E552.MirrorCS", {"start": v(17.95, -20.88) * mm, "end": v(13.32, -20.88) * mm});
            skLineSegment(sketch, "E553.MirrorCS", {"start": v(43.35, -20.88) * mm, "end": v(38.72, -20.88) * mm});
            skLineSegment(sketch, "E554.MirrorCS", {"start": v(30.65, -97.08) * mm, "end": v(26.02, -97.08) * mm});
            skLineSegment(sketch, "E555.MirrorCS", {"start": v(56.05, -97.08) * mm, "end": v(51.42, -97.08) * mm});
            skLineSegment(sketch, "E556.MirrorCS", {"start": v(43.35, -71.68) * mm, "end": v(38.72, -71.68) * mm});
            skLineSegment(sketch, "E557.MirrorCS", {"start": v(68.75, -71.68) * mm, "end": v(64.12, -71.68) * mm});
            skLineSegment(sketch, "E558.MirrorCS", {"start": v(68.75, -20.88) * mm, "end": v(64.12, -20.88) * mm});
            skLineSegment(sketch, "E559.MirrorCS", {"start": v(94.15, -71.68) * mm, "end": v(89.52, -71.68) * mm});
            skLineSegment(sketch, "E560.MirrorCS", {"start": v(94.15, -20.88) * mm, "end": v(89.52, -20.88) * mm});
            skLineSegment(sketch, "E561.MirrorCS", {"start": v(119.55, -71.68) * mm, "end": v(114.92, -71.68) * mm});
            skLineSegment(sketch, "E562.MirrorCS", {"start": v(119.55, -20.88) * mm, "end": v(114.92, -20.88) * mm});
            skLineSegment(sketch, "E563.MirrorCS", {"start": v(106.85, -97.08) * mm, "end": v(102.22, -97.08) * mm});
            skLineSegment(sketch, "E564.MirrorCS", {"start": v(43.35, -25.5) * mm, "end": v(43.35, -20.88) * mm});
            skLineSegment(sketch, "E565.MirrorCS", {"start": v(56.05, -101.7) * mm, "end": v(56.05, -97.08) * mm});
            skLineSegment(sketch, "E566.MirrorCS", {"start": v(56.05, -0.1) * mm, "end": v(56.05, 4.52) * mm});
            skLineSegment(sketch, "E567.MirrorCS", {"start": v(56.05, -50.9) * mm, "end": v(56.05, -46.28) * mm});
            skLineSegment(sketch, "E568.MirrorCS", {"start": v(43.35, -76.3) * mm, "end": v(43.35, -71.68) * mm});
            skLineSegment(sketch, "E569.MirrorCS", {"start": v(68.75, -76.3) * mm, "end": v(68.75, -71.68) * mm});
            skLineSegment(sketch, "E570.MirrorCS", {"start": v(68.75, -25.5) * mm, "end": v(68.75, -20.88) * mm});
            skLineSegment(sketch, "E571.MirrorCS", {"start": v(94.15, -76.3) * mm, "end": v(94.15, -71.68) * mm});
            skLineSegment(sketch, "E572.MirrorCS", {"start": v(94.15, -25.5) * mm, "end": v(94.15, -20.88) * mm});
            skLineSegment(sketch, "E573.MirrorCS", {"start": v(119.55, -76.3) * mm, "end": v(119.55, -71.68) * mm});
            skLineSegment(sketch, "E574.MirrorCS", {"start": v(119.55, -25.5) * mm, "end": v(119.55, -20.88) * mm});
            skLineSegment(sketch, "E575.MirrorCS", {"start": v(-7.45, -89) * mm, "end": v(-7.45, -84.38) * mm});
            skLineSegment(sketch, "E576.MirrorCS", {"start": v(-7.45, -38.2) * mm, "end": v(-7.45, -33.58) * mm});
            skLineSegment(sketch, "E577.MirrorCS", {"start": v(17.95, -76.3) * mm, "end": v(17.95, -71.68) * mm});
            skLineSegment(sketch, "E578.MirrorCS", {"start": v(17.95, -25.5) * mm, "end": v(17.95, -20.88) * mm});
            skLineSegment(sketch, "E579.MirrorCS", {"start": v(-32.85, -89) * mm, "end": v(-32.85, -84.38) * mm});
            skLineSegment(sketch, "E580.MirrorCS", {"start": v(-32.85, -38.2) * mm, "end": v(-32.85, -33.58) * mm});
            skLineSegment(sketch, "E581.MirrorCS", {"start": v(-58.25, -38.2) * mm, "end": v(-58.25, -33.58) * mm});
            skLineSegment(sketch, "E582.MirrorCS", {"start": v(-45.55, -63.6) * mm, "end": v(-45.55, -58.98) * mm});
            skLineSegment(sketch, "E583.MirrorCS", {"start": v(-45.55, -12.8) * mm, "end": v(-45.55, -8.18) * mm});
            skLineSegment(sketch, "E584.MirrorCS", {"start": v(-58.25, -89) * mm, "end": v(-58.25, -84.38) * mm});
            skLineSegment(sketch, "E585.MirrorCS", {"start": v(-96.35, -63.6) * mm, "end": v(-96.35, -58.98) * mm});
            skLineSegment(sketch, "E586.MirrorCS", {"start": v(-96.35, -12.8) * mm, "end": v(-96.35, -8.18) * mm});
            skLineSegment(sketch, "E587.MirrorCS", {"start": v(-83.65, -89) * mm, "end": v(-83.65, -84.38) * mm});
            skLineSegment(sketch, "E588.MirrorCS", {"start": v(-83.65, -38.2) * mm, "end": v(-83.65, -33.58) * mm});
            skLineSegment(sketch, "E589.MirrorCS", {"start": v(-109.05, -38.2) * mm, "end": v(-109.05, -33.58) * mm});
            skLineSegment(sketch, "E590.MirrorCS", {"start": v(-96.35, -114.4) * mm, "end": v(-96.35, -109.78) * mm});
            skLineSegment(sketch, "E591.MirrorCS", {"start": v(43.35, -89) * mm, "end": v(38.72, -89) * mm});
            skLineSegment(sketch, "E592.MirrorCS", {"start": v(68.75, -89) * mm, "end": v(64.12, -89) * mm});
            skLineSegment(sketch, "E593.MirrorCS", {"start": v(68.75, -38.2) * mm, "end": v(64.12, -38.2) * mm});
            skLineSegment(sketch, "E594.MirrorCS", {"start": v(94.15, -89) * mm, "end": v(89.52, -89) * mm});
            skLineSegment(sketch, "E595.MirrorCS", {"start": v(94.15, -38.2) * mm, "end": v(89.52, -38.2) * mm});
            skLineSegment(sketch, "E596.MirrorCS", {"start": v(119.55, -89) * mm, "end": v(114.92, -89) * mm});
            skLineSegment(sketch, "E597.MirrorCS", {"start": v(119.55, -38.2) * mm, "end": v(114.92, -38.2) * mm});
            skLineSegment(sketch, "E598.MirrorCS", {"start": v(-7.45, -50.9) * mm, "end": v(-12.08, -50.9) * mm});
            skLineSegment(sketch, "E599.MirrorCS", {"start": v(-7.45, -101.7) * mm, "end": v(-12.08, -101.7) * mm});
            skLineSegment(sketch, "E600.MirrorCS", {"start": v(-32.85, -101.7) * mm, "end": v(-37.48, -101.7) * mm});
            skLineSegment(sketch, "E601.MirrorCS", {"start": v(-20.15, -76.3) * mm, "end": v(-24.78, -76.3) * mm});
            skLineSegment(sketch, "E602.MirrorCS", {"start": v(17.95, -89) * mm, "end": v(13.32, -89) * mm});
            skLineSegment(sketch, "E603.MirrorCS", {"start": v(17.95, -38.2) * mm, "end": v(13.32, -38.2) * mm});
            skLineSegment(sketch, "E604.MirrorCS", {"start": v(43.35, -38.2) * mm, "end": v(38.72, -38.2) * mm});
            skLineSegment(sketch, "E605.MirrorCS", {"start": v(-70.95, -76.3) * mm, "end": v(-75.58, -76.3) * mm});
            skLineSegment(sketch, "E606.MirrorCS", {"start": v(-70.95, -25.5) * mm, "end": v(-75.58, -25.5) * mm});
            skLineSegment(sketch, "E607.MirrorCS", {"start": v(-58.25, -101.7) * mm, "end": v(-62.88, -101.7) * mm});
            skLineSegment(sketch, "E608.MirrorCS", {"start": v(-96.35, -76.3) * mm, "end": v(-100.98, -76.3) * mm});
            skLineSegment(sketch, "E609.MirrorCS", {"start": v(-96.35, -25.5) * mm, "end": v(-100.98, -25.5) * mm});
            skLineSegment(sketch, "E610.MirrorCS", {"start": v(-83.65, -101.7) * mm, "end": v(-88.28, -101.7) * mm});
            skLineSegment(sketch, "E611.MirrorCS", {"start": v(64.12, -89) * mm, "end": v(64.12, -84.38) * mm});
            skLineSegment(sketch, "E612.MirrorCS", {"start": v(64.12, -38.2) * mm, "end": v(64.12, -33.58) * mm});
            skLineSegment(sketch, "E613.MirrorCS", {"start": v(89.52, -89) * mm, "end": v(89.52, -84.38) * mm});
            skLineSegment(sketch, "E614.MirrorCS", {"start": v(89.52, -38.2) * mm, "end": v(89.52, -33.58) * mm});
            skLineSegment(sketch, "E615.MirrorCS", {"start": v(114.92, -89) * mm, "end": v(114.92, -84.38) * mm});
            skLineSegment(sketch, "E616.MirrorCS", {"start": v(114.92, -38.2) * mm, "end": v(114.92, -33.58) * mm});
            skLineSegment(sketch, "E617.MirrorCS", {"start": v(-12.08, -50.9) * mm, "end": v(-12.08, -46.28) * mm});
            skLineSegment(sketch, "E618.MirrorCS", {"start": v(-12.08, -101.7) * mm, "end": v(-12.08, -97.08) * mm});
            skLineSegment(sketch, "E619.MirrorCS", {"start": v(-37.48, -101.7) * mm, "end": v(-37.48, -97.08) * mm});
            skLineSegment(sketch, "E620.MirrorCS", {"start": v(-37.48, -50.9) * mm, "end": v(-37.48, -46.28) * mm});
            skLineSegment(sketch, "E621.MirrorCS", {"start": v(-37.48, -0.1) * mm, "end": v(-37.48, 4.52) * mm});
            skLineSegment(sketch, "E622.MirrorCS", {"start": v(-24.78, -76.3) * mm, "end": v(-24.78, -71.68) * mm});
            skLineSegment(sketch, "E623.MirrorCS", {"start": v(-62.88, -0.1) * mm, "end": v(-62.88, 4.52) * mm});
            skLineSegment(sketch, "E624.MirrorCS", {"start": v(13.32, -89) * mm, "end": v(13.32, -84.38) * mm});
            skLineSegment(sketch, "E625.MirrorCS", {"start": v(13.32, -38.2) * mm, "end": v(13.32, -33.58) * mm});
            skLineSegment(sketch, "E626.MirrorCS", {"start": v(38.72, -38.2) * mm, "end": v(38.72, -33.58) * mm});
            skLineSegment(sketch, "E627.MirrorCS", {"start": v(38.72, -89) * mm, "end": v(38.72, -84.38) * mm});
            skLineSegment(sketch, "E628.MirrorCS", {"start": v(-88.28, -0.1) * mm, "end": v(-88.28, 4.52) * mm});
            skLineSegment(sketch, "E629.MirrorCS", {"start": v(-75.58, -76.3) * mm, "end": v(-75.58, -71.68) * mm});
            skLineSegment(sketch, "E630.MirrorCS", {"start": v(-75.58, -25.5) * mm, "end": v(-75.58, -20.88) * mm});
            skLineSegment(sketch, "E631.MirrorCS", {"start": v(-62.88, -101.7) * mm, "end": v(-62.88, -97.08) * mm});
            skLineSegment(sketch, "E632.MirrorCS", {"start": v(-100.98, -76.3) * mm, "end": v(-100.98, -71.68) * mm});
            skLineSegment(sketch, "E633.MirrorCS", {"start": v(-100.98, -25.5) * mm, "end": v(-100.98, -20.88) * mm});
            skLineSegment(sketch, "E634.MirrorCS", {"start": v(-88.28, -101.7) * mm, "end": v(-88.28, -97.08) * mm});
            skLineSegment(sketch, "E635.MirrorCS", {"start": v(-88.28, -50.9) * mm, "end": v(-88.28, -46.28) * mm});
            skLineSegment(sketch, "E636.MirrorCS", {"start": v(94.15, -33.58) * mm, "end": v(89.52, -33.58) * mm});
            skLineSegment(sketch, "E637.MirrorCS", {"start": v(94.15, -84.38) * mm, "end": v(89.52, -84.38) * mm});
            skLineSegment(sketch, "E638.MirrorCS", {"start": v(119.55, -84.38) * mm, "end": v(114.92, -84.38) * mm});
            skLineSegment(sketch, "E639.MirrorCS", {"start": v(119.55, -33.58) * mm, "end": v(114.92, -33.58) * mm});
            skLineSegment(sketch, "E640.MirrorCS", {"start": v(-20.15, -20.88) * mm, "end": v(-24.78, -20.88) * mm});
            skLineSegment(sketch, "E641.MirrorCS", {"start": v(-7.45, -97.08) * mm, "end": v(-12.08, -97.08) * mm});
            skLineSegment(sketch, "E642.MirrorCS", {"start": v(-7.45, -46.28) * mm, "end": v(-12.08, -46.28) * mm});
            skLineSegment(sketch, "E643.MirrorCS", {"start": v(-32.85, -97.08) * mm, "end": v(-37.48, -97.08) * mm});
            skLineSegment(sketch, "E644.MirrorCS", {"start": v(-20.15, -71.68) * mm, "end": v(-24.78, -71.68) * mm});
            skLineSegment(sketch, "E645.MirrorCS", {"start": v(-70.95, -71.68) * mm, "end": v(-75.58, -71.68) * mm});
            skLineSegment(sketch, "E646.MirrorCS", {"start": v(-70.95, -20.88) * mm, "end": v(-75.58, -20.88) * mm});
            skLineSegment(sketch, "E647.MirrorCS", {"start": v(-58.25, -97.08) * mm, "end": v(-62.88, -97.08) * mm});
            skLineSegment(sketch, "E648.MirrorCS", {"start": v(17.95, -84.38) * mm, "end": v(13.32, -84.38) * mm});
            skLineSegment(sketch, "E649.MirrorCS", {"start": v(17.95, -33.58) * mm, "end": v(13.32, -33.58) * mm});
            skLineSegment(sketch, "E650.MirrorCS", {"start": v(43.35, -33.58) * mm, "end": v(38.72, -33.58) * mm});
            skLineSegment(sketch, "E651.MirrorCS", {"start": v(43.35, -84.38) * mm, "end": v(38.72, -84.38) * mm});
            skLineSegment(sketch, "E652.MirrorCS", {"start": v(68.75, -84.38) * mm, "end": v(64.12, -84.38) * mm});
            skLineSegment(sketch, "E653.MirrorCS", {"start": v(68.75, -33.58) * mm, "end": v(64.12, -33.58) * mm});
            skLineSegment(sketch, "E654.MirrorCS", {"start": v(-96.35, -71.68) * mm, "end": v(-100.98, -71.68) * mm});
            skLineSegment(sketch, "E655.MirrorCS", {"start": v(-96.35, -20.88) * mm, "end": v(-100.98, -20.88) * mm});
            skLineSegment(sketch, "E656.MirrorCS", {"start": v(-83.65, -97.08) * mm, "end": v(-88.28, -97.08) * mm});
            skLineSegment(sketch, "E657.MirrorCS", {"start": v(119.55, -89) * mm, "end": v(119.55, -84.38) * mm});
            skLineSegment(sketch, "E658.MirrorCS", {"start": v(119.55, -38.2) * mm, "end": v(119.55, -33.58) * mm});
            skLineSegment(sketch, "E659.MirrorCS", {"start": v(-7.45, -101.7) * mm, "end": v(-7.45, -97.08) * mm});
            skLineSegment(sketch, "E660.MirrorCS", {"start": v(-7.45, -0.1) * mm, "end": v(-7.45, 4.52) * mm});
            skLineSegment(sketch, "E661.MirrorCS", {"start": v(-7.45, -50.9) * mm, "end": v(-7.45, -46.28) * mm});
            skLineSegment(sketch, "E662.MirrorCS", {"start": v(-32.85, -101.7) * mm, "end": v(-32.85, -97.08) * mm});
            skLineSegment(sketch, "E663.MirrorCS", {"start": v(-32.85, -0.1) * mm, "end": v(-32.85, 4.52) * mm});
            skLineSegment(sketch, "E664.MirrorCS", {"start": v(-20.15, -76.3) * mm, "end": v(-20.15, -71.68) * mm});
            skLineSegment(sketch, "E665.MirrorCS", {"start": v(-58.25, -0.1) * mm, "end": v(-58.25, 4.52) * mm});
            skLineSegment(sketch, "E666.MirrorCS", {"start": v(-83.65, -0.1) * mm, "end": v(-83.65, 4.52) * mm});
            skLineSegment(sketch, "E667.MirrorCS", {"start": v(-70.95, -76.3) * mm, "end": v(-70.95, -71.68) * mm});
            skLineSegment(sketch, "E668.MirrorCS", {"start": v(-70.95, -25.5) * mm, "end": v(-70.95, -20.88) * mm});
            skLineSegment(sketch, "E669.MirrorCS", {"start": v(-58.25, -101.7) * mm, "end": v(-58.25, -97.08) * mm});
            skLineSegment(sketch, "E670.MirrorCS", {"start": v(-96.35, -76.3) * mm, "end": v(-96.35, -71.68) * mm});
            skLineSegment(sketch, "E671.MirrorCS", {"start": v(-96.35, -25.5) * mm, "end": v(-96.35, -20.88) * mm});
            skLineSegment(sketch, "E672.MirrorCS", {"start": v(-83.65, -101.7) * mm, "end": v(-83.65, -97.08) * mm});
            skLineSegment(sketch, "E673.MirrorCS", {"start": v(17.95, -89) * mm, "end": v(17.95, -84.38) * mm});
            skLineSegment(sketch, "E674.MirrorCS", {"start": v(17.95, -38.2) * mm, "end": v(17.95, -33.58) * mm});
            skLineSegment(sketch, "E675.MirrorCS", {"start": v(43.35, -38.2) * mm, "end": v(43.35, -33.58) * mm});
            skLineSegment(sketch, "E676.MirrorCS", {"start": v(56.05, -114.4) * mm, "end": v(56.05, -109.78) * mm});
            skLineSegment(sketch, "E677.MirrorCS", {"start": v(43.35, -89) * mm, "end": v(43.35, -84.38) * mm});
            skLineSegment(sketch, "E678.MirrorCS", {"start": v(68.75, -89) * mm, "end": v(68.75, -84.38) * mm});
            skLineSegment(sketch, "E679.MirrorCS", {"start": v(68.75, -38.2) * mm, "end": v(68.75, -33.58) * mm});
            skLineSegment(sketch, "E680.MirrorCS", {"start": v(94.15, -89) * mm, "end": v(94.15, -84.38) * mm});
            skLineSegment(sketch, "E681.MirrorCS", {"start": v(94.15, -38.2) * mm, "end": v(94.15, -33.58) * mm});
            skLineSegment(sketch, "E682.MirrorCS", {"start": v(-20.15, -38.2) * mm, "end": v(-24.78, -38.2) * mm});
            skLineSegment(sketch, "E683.MirrorCS", {"start": v(-20.15, -89) * mm, "end": v(-24.78, -89) * mm});
            skLineSegment(sketch, "E684.MirrorCS", {"start": v(-32.85, -63.6) * mm, "end": v(-37.48, -63.6) * mm});
            skLineSegment(sketch, "E685.MirrorCS", {"start": v(-32.85, -12.8) * mm, "end": v(-37.48, -12.8) * mm});
            skLineSegment(sketch, "E686.MirrorCS", {"start": v(-58.25, -63.6) * mm, "end": v(-62.88, -63.6) * mm});
            skLineSegment(sketch, "E687.MirrorCS", {"start": v(-58.25, -12.8) * mm, "end": v(-62.88, -12.8) * mm});
            skLineSegment(sketch, "E688.MirrorCS", {"start": v(-45.55, -89) * mm, "end": v(-50.18, -89) * mm});
            skLineSegment(sketch, "E689.MirrorCS", {"start": v(-45.55, -38.2) * mm, "end": v(-50.18, -38.2) * mm});
            skLineSegment(sketch, "E690.MirrorCS", {"start": v(-83.65, -12.8) * mm, "end": v(-88.28, -12.8) * mm});
            skLineSegment(sketch, "E691.MirrorCS", {"start": v(-96.35, -38.2) * mm, "end": v(-100.98, -38.2) * mm});
            skLineSegment(sketch, "E692.MirrorCS", {"start": v(-96.35, -89) * mm, "end": v(-100.98, -89) * mm});
            skLineSegment(sketch, "E693.MirrorCS", {"start": v(-83.65, -63.6) * mm, "end": v(-88.28, -63.6) * mm});
            skLineSegment(sketch, "E694.MirrorCS", {"start": v(-109.05, -63.6) * mm, "end": v(-113.68, -63.6) * mm});
            skLineSegment(sketch, "E695.MirrorCS", {"start": v(-109.05, -12.8) * mm, "end": v(-113.68, -12.8) * mm});
            skLineSegment(sketch, "E696.MirrorCS", {"start": v(17.95, -101.7) * mm, "end": v(13.32, -101.7) * mm});
            skLineSegment(sketch, "E697.MirrorCS", {"start": v(56.05, -76.3) * mm, "end": v(51.42, -76.3) * mm});
            skLineSegment(sketch, "E698.MirrorCS", {"start": v(56.05, -25.5) * mm, "end": v(51.42, -25.5) * mm});
            skLineSegment(sketch, "E699.MirrorCS", {"start": v(43.35, -101.7) * mm, "end": v(38.72, -101.7) * mm});
            skLineSegment(sketch, "E700.MirrorCS", {"start": v(81.45, -76.3) * mm, "end": v(76.82, -76.3) * mm});
            skLineSegment(sketch, "E701.MirrorCS", {"start": v(81.45, -25.5) * mm, "end": v(76.82, -25.5) * mm});
            skLineSegment(sketch, "E702.MirrorCS", {"start": v(68.75, -101.7) * mm, "end": v(64.12, -101.7) * mm});
            skLineSegment(sketch, "E703.MirrorCS", {"start": v(94.15, -101.7) * mm, "end": v(89.52, -101.7) * mm});
            skLineSegment(sketch, "E704.MirrorCS", {"start": v(119.55, -101.7) * mm, "end": v(114.92, -101.7) * mm});
            skLineSegment(sketch, "E705.MirrorCS", {"start": v(-24.78, -38.2) * mm, "end": v(-24.78, -33.58) * mm});
            skLineSegment(sketch, "E706.MirrorCS", {"start": v(-12.08, -63.6) * mm, "end": v(-12.08, -58.98) * mm});
            skLineSegment(sketch, "E707.MirrorCS", {"start": v(-12.08, -12.8) * mm, "end": v(-12.08, -8.18) * mm});
            skLineSegment(sketch, "E708.MirrorCS", {"start": v(-37.48, -63.6) * mm, "end": v(-37.48, -58.98) * mm});
            skLineSegment(sketch, "E709.MirrorCS", {"start": v(-37.48, -12.8) * mm, "end": v(-37.48, -8.18) * mm});
            skLineSegment(sketch, "E710.MirrorCS", {"start": v(-24.78, -89) * mm, "end": v(-24.78, -84.38) * mm});
            skLineSegment(sketch, "E711.MirrorCS", {"start": v(-50.18, -89) * mm, "end": v(-50.18, -84.38) * mm});
            skLineSegment(sketch, "E712.MirrorCS", {"start": v(-62.88, -63.6) * mm, "end": v(-62.88, -58.98) * mm});
            skLineSegment(sketch, "E713.MirrorCS", {"start": v(-62.88, -12.8) * mm, "end": v(-62.88, -8.18) * mm});
            skLineSegment(sketch, "E714.MirrorCS", {"start": v(-88.28, -12.8) * mm, "end": v(-88.28, -8.18) * mm});
            skLineSegment(sketch, "E715.MirrorCS", {"start": v(-50.18, -38.2) * mm, "end": v(-50.18, -33.58) * mm});
            skLineSegment(sketch, "E716.MirrorCS", {"start": v(-100.98, -89) * mm, "end": v(-100.98, -84.38) * mm});
            skLineSegment(sketch, "E717.MirrorCS", {"start": v(-100.98, -38.2) * mm, "end": v(-100.98, -33.58) * mm});
            skLineSegment(sketch, "E718.MirrorCS", {"start": v(-88.28, -63.6) * mm, "end": v(-88.28, -58.98) * mm});
            skLineSegment(sketch, "E719.MirrorCS", {"start": v(-113.68, -63.6) * mm, "end": v(-113.68, -58.98) * mm});
            skLineSegment(sketch, "E720.MirrorCS", {"start": v(-113.68, -12.8) * mm, "end": v(-113.68, -8.18) * mm});
            skLineSegment(sketch, "E721.MirrorCS", {"start": v(13.32, -101.7) * mm, "end": v(13.32, -97.08) * mm});
            skLineSegment(sketch, "E722.MirrorCS", {"start": v(13.32, -0.1) * mm, "end": v(13.32, 4.52) * mm});
            skLineSegment(sketch, "E723.MirrorCS", {"start": v(38.72, -0.1) * mm, "end": v(38.72, 4.52) * mm});
            skLineSegment(sketch, "E724.MirrorCS", {"start": v(64.12, -0.1) * mm, "end": v(64.12, 4.52) * mm});
            skLineSegment(sketch, "E725.MirrorCS", {"start": v(51.42, -76.3) * mm, "end": v(51.42, -71.68) * mm});
            skLineSegment(sketch, "E726.MirrorCS", {"start": v(51.42, -25.5) * mm, "end": v(51.42, -20.88) * mm});
            skLineSegment(sketch, "E727.MirrorCS", {"start": v(38.72, -101.7) * mm, "end": v(38.72, -97.08) * mm});
            skLineSegment(sketch, "E728.MirrorCS", {"start": v(64.12, -101.7) * mm, "end": v(64.12, -97.08) * mm});
            skLineSegment(sketch, "E729.MirrorCS", {"start": v(89.52, -101.7) * mm, "end": v(89.52, -97.08) * mm});
            skLineSegment(sketch, "E730.MirrorCS", {"start": v(89.52, -0.1) * mm, "end": v(89.52, 4.52) * mm});
            skLineSegment(sketch, "E731.MirrorCS", {"start": v(114.92, -101.7) * mm, "end": v(114.92, -97.08) * mm});
            skLineSegment(sketch, "E732.MirrorCS", {"start": v(17.95, -97.08) * mm, "end": v(13.32, -97.08) * mm});
            skLineSegment(sketch, "E733.MirrorCS", {"start": v(30.65, -20.88) * mm, "end": v(26.02, -20.88) * mm});
            skLineSegment(sketch, "E734.MirrorCS", {"start": v(30.65, -71.68) * mm, "end": v(26.02, -71.68) * mm});
            skLineSegment(sketch, "E735", {"start": v(41.03, -97.08) * mm, "end": v(41.03, -89) * mm});
            skLineSegment(sketch, "E736", {"start": v(28.35, -97.05) * mm, "end": v(28.2, -88.62) * mm});
            skSolve(sketch);
        }
        {
            var Q0;
            {var subQ52=sQuery(id+"F0.wireOp",EDGE,"E22.MirrorCS");Q0=makeQuery(id+"F0.imprint","IMPRINT",FACE,{"disambiguationData":[TD([[makeQuery(id+"F0.imprint","IMPRINT",EDGE,{"derivedFrom":subQ52}),1.0]])]});}
            var Q1;
            {var subQ56=sQuery(id+"F0.wireOp",EDGE,"E6.0.1.1");Q1=makeQuery(id+"F0.imprint","IMPRINT",FACE,{"disambiguationData":[TD([[makeQuery(id+"F0.imprint","IMPRINT",EDGE,{"derivedFrom":subQ56}),-1.0]])]});}
            var Q2;
            Q2=makeQuery(id+"F0.imprint","IMPRINT",FACE,{"disambiguationData":[TD([[makeQuery(id+"F0.imprint","IMPRINT",EDGE,{"derivedFrom":sQuery(id+"F0.wireOp",EDGE,"E6.1.1.0")}),-1.0]])]});
            var Q3;
            {var subQ26=sQuery(id+"F0.wireOp",EDGE,"E30.MirrorCS");Q3=makeQuery(id+"F0.imprint","IMPRINT",FACE,{"disambiguationData":[TD([[makeQuery(id+"F0.imprint","IMPRINT",EDGE,{"derivedFrom":subQ26}),-1.0]])]});}
            extrude(context, id + "F1", {"entities" : qUnion([Q0, Q1, Q2, Q3]), "depth" : 3.17 * mm});
        }
    });
